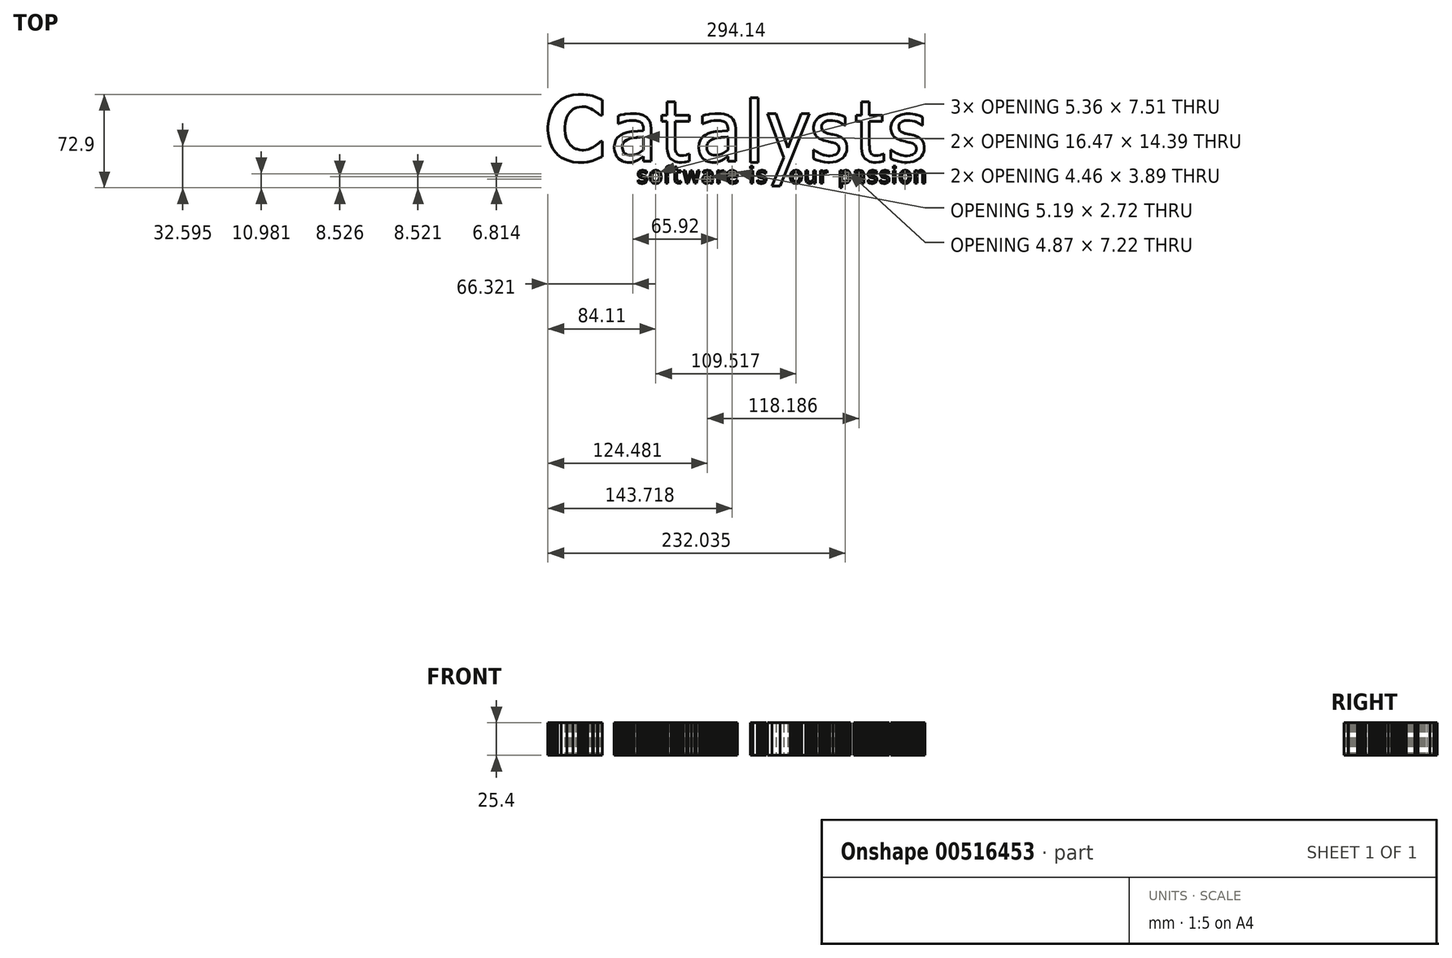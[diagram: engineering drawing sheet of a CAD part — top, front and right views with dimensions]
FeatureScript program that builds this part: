
annotation { "Feature Type Name" : "Feature", "Feature Type Description" : "" }
export const myFeature = defineFeature(function(context is Context, id is Id, definition is map)
    precondition{}
    {
        {
            var Q0;
            Q0=qCreatedBy(makeId("Top.planeOp"),FACE);
            var sketch = newSketch(context, id + "F0", { "sketchPlane" : qUnion([Q0])});
            skLineSegment(sketch, "E0", {"start": v(-122.05, -16.67) * mm, "end": v(-123.41, -16.67) * mm});
            skLineSegment(sketch, "E1", {"start": v(-123.41, -16.67) * mm, "end": v(-127.5, -16.24) * mm});
            skLineSegment(sketch, "E2", {"start": v(-127.5, -16.24) * mm, "end": v(-132.36, -14.93) * mm});
            skLineSegment(sketch, "E3", {"start": v(-132.36, -14.93) * mm, "end": v(-136.64, -12.76) * mm});
            skLineSegment(sketch, "E4", {"start": v(-136.64, -12.76) * mm, "end": v(-139.49, -10.56) * mm});
            skLineSegment(sketch, "E5", {"start": v(-139.49, -10.56) * mm, "end": v(-140.31, -9.71) * mm});
            skLineSegment(sketch, "E6", {"start": v(-140.31, -9.71) * mm, "end": v(-141.15, -8.85) * mm});
            skLineSegment(sketch, "E7", {"start": v(-141.15, -8.85) * mm, "end": v(-143.27, -5.89) * mm});
            skLineSegment(sketch, "E8", {"start": v(-143.27, -5.89) * mm, "end": v(-145.38, -1.35) * mm});
            skLineSegment(sketch, "E9", {"start": v(-145.38, -1.35) * mm, "end": v(-146.65, 3.9) * mm});
            skLineSegment(sketch, "E10", {"start": v(-146.65, 3.9) * mm, "end": v(-147.07, 8.36) * mm});
            skLineSegment(sketch, "E11", {"start": v(-147.07, 8.36) * mm, "end": v(-147.07, 9.84) * mm});
            skLineSegment(sketch, "E12", {"start": v(-147.07, 9.84) * mm, "end": v(-147.07, 11.28) * mm});
            skLineSegment(sketch, "E13", {"start": v(-147.07, 11.28) * mm, "end": v(-146.65, 15.6) * mm});
            skLineSegment(sketch, "E14", {"start": v(-146.65, 15.6) * mm, "end": v(-145.38, 20.76) * mm});
            skLineSegment(sketch, "E15", {"start": v(-145.38, 20.76) * mm, "end": v(-143.26, 25.3) * mm});
            skLineSegment(sketch, "E16", {"start": v(-143.26, 25.3) * mm, "end": v(-141.13, 28.33) * mm});
            skLineSegment(sketch, "E17", {"start": v(-141.13, 28.33) * mm, "end": v(-140.3, 29.22) * mm});
            skLineSegment(sketch, "E18", {"start": v(-140.3, 29.22) * mm, "end": v(-139.47, 30.1) * mm});
            skLineSegment(sketch, "E19", {"start": v(-139.47, 30.1) * mm, "end": v(-136.61, 32.38) * mm});
            skLineSegment(sketch, "E20", {"start": v(-136.61, 32.38) * mm, "end": v(-132.34, 34.64) * mm});
            skLineSegment(sketch, "E21", {"start": v(-132.34, 34.64) * mm, "end": v(-127.47, 36) * mm});
            skLineSegment(sketch, "E22", {"start": v(-127.47, 36) * mm, "end": v(-123.37, 36.45) * mm});
            skLineSegment(sketch, "E23", {"start": v(-123.37, 36.45) * mm, "end": v(-122, 36.45) * mm});
            skLineSegment(sketch, "E24", {"start": v(-122, 36.45) * mm, "end": v(-121.28, 36.45) * mm});
            skLineSegment(sketch, "E25", {"start": v(-121.28, 36.45) * mm, "end": v(-119.1, 36.36) * mm});
            skLineSegment(sketch, "E26", {"start": v(-119.1, 36.36) * mm, "end": v(-116.92, 36.16) * mm});
            skLineSegment(sketch, "E27", {"start": v(-116.92, 36.16) * mm, "end": v(-116.52, 36.1) * mm});
            skLineSegment(sketch, "E28", {"start": v(-116.52, 36.1) * mm, "end": v(-116.11, 36.05) * mm});
            skLineSegment(sketch, "E29", {"start": v(-116.11, 36.05) * mm, "end": v(-112.22, 35.26) * mm});
            skLineSegment(sketch, "E30", {"start": v(-112.22, 35.26) * mm, "end": v(-111.85, 35.15) * mm});
            skLineSegment(sketch, "E31", {"start": v(-111.85, 35.15) * mm, "end": v(-111.56, 35.06) * mm});
            skLineSegment(sketch, "E32", {"start": v(-111.56, 35.06) * mm, "end": v(-110.02, 34.53) * mm});
            skLineSegment(sketch, "E33", {"start": v(-110.02, 34.53) * mm, "end": v(-108.37, 33.88) * mm});
            skLineSegment(sketch, "E34", {"start": v(-108.37, 33.88) * mm, "end": v(-108.02, 33.73) * mm});
            skLineSegment(sketch, "E35", {"start": v(-108.02, 33.73) * mm, "end": v(-107.69, 33.58) * mm});
            skLineSegment(sketch, "E36", {"start": v(-107.69, 33.58) * mm, "end": v(-106.17, 32.9) * mm});
            skLineSegment(sketch, "E37", {"start": v(-106.17, 32.9) * mm, "end": v(-104.9, 32.3) * mm});
            skLineSegment(sketch, "E38", {"start": v(-104.9, 32.3) * mm, "end": v(-104.7, 32.19) * mm});
            skLineSegment(sketch, "E39", {"start": v(-104.7, 32.19) * mm, "end": v(-104.7, 20) * mm});
            skLineSegment(sketch, "E40", {"start": v(-104.7, 20) * mm, "end": v(-106, 20) * mm});
            skLineSegment(sketch, "E41", {"start": v(-106, 20) * mm, "end": v(-106.16, 20.14) * mm});
            skLineSegment(sketch, "E42", {"start": v(-106.16, 20.14) * mm, "end": v(-107.06, 20.91) * mm});
            skLineSegment(sketch, "E43", {"start": v(-107.06, 20.91) * mm, "end": v(-108.1, 21.78) * mm});
            skLineSegment(sketch, "E44", {"start": v(-108.1, 21.78) * mm, "end": v(-108.34, 21.97) * mm});
            skLineSegment(sketch, "E45", {"start": v(-108.34, 21.97) * mm, "end": v(-108.57, 22.16) * mm});
            skLineSegment(sketch, "E46", {"start": v(-108.57, 22.16) * mm, "end": v(-111.24, 24.05) * mm});
            skLineSegment(sketch, "E47", {"start": v(-111.24, 24.05) * mm, "end": v(-111.54, 24.23) * mm});
            skLineSegment(sketch, "E48", {"start": v(-111.54, 24.23) * mm, "end": v(-111.83, 24.41) * mm});
            skLineSegment(sketch, "E49", {"start": v(-111.83, 24.41) * mm, "end": v(-113.4, 25.25) * mm});
            skLineSegment(sketch, "E50", {"start": v(-113.4, 25.25) * mm, "end": v(-115.1, 25.97) * mm});
            skLineSegment(sketch, "E51", {"start": v(-115.1, 25.97) * mm, "end": v(-115.46, 26.1) * mm});
            skLineSegment(sketch, "E52", {"start": v(-115.46, 26.1) * mm, "end": v(-115.82, 26.22) * mm});
            skLineSegment(sketch, "E53", {"start": v(-115.82, 26.22) * mm, "end": v(-117.67, 26.67) * mm});
            skLineSegment(sketch, "E54", {"start": v(-117.67, 26.67) * mm, "end": v(-119.37, 26.86) * mm});
            skLineSegment(sketch, "E55", {"start": v(-119.37, 26.86) * mm, "end": v(-119.94, 26.86) * mm});
            skLineSegment(sketch, "E56", {"start": v(-119.94, 26.86) * mm, "end": v(-120.61, 26.86) * mm});
            skLineSegment(sketch, "E57", {"start": v(-120.61, 26.86) * mm, "end": v(-122.61, 26.64) * mm});
            skLineSegment(sketch, "E58", {"start": v(-122.61, 26.64) * mm, "end": v(-124.66, 26.14) * mm});
            skLineSegment(sketch, "E59", {"start": v(-124.66, 26.14) * mm, "end": v(-125.04, 26) * mm});
            skLineSegment(sketch, "E60", {"start": v(-125.04, 26) * mm, "end": v(-125.43, 25.85) * mm});
            skLineSegment(sketch, "E61", {"start": v(-125.43, 25.85) * mm, "end": v(-127.3, 24.8) * mm});
            skLineSegment(sketch, "E62", {"start": v(-127.3, 24.8) * mm, "end": v(-129.1, 23.32) * mm});
            skLineSegment(sketch, "E63", {"start": v(-129.1, 23.32) * mm, "end": v(-129.46, 22.96) * mm});
            skLineSegment(sketch, "E64", {"start": v(-129.46, 22.96) * mm, "end": v(-129.78, 22.63) * mm});
            skLineSegment(sketch, "E65", {"start": v(-129.78, 22.63) * mm, "end": v(-131.22, 20.65) * mm});
            skLineSegment(sketch, "E66", {"start": v(-131.22, 20.65) * mm, "end": v(-132.4, 18.22) * mm});
            skLineSegment(sketch, "E67", {"start": v(-132.4, 18.22) * mm, "end": v(-132.61, 17.66) * mm});
            skLineSegment(sketch, "E68", {"start": v(-132.61, 17.66) * mm, "end": v(-132.81, 17.1) * mm});
            skLineSegment(sketch, "E69", {"start": v(-132.81, 17.1) * mm, "end": v(-133.52, 14.04) * mm});
            skLineSegment(sketch, "E70", {"start": v(-133.52, 14.04) * mm, "end": v(-133.81, 10.86) * mm});
            skLineSegment(sketch, "E71", {"start": v(-133.81, 10.86) * mm, "end": v(-133.81, 9.8) * mm});
            skLineSegment(sketch, "E72", {"start": v(-133.81, 9.8) * mm, "end": v(-133.81, 8.7) * mm});
            skLineSegment(sketch, "E73", {"start": v(-133.81, 8.7) * mm, "end": v(-133.5, 5.41) * mm});
            skLineSegment(sketch, "E74", {"start": v(-133.5, 5.41) * mm, "end": v(-132.76, 2.32) * mm});
            skLineSegment(sketch, "E75", {"start": v(-132.76, 2.32) * mm, "end": v(-132.54, 1.78) * mm});
            skLineSegment(sketch, "E76", {"start": v(-132.54, 1.78) * mm, "end": v(-132.33, 1.24) * mm});
            skLineSegment(sketch, "E77", {"start": v(-132.33, 1.24) * mm, "end": v(-131.08, -1.15) * mm});
            skLineSegment(sketch, "E78", {"start": v(-131.08, -1.15) * mm, "end": v(-129.56, -3.12) * mm});
            skLineSegment(sketch, "E79", {"start": v(-129.56, -3.12) * mm, "end": v(-129.21, -3.46) * mm});
            skLineSegment(sketch, "E80", {"start": v(-129.21, -3.46) * mm, "end": v(-128.88, -3.78) * mm});
            skLineSegment(sketch, "E81", {"start": v(-128.88, -3.78) * mm, "end": v(-127.1, -5.1) * mm});
            skLineSegment(sketch, "E82", {"start": v(-127.1, -5.1) * mm, "end": v(-125.18, -6.08) * mm});
            skLineSegment(sketch, "E83", {"start": v(-125.18, -6.08) * mm, "end": v(-124.77, -6.22) * mm});
            skLineSegment(sketch, "E84", {"start": v(-124.77, -6.22) * mm, "end": v(-124.36, -6.37) * mm});
            skLineSegment(sketch, "E85", {"start": v(-124.36, -6.37) * mm, "end": v(-122.32, -6.87) * mm});
            skLineSegment(sketch, "E86", {"start": v(-122.32, -6.87) * mm, "end": v(-120.49, -7.08) * mm});
            skLineSegment(sketch, "E87", {"start": v(-120.49, -7.08) * mm, "end": v(-119.88, -7.08) * mm});
            skLineSegment(sketch, "E88", {"start": v(-119.88, -7.08) * mm, "end": v(-119.26, -7.08) * mm});
            skLineSegment(sketch, "E89", {"start": v(-119.26, -7.08) * mm, "end": v(-117.4, -6.88) * mm});
            skLineSegment(sketch, "E90", {"start": v(-117.4, -6.88) * mm, "end": v(-115.41, -6.39) * mm});
            skLineSegment(sketch, "E91", {"start": v(-115.41, -6.39) * mm, "end": v(-115.03, -6.25) * mm});
            skLineSegment(sketch, "E92", {"start": v(-115.03, -6.25) * mm, "end": v(-114.65, -6.1) * mm});
            skLineSegment(sketch, "E93", {"start": v(-114.65, -6.1) * mm, "end": v(-112.92, -5.36) * mm});
            skLineSegment(sketch, "E94", {"start": v(-112.92, -5.36) * mm, "end": v(-111.42, -4.56) * mm});
            skLineSegment(sketch, "E95", {"start": v(-111.42, -4.56) * mm, "end": v(-111.15, -4.39) * mm});
            skLineSegment(sketch, "E96", {"start": v(-111.15, -4.39) * mm, "end": v(-110.87, -4.2) * mm});
            skLineSegment(sketch, "E97", {"start": v(-110.87, -4.2) * mm, "end": v(-108.35, -2.4) * mm});
            skLineSegment(sketch, "E98", {"start": v(-108.35, -2.4) * mm, "end": v(-108.14, -2.21) * mm});
            skLineSegment(sketch, "E99", {"start": v(-108.14, -2.21) * mm, "end": v(-107.92, -2.03) * mm});
            skLineSegment(sketch, "E100", {"start": v(-107.92, -2.03) * mm, "end": v(-106.03, -0.4) * mm});
            skLineSegment(sketch, "E101", {"start": v(-106.03, -0.4) * mm, "end": v(-105.87, -0.26) * mm});
            skLineSegment(sketch, "E102", {"start": v(-105.87, -0.26) * mm, "end": v(-104.7, -0.26) * mm});
            skLineSegment(sketch, "E103", {"start": v(-104.7, -0.26) * mm, "end": v(-104.7, -12.27) * mm});
            skLineSegment(sketch, "E104", {"start": v(-104.7, -12.27) * mm, "end": v(-104.93, -12.38) * mm});
            skLineSegment(sketch, "E105", {"start": v(-104.93, -12.38) * mm, "end": v(-107.65, -13.63) * mm});
            skLineSegment(sketch, "E106", {"start": v(-107.65, -13.63) * mm, "end": v(-107.96, -13.77) * mm});
            skLineSegment(sketch, "E107", {"start": v(-107.96, -13.77) * mm, "end": v(-108.27, -13.9) * mm});
            skLineSegment(sketch, "E108", {"start": v(-108.27, -13.9) * mm, "end": v(-111.46, -15.1) * mm});
            skLineSegment(sketch, "E109", {"start": v(-111.46, -15.1) * mm, "end": v(-111.79, -15.2) * mm});
            skLineSegment(sketch, "E110", {"start": v(-111.79, -15.2) * mm, "end": v(-112.18, -15.32) * mm});
            skLineSegment(sketch, "E111", {"start": v(-112.18, -15.32) * mm, "end": v(-115.92, -16.22) * mm});
            skLineSegment(sketch, "E112", {"start": v(-115.92, -16.22) * mm, "end": v(-116.27, -16.28) * mm});
            skLineSegment(sketch, "E113", {"start": v(-116.27, -16.28) * mm, "end": v(-116.62, -16.35) * mm});
            skLineSegment(sketch, "E114", {"start": v(-116.62, -16.35) * mm, "end": v(-118.77, -16.58) * mm});
            skLineSegment(sketch, "E115", {"start": v(-118.77, -16.58) * mm, "end": v(-121.23, -16.67) * mm});
            skLineSegment(sketch, "E116", {"start": v(-121.23, -16.67) * mm, "end": v(-122.05, -16.67) * mm});
            skLineSegment(sketch, "E117", {"start": v(-72.51, -6.72) * mm, "end": v(-72.51, 3.34) * mm});
            skLineSegment(sketch, "E118", {"start": v(-72.51, 3.34) * mm, "end": v(-72.87, 3.3) * mm});
            skLineSegment(sketch, "E119", {"start": v(-72.87, 3.3) * mm, "end": v(-74.97, 3.1) * mm});
            skLineSegment(sketch, "E120", {"start": v(-74.97, 3.1) * mm, "end": v(-77.44, 2.85) * mm});
            skLineSegment(sketch, "E121", {"start": v(-77.44, 2.85) * mm, "end": v(-78, 2.8) * mm});
            skLineSegment(sketch, "E122", {"start": v(-78, 2.8) * mm, "end": v(-78.55, 2.74) * mm});
            skLineSegment(sketch, "E123", {"start": v(-78.55, 2.74) * mm, "end": v(-81, 2.39) * mm});
            skLineSegment(sketch, "E124", {"start": v(-81, 2.39) * mm, "end": v(-83.03, 1.95) * mm});
            skLineSegment(sketch, "E125", {"start": v(-83.03, 1.95) * mm, "end": v(-83.37, 1.85) * mm});
            skLineSegment(sketch, "E126", {"start": v(-83.37, 1.85) * mm, "end": v(-83.77, 1.72) * mm});
            skLineSegment(sketch, "E127", {"start": v(-83.77, 1.72) * mm, "end": v(-85.6, 0.9) * mm});
            skLineSegment(sketch, "E128", {"start": v(-85.6, 0.9) * mm, "end": v(-87.13, -0.2) * mm});
            skLineSegment(sketch, "E129", {"start": v(-87.13, -0.2) * mm, "end": v(-87.4, -0.45) * mm});
            skLineSegment(sketch, "E130", {"start": v(-87.4, -0.45) * mm, "end": v(-87.6, -0.64) * mm});
            skLineSegment(sketch, "E131", {"start": v(-87.6, -0.64) * mm, "end": v(-88.1, -1.3) * mm});
            skLineSegment(sketch, "E132", {"start": v(-88.1, -1.3) * mm, "end": v(-88.6, -2.3) * mm});
            skLineSegment(sketch, "E133", {"start": v(-88.6, -2.3) * mm, "end": v(-88.89, -3.45) * mm});
            skLineSegment(sketch, "E134", {"start": v(-88.89, -3.45) * mm, "end": v(-88.99, -4.42) * mm});
            skLineSegment(sketch, "E135", {"start": v(-88.99, -4.42) * mm, "end": v(-88.99, -4.75) * mm});
            skLineSegment(sketch, "E136", {"start": v(-88.99, -4.75) * mm, "end": v(-88.99, -5.12) * mm});
            skLineSegment(sketch, "E137", {"start": v(-88.99, -5.12) * mm, "end": v(-88.88, -6.22) * mm});
            skLineSegment(sketch, "E138", {"start": v(-88.88, -6.22) * mm, "end": v(-88.55, -7.49) * mm});
            skLineSegment(sketch, "E139", {"start": v(-88.55, -7.49) * mm, "end": v(-88, -8.57) * mm});
            skLineSegment(sketch, "E140", {"start": v(-88, -8.57) * mm, "end": v(-87.46, -9.27) * mm});
            skLineSegment(sketch, "E141", {"start": v(-87.46, -9.27) * mm, "end": v(-87.24, -9.46) * mm});
            skLineSegment(sketch, "E142", {"start": v(-87.24, -9.46) * mm, "end": v(-87.02, -9.66) * mm});
            skLineSegment(sketch, "E143", {"start": v(-87.02, -9.66) * mm, "end": v(-86.26, -10.15) * mm});
            skLineSegment(sketch, "E144", {"start": v(-86.26, -10.15) * mm, "end": v(-85.08, -10.65) * mm});
            skLineSegment(sketch, "E145", {"start": v(-85.08, -10.65) * mm, "end": v(-83.7, -10.95) * mm});
            skLineSegment(sketch, "E146", {"start": v(-83.7, -10.95) * mm, "end": v(-82.5, -11.05) * mm});
            skLineSegment(sketch, "E147", {"start": v(-82.5, -11.05) * mm, "end": v(-82.1, -11.05) * mm});
            skLineSegment(sketch, "E148", {"start": v(-82.1, -11.05) * mm, "end": v(-81.41, -11.05) * mm});
            skLineSegment(sketch, "E149", {"start": v(-81.41, -11.05) * mm, "end": v(-79.36, -10.73) * mm});
            skLineSegment(sketch, "E150", {"start": v(-79.36, -10.73) * mm, "end": v(-77.28, -10) * mm});
            skLineSegment(sketch, "E151", {"start": v(-77.28, -10) * mm, "end": v(-76.88, -9.8) * mm});
            skLineSegment(sketch, "E152", {"start": v(-76.88, -9.8) * mm, "end": v(-76.5, -9.6) * mm});
            skLineSegment(sketch, "E153", {"start": v(-76.5, -9.6) * mm, "end": v(-74.62, -8.4) * mm});
            skLineSegment(sketch, "E154", {"start": v(-74.62, -8.4) * mm, "end": v(-72.85, -7.03) * mm});
            skLineSegment(sketch, "E155", {"start": v(-72.85, -7.03) * mm, "end": v(-72.51, -6.72) * mm});
            skLineSegment(sketch, "E156", {"start": v(-72.51, -11.8) * mm, "end": v(-72.64, -11.89) * mm});
            skLineSegment(sketch, "E157", {"start": v(-72.64, -11.89) * mm, "end": v(-73.38, -12.46) * mm});
            skLineSegment(sketch, "E158", {"start": v(-73.38, -12.46) * mm, "end": v(-74.3, -13.17) * mm});
            skLineSegment(sketch, "E159", {"start": v(-74.3, -13.17) * mm, "end": v(-74.5, -13.34) * mm});
            skLineSegment(sketch, "E160", {"start": v(-74.5, -13.34) * mm, "end": v(-74.7, -13.5) * mm});
            skLineSegment(sketch, "E161", {"start": v(-74.7, -13.5) * mm, "end": v(-76.72, -14.8) * mm});
            skLineSegment(sketch, "E162", {"start": v(-76.72, -14.8) * mm, "end": v(-76.9, -14.9) * mm});
            skLineSegment(sketch, "E163", {"start": v(-76.9, -14.9) * mm, "end": v(-77.18, -15.04) * mm});
            skLineSegment(sketch, "E164", {"start": v(-77.18, -15.04) * mm, "end": v(-79.79, -16.14) * mm});
            skLineSegment(sketch, "E165", {"start": v(-79.79, -16.14) * mm, "end": v(-80.03, -16.22) * mm});
            skLineSegment(sketch, "E166", {"start": v(-80.03, -16.22) * mm, "end": v(-80.29, -16.29) * mm});
            skLineSegment(sketch, "E167", {"start": v(-80.29, -16.29) * mm, "end": v(-81.86, -16.55) * mm});
            skLineSegment(sketch, "E168", {"start": v(-81.86, -16.55) * mm, "end": v(-83.67, -16.67) * mm});
            skLineSegment(sketch, "E169", {"start": v(-83.67, -16.67) * mm, "end": v(-84.27, -16.67) * mm});
            skLineSegment(sketch, "E170", {"start": v(-84.27, -16.67) * mm, "end": v(-84.82, -16.67) * mm});
            skLineSegment(sketch, "E171", {"start": v(-84.82, -16.67) * mm, "end": v(-86.46, -16.45) * mm});
            skLineSegment(sketch, "E172", {"start": v(-86.46, -16.45) * mm, "end": v(-88.2, -15.95) * mm});
            skLineSegment(sketch, "E173", {"start": v(-88.2, -15.95) * mm, "end": v(-88.53, -15.8) * mm});
            skLineSegment(sketch, "E174", {"start": v(-88.53, -15.8) * mm, "end": v(-88.87, -15.67) * mm});
            skLineSegment(sketch, "E175", {"start": v(-88.87, -15.67) * mm, "end": v(-90.42, -14.8) * mm});
            skLineSegment(sketch, "E176", {"start": v(-90.42, -14.8) * mm, "end": v(-91.81, -13.7) * mm});
            skLineSegment(sketch, "E177", {"start": v(-91.81, -13.7) * mm, "end": v(-92.07, -13.45) * mm});
            skLineSegment(sketch, "E178", {"start": v(-92.07, -13.45) * mm, "end": v(-92.31, -13.2) * mm});
            skLineSegment(sketch, "E179", {"start": v(-92.31, -13.2) * mm, "end": v(-93.38, -11.78) * mm});
            skLineSegment(sketch, "E180", {"start": v(-93.38, -11.78) * mm, "end": v(-94.25, -10.13) * mm});
            skLineSegment(sketch, "E181", {"start": v(-94.25, -10.13) * mm, "end": v(-94.4, -9.76) * mm});
            skLineSegment(sketch, "E182", {"start": v(-94.4, -9.76) * mm, "end": v(-94.55, -9.4) * mm});
            skLineSegment(sketch, "E183", {"start": v(-94.55, -9.4) * mm, "end": v(-95.07, -7.51) * mm});
            skLineSegment(sketch, "E184", {"start": v(-95.07, -7.51) * mm, "end": v(-95.29, -5.73) * mm});
            skLineSegment(sketch, "E185", {"start": v(-95.29, -5.73) * mm, "end": v(-95.29, -5.14) * mm});
            skLineSegment(sketch, "E186", {"start": v(-95.29, -5.14) * mm, "end": v(-95.29, -4.26) * mm});
            skLineSegment(sketch, "E187", {"start": v(-95.29, -4.26) * mm, "end": v(-94.9, -1.65) * mm});
            skLineSegment(sketch, "E188", {"start": v(-94.9, -1.65) * mm, "end": v(-93.97, 0.84) * mm});
            skLineSegment(sketch, "E189", {"start": v(-93.97, 0.84) * mm, "end": v(-93.7, 1.28) * mm});
            skLineSegment(sketch, "E190", {"start": v(-93.7, 1.28) * mm, "end": v(-93.5, 1.6) * mm});
            skLineSegment(sketch, "E191", {"start": v(-93.5, 1.6) * mm, "end": v(-92.79, 2.53) * mm});
            skLineSegment(sketch, "E192", {"start": v(-92.79, 2.53) * mm, "end": v(-91.64, 3.65) * mm});
            skLineSegment(sketch, "E193", {"start": v(-91.64, 3.65) * mm, "end": v(-90.27, 4.62) * mm});
            skLineSegment(sketch, "E194", {"start": v(-90.27, 4.62) * mm, "end": v(-89.08, 5.28) * mm});
            skLineSegment(sketch, "E195", {"start": v(-89.08, 5.28) * mm, "end": v(-88.67, 5.47) * mm});
            skLineSegment(sketch, "E196", {"start": v(-88.67, 5.47) * mm, "end": v(-88.16, 5.7) * mm});
            skLineSegment(sketch, "E197", {"start": v(-88.16, 5.7) * mm, "end": v(-85.34, 6.65) * mm});
            skLineSegment(sketch, "E198", {"start": v(-85.34, 6.65) * mm, "end": v(-82.15, 7.31) * mm});
            skLineSegment(sketch, "E199", {"start": v(-82.15, 7.31) * mm, "end": v(-81.46, 7.4) * mm});
            skLineSegment(sketch, "E200", {"start": v(-81.46, 7.4) * mm, "end": v(-80.77, 7.49) * mm});
            skLineSegment(sketch, "E201", {"start": v(-80.77, 7.49) * mm, "end": v(-73.31, 8.15) * mm});
            skLineSegment(sketch, "E202", {"start": v(-73.31, 8.15) * mm, "end": v(-72.51, 8.19) * mm});
            skLineSegment(sketch, "E203", {"start": v(-72.51, 8.19) * mm, "end": v(-72.51, 9.37) * mm});
            skLineSegment(sketch, "E204", {"start": v(-72.51, 9.37) * mm, "end": v(-72.51, 9.85) * mm});
            skLineSegment(sketch, "E205", {"start": v(-72.51, 9.85) * mm, "end": v(-72.67, 11.3) * mm});
            skLineSegment(sketch, "E206", {"start": v(-72.67, 11.3) * mm, "end": v(-73.04, 12.61) * mm});
            skLineSegment(sketch, "E207", {"start": v(-73.04, 12.61) * mm, "end": v(-73.15, 12.83) * mm});
            skLineSegment(sketch, "E208", {"start": v(-73.15, 12.83) * mm, "end": v(-73.25, 13.05) * mm});
            skLineSegment(sketch, "E209", {"start": v(-73.25, 13.05) * mm, "end": v(-73.93, 13.99) * mm});
            skLineSegment(sketch, "E210", {"start": v(-73.93, 13.99) * mm, "end": v(-74.77, 14.73) * mm});
            skLineSegment(sketch, "E211", {"start": v(-74.77, 14.73) * mm, "end": v(-74.96, 14.85) * mm});
            skLineSegment(sketch, "E212", {"start": v(-74.96, 14.85) * mm, "end": v(-75.16, 14.98) * mm});
            skLineSegment(sketch, "E213", {"start": v(-75.16, 14.98) * mm, "end": v(-76.27, 15.48) * mm});
            skLineSegment(sketch, "E214", {"start": v(-76.27, 15.48) * mm, "end": v(-77.54, 15.8) * mm});
            skLineSegment(sketch, "E215", {"start": v(-77.54, 15.8) * mm, "end": v(-77.81, 15.85) * mm});
            skLineSegment(sketch, "E216", {"start": v(-77.81, 15.85) * mm, "end": v(-78.1, 15.89) * mm});
            skLineSegment(sketch, "E217", {"start": v(-78.1, 15.89) * mm, "end": v(-80.5, 16.07) * mm});
            skLineSegment(sketch, "E218", {"start": v(-80.5, 16.07) * mm, "end": v(-81.3, 16.07) * mm});
            skLineSegment(sketch, "E219", {"start": v(-81.3, 16.07) * mm, "end": v(-81.88, 16.07) * mm});
            skLineSegment(sketch, "E220", {"start": v(-81.88, 16.07) * mm, "end": v(-83.6, 15.92) * mm});
            skLineSegment(sketch, "E221", {"start": v(-83.6, 15.92) * mm, "end": v(-85.8, 15.55) * mm});
            skLineSegment(sketch, "E222", {"start": v(-85.8, 15.55) * mm, "end": v(-86.27, 15.44) * mm});
            skLineSegment(sketch, "E223", {"start": v(-86.27, 15.44) * mm, "end": v(-86.74, 15.34) * mm});
            skLineSegment(sketch, "E224", {"start": v(-86.74, 15.34) * mm, "end": v(-91.5, 13.83) * mm});
            skLineSegment(sketch, "E225", {"start": v(-91.5, 13.83) * mm, "end": v(-91.98, 13.63) * mm});
            skLineSegment(sketch, "E226", {"start": v(-91.98, 13.63) * mm, "end": v(-92.34, 13.63) * mm});
            skLineSegment(sketch, "E227", {"start": v(-92.34, 13.63) * mm, "end": v(-92.34, 19.81) * mm});
            skLineSegment(sketch, "E228", {"start": v(-92.34, 19.81) * mm, "end": v(-92.06, 19.9) * mm});
            skLineSegment(sketch, "E229", {"start": v(-92.06, 19.9) * mm, "end": v(-90.28, 20.32) * mm});
            skLineSegment(sketch, "E230", {"start": v(-90.28, 20.32) * mm, "end": v(-88.02, 20.78) * mm});
            skLineSegment(sketch, "E231", {"start": v(-88.02, 20.78) * mm, "end": v(-87.5, 20.88) * mm});
            skLineSegment(sketch, "E232", {"start": v(-87.5, 20.88) * mm, "end": v(-86.97, 20.98) * mm});
            skLineSegment(sketch, "E233", {"start": v(-86.97, 20.98) * mm, "end": v(-82.69, 21.47) * mm});
            skLineSegment(sketch, "E234", {"start": v(-82.69, 21.47) * mm, "end": v(-81.26, 21.47) * mm});
            skLineSegment(sketch, "E235", {"start": v(-81.26, 21.47) * mm, "end": v(-80.4, 21.47) * mm});
            skLineSegment(sketch, "E236", {"start": v(-80.4, 21.47) * mm, "end": v(-77.82, 21.33) * mm});
            skLineSegment(sketch, "E237", {"start": v(-77.82, 21.33) * mm, "end": v(-75.4, 20.98) * mm});
            skLineSegment(sketch, "E238", {"start": v(-75.4, 20.98) * mm, "end": v(-74.96, 20.88) * mm});
            skLineSegment(sketch, "E239", {"start": v(-74.96, 20.88) * mm, "end": v(-74.53, 20.78) * mm});
            skLineSegment(sketch, "E240", {"start": v(-74.53, 20.78) * mm, "end": v(-72.53, 20.06) * mm});
            skLineSegment(sketch, "E241", {"start": v(-72.53, 20.06) * mm, "end": v(-70.7, 19.03) * mm});
            skLineSegment(sketch, "E242", {"start": v(-70.7, 19.03) * mm, "end": v(-70.36, 18.77) * mm});
            skLineSegment(sketch, "E243", {"start": v(-70.36, 18.77) * mm, "end": v(-70.03, 18.52) * mm});
            skLineSegment(sketch, "E244", {"start": v(-70.03, 18.52) * mm, "end": v(-68.63, 17.07) * mm});
            skLineSegment(sketch, "E245", {"start": v(-68.63, 17.07) * mm, "end": v(-67.57, 15.31) * mm});
            skLineSegment(sketch, "E246", {"start": v(-67.57, 15.31) * mm, "end": v(-67.41, 14.92) * mm});
            skLineSegment(sketch, "E247", {"start": v(-67.41, 14.92) * mm, "end": v(-67.25, 14.52) * mm});
            skLineSegment(sketch, "E248", {"start": v(-67.25, 14.52) * mm, "end": v(-66.68, 12.29) * mm});
            skLineSegment(sketch, "E249", {"start": v(-66.68, 12.29) * mm, "end": v(-66.44, 9.93) * mm});
            skLineSegment(sketch, "E250", {"start": v(-66.44, 9.93) * mm, "end": v(-66.44, 9.14) * mm});
            skLineSegment(sketch, "E251", {"start": v(-66.44, 9.14) * mm, "end": v(-66.44, -15.65) * mm});
            skLineSegment(sketch, "E252", {"start": v(-66.44, -15.65) * mm, "end": v(-72.51, -15.65) * mm});
            skLineSegment(sketch, "E253", {"start": v(-72.51, -15.65) * mm, "end": v(-72.51, -11.8) * mm});
            skLineSegment(sketch, "E254", {"start": v(-43.4, -16.67) * mm, "end": v(-44.5, -16.67) * mm});
            skLineSegment(sketch, "E255", {"start": v(-44.5, -16.67) * mm, "end": v(-47.84, -15.95) * mm});
            skLineSegment(sketch, "E256", {"start": v(-47.84, -15.95) * mm, "end": v(-50.72, -14.3) * mm});
            skLineSegment(sketch, "E257", {"start": v(-50.72, -14.3) * mm, "end": v(-51.19, -13.81) * mm});
            skLineSegment(sketch, "E258", {"start": v(-51.19, -13.81) * mm, "end": v(-51.54, -13.46) * mm});
            skLineSegment(sketch, "E259", {"start": v(-51.54, -13.46) * mm, "end": v(-52.4, -12.2) * mm});
            skLineSegment(sketch, "E260", {"start": v(-52.4, -12.2) * mm, "end": v(-53.28, -10.16) * mm});
            skLineSegment(sketch, "E261", {"start": v(-53.28, -10.16) * mm, "end": v(-53.8, -7.7) * mm});
            skLineSegment(sketch, "E262", {"start": v(-53.8, -7.7) * mm, "end": v(-53.97, -5.56) * mm});
            skLineSegment(sketch, "E263", {"start": v(-53.97, -5.56) * mm, "end": v(-53.97, -4.84) * mm});
            skLineSegment(sketch, "E264", {"start": v(-53.97, -4.84) * mm, "end": v(-53.97, 15.24) * mm});
            skLineSegment(sketch, "E265", {"start": v(-53.97, 15.24) * mm, "end": v(-58.1, 15.24) * mm});
            skLineSegment(sketch, "E266", {"start": v(-58.1, 15.24) * mm, "end": v(-58.1, 20.3) * mm});
            skLineSegment(sketch, "E267", {"start": v(-58.1, 20.3) * mm, "end": v(-53.97, 20.3) * mm});
            skLineSegment(sketch, "E268", {"start": v(-53.97, 20.3) * mm, "end": v(-53.97, 30.71) * mm});
            skLineSegment(sketch, "E269", {"start": v(-53.97, 30.71) * mm, "end": v(-47.88, 30.71) * mm});
            skLineSegment(sketch, "E270", {"start": v(-47.88, 30.71) * mm, "end": v(-47.88, 20.3) * mm});
            skLineSegment(sketch, "E271", {"start": v(-47.88, 20.3) * mm, "end": v(-36.64, 20.3) * mm});
            skLineSegment(sketch, "E272", {"start": v(-36.64, 20.3) * mm, "end": v(-36.64, 15.24) * mm});
            skLineSegment(sketch, "E273", {"start": v(-36.64, 15.24) * mm, "end": v(-47.88, 15.24) * mm});
            skLineSegment(sketch, "E274", {"start": v(-47.88, 15.24) * mm, "end": v(-47.88, -1.98) * mm});
            skLineSegment(sketch, "E275", {"start": v(-47.88, -1.98) * mm, "end": v(-47.88, -2.6) * mm});
            skLineSegment(sketch, "E276", {"start": v(-47.88, -2.6) * mm, "end": v(-47.86, -4.43) * mm});
            skLineSegment(sketch, "E277", {"start": v(-47.86, -4.43) * mm, "end": v(-47.8, -6) * mm});
            skLineSegment(sketch, "E278", {"start": v(-47.8, -6) * mm, "end": v(-47.79, -6.25) * mm});
            skLineSegment(sketch, "E279", {"start": v(-47.79, -6.25) * mm, "end": v(-47.77, -6.5) * mm});
            skLineSegment(sketch, "E280", {"start": v(-47.77, -6.5) * mm, "end": v(-47.55, -7.69) * mm});
            skLineSegment(sketch, "E281", {"start": v(-47.55, -7.69) * mm, "end": v(-47.15, -8.82) * mm});
            skLineSegment(sketch, "E282", {"start": v(-47.15, -8.82) * mm, "end": v(-47.04, -9.03) * mm});
            skLineSegment(sketch, "E283", {"start": v(-47.04, -9.03) * mm, "end": v(-46.95, -9.22) * mm});
            skLineSegment(sketch, "E284", {"start": v(-46.95, -9.22) * mm, "end": v(-46.31, -10.03) * mm});
            skLineSegment(sketch, "E285", {"start": v(-46.31, -10.03) * mm, "end": v(-45.45, -10.64) * mm});
            skLineSegment(sketch, "E286", {"start": v(-45.45, -10.64) * mm, "end": v(-45.25, -10.73) * mm});
            skLineSegment(sketch, "E287", {"start": v(-45.25, -10.73) * mm, "end": v(-45.05, -10.83) * mm});
            skLineSegment(sketch, "E288", {"start": v(-45.05, -10.83) * mm, "end": v(-43.8, -11.16) * mm});
            skLineSegment(sketch, "E289", {"start": v(-43.8, -11.16) * mm, "end": v(-42.37, -11.3) * mm});
            skLineSegment(sketch, "E290", {"start": v(-42.37, -11.3) * mm, "end": v(-41.9, -11.3) * mm});
            skLineSegment(sketch, "E291", {"start": v(-41.9, -11.3) * mm, "end": v(-41.18, -11.3) * mm});
            skLineSegment(sketch, "E292", {"start": v(-41.18, -11.3) * mm, "end": v(-39.25, -10.94) * mm});
            skLineSegment(sketch, "E293", {"start": v(-39.25, -10.94) * mm, "end": v(-39.02, -10.87) * mm});
            skLineSegment(sketch, "E294", {"start": v(-39.02, -10.87) * mm, "end": v(-38.79, -10.8) * mm});
            skLineSegment(sketch, "E295", {"start": v(-38.79, -10.8) * mm, "end": v(-37.81, -10.46) * mm});
            skLineSegment(sketch, "E296", {"start": v(-37.81, -10.46) * mm, "end": v(-37.1, -10.19) * mm});
            skLineSegment(sketch, "E297", {"start": v(-37.1, -10.19) * mm, "end": v(-37, -10.14) * mm});
            skLineSegment(sketch, "E298", {"start": v(-37, -10.14) * mm, "end": v(-36.64, -10.14) * mm});
            skLineSegment(sketch, "E299", {"start": v(-36.64, -10.14) * mm, "end": v(-36.64, -15.63) * mm});
            skLineSegment(sketch, "E300", {"start": v(-36.64, -15.63) * mm, "end": v(-36.93, -15.7) * mm});
            skLineSegment(sketch, "E301", {"start": v(-36.93, -15.7) * mm, "end": v(-39.83, -16.33) * mm});
            skLineSegment(sketch, "E302", {"start": v(-39.83, -16.33) * mm, "end": v(-40.13, -16.38) * mm});
            skLineSegment(sketch, "E303", {"start": v(-40.13, -16.38) * mm, "end": v(-40.42, -16.43) * mm});
            skLineSegment(sketch, "E304", {"start": v(-40.42, -16.43) * mm, "end": v(-42.65, -16.67) * mm});
            skLineSegment(sketch, "E305", {"start": v(-42.65, -16.67) * mm, "end": v(-43.4, -16.67) * mm});
            skLineSegment(sketch, "E306", {"start": v(-6.6, -6.72) * mm, "end": v(-6.6, 3.34) * mm});
            skLineSegment(sketch, "E307", {"start": v(-6.6, 3.34) * mm, "end": v(-6.95, 3.3) * mm});
            skLineSegment(sketch, "E308", {"start": v(-6.95, 3.3) * mm, "end": v(-9.04, 3.1) * mm});
            skLineSegment(sketch, "E309", {"start": v(-9.04, 3.1) * mm, "end": v(-11.52, 2.85) * mm});
            skLineSegment(sketch, "E310", {"start": v(-11.52, 2.85) * mm, "end": v(-12.08, 2.8) * mm});
            skLineSegment(sketch, "E311", {"start": v(-12.08, 2.8) * mm, "end": v(-12.63, 2.74) * mm});
            skLineSegment(sketch, "E312", {"start": v(-12.63, 2.74) * mm, "end": v(-15.08, 2.39) * mm});
            skLineSegment(sketch, "E313", {"start": v(-15.08, 2.39) * mm, "end": v(-17.1, 1.95) * mm});
            skLineSegment(sketch, "E314", {"start": v(-17.1, 1.95) * mm, "end": v(-17.45, 1.85) * mm});
            skLineSegment(sketch, "E315", {"start": v(-17.45, 1.85) * mm, "end": v(-17.85, 1.72) * mm});
            skLineSegment(sketch, "E316", {"start": v(-17.85, 1.72) * mm, "end": v(-19.68, 0.9) * mm});
            skLineSegment(sketch, "E317", {"start": v(-19.68, 0.9) * mm, "end": v(-21.21, -0.2) * mm});
            skLineSegment(sketch, "E318", {"start": v(-21.21, -0.2) * mm, "end": v(-21.48, -0.45) * mm});
            skLineSegment(sketch, "E319", {"start": v(-21.48, -0.45) * mm, "end": v(-21.67, -0.64) * mm});
            skLineSegment(sketch, "E320", {"start": v(-21.67, -0.64) * mm, "end": v(-22.18, -1.3) * mm});
            skLineSegment(sketch, "E321", {"start": v(-22.18, -1.3) * mm, "end": v(-22.67, -2.3) * mm});
            skLineSegment(sketch, "E322", {"start": v(-22.67, -2.3) * mm, "end": v(-22.97, -3.45) * mm});
            skLineSegment(sketch, "E323", {"start": v(-22.97, -3.45) * mm, "end": v(-23.07, -4.42) * mm});
            skLineSegment(sketch, "E324", {"start": v(-23.07, -4.42) * mm, "end": v(-23.07, -4.75) * mm});
            skLineSegment(sketch, "E325", {"start": v(-23.07, -4.75) * mm, "end": v(-23.07, -5.12) * mm});
            skLineSegment(sketch, "E326", {"start": v(-23.07, -5.12) * mm, "end": v(-22.96, -6.22) * mm});
            skLineSegment(sketch, "E327", {"start": v(-22.96, -6.22) * mm, "end": v(-22.63, -7.49) * mm});
            skLineSegment(sketch, "E328", {"start": v(-22.63, -7.49) * mm, "end": v(-22.08, -8.57) * mm});
            skLineSegment(sketch, "E329", {"start": v(-22.08, -8.57) * mm, "end": v(-21.54, -9.27) * mm});
            skLineSegment(sketch, "E330", {"start": v(-21.54, -9.27) * mm, "end": v(-21.32, -9.46) * mm});
            skLineSegment(sketch, "E331", {"start": v(-21.32, -9.46) * mm, "end": v(-21.1, -9.66) * mm});
            skLineSegment(sketch, "E332", {"start": v(-21.1, -9.66) * mm, "end": v(-20.34, -10.15) * mm});
            skLineSegment(sketch, "E333", {"start": v(-20.34, -10.15) * mm, "end": v(-19.16, -10.65) * mm});
            skLineSegment(sketch, "E334", {"start": v(-19.16, -10.65) * mm, "end": v(-17.77, -10.95) * mm});
            skLineSegment(sketch, "E335", {"start": v(-17.77, -10.95) * mm, "end": v(-16.58, -11.05) * mm});
            skLineSegment(sketch, "E336", {"start": v(-16.58, -11.05) * mm, "end": v(-16.18, -11.05) * mm});
            skLineSegment(sketch, "E337", {"start": v(-16.18, -11.05) * mm, "end": v(-15.5, -11.05) * mm});
            skLineSegment(sketch, "E338", {"start": v(-15.5, -11.05) * mm, "end": v(-13.44, -10.73) * mm});
            skLineSegment(sketch, "E339", {"start": v(-13.44, -10.73) * mm, "end": v(-11.36, -10) * mm});
            skLineSegment(sketch, "E340", {"start": v(-11.36, -10) * mm, "end": v(-10.96, -9.8) * mm});
            skLineSegment(sketch, "E341", {"start": v(-10.96, -9.8) * mm, "end": v(-10.57, -9.6) * mm});
            skLineSegment(sketch, "E342", {"start": v(-10.57, -9.6) * mm, "end": v(-8.7, -8.4) * mm});
            skLineSegment(sketch, "E343", {"start": v(-8.7, -8.4) * mm, "end": v(-6.93, -7.03) * mm});
            skLineSegment(sketch, "E344", {"start": v(-6.93, -7.03) * mm, "end": v(-6.6, -6.72) * mm});
            skLineSegment(sketch, "E345", {"start": v(-6.6, -11.8) * mm, "end": v(-6.72, -11.89) * mm});
            skLineSegment(sketch, "E346", {"start": v(-6.72, -11.89) * mm, "end": v(-7.46, -12.46) * mm});
            skLineSegment(sketch, "E347", {"start": v(-7.46, -12.46) * mm, "end": v(-8.38, -13.17) * mm});
            skLineSegment(sketch, "E348", {"start": v(-8.38, -13.17) * mm, "end": v(-8.59, -13.34) * mm});
            skLineSegment(sketch, "E349", {"start": v(-8.59, -13.34) * mm, "end": v(-8.8, -13.5) * mm});
            skLineSegment(sketch, "E350", {"start": v(-8.8, -13.5) * mm, "end": v(-10.8, -14.8) * mm});
            skLineSegment(sketch, "E351", {"start": v(-10.8, -14.8) * mm, "end": v(-10.99, -14.9) * mm});
            skLineSegment(sketch, "E352", {"start": v(-10.99, -14.9) * mm, "end": v(-11.26, -15.04) * mm});
            skLineSegment(sketch, "E353", {"start": v(-11.26, -15.04) * mm, "end": v(-13.87, -16.14) * mm});
            skLineSegment(sketch, "E354", {"start": v(-13.87, -16.14) * mm, "end": v(-14.11, -16.22) * mm});
            skLineSegment(sketch, "E355", {"start": v(-14.11, -16.22) * mm, "end": v(-14.37, -16.29) * mm});
            skLineSegment(sketch, "E356", {"start": v(-14.37, -16.29) * mm, "end": v(-15.94, -16.55) * mm});
            skLineSegment(sketch, "E357", {"start": v(-15.94, -16.55) * mm, "end": v(-17.75, -16.67) * mm});
            skLineSegment(sketch, "E358", {"start": v(-17.75, -16.67) * mm, "end": v(-18.35, -16.67) * mm});
            skLineSegment(sketch, "E359", {"start": v(-18.35, -16.67) * mm, "end": v(-18.9, -16.67) * mm});
            skLineSegment(sketch, "E360", {"start": v(-18.9, -16.67) * mm, "end": v(-20.54, -16.45) * mm});
            skLineSegment(sketch, "E361", {"start": v(-20.54, -16.45) * mm, "end": v(-22.28, -15.95) * mm});
            skLineSegment(sketch, "E362", {"start": v(-22.28, -15.95) * mm, "end": v(-22.61, -15.8) * mm});
            skLineSegment(sketch, "E363", {"start": v(-22.61, -15.8) * mm, "end": v(-22.95, -15.67) * mm});
            skLineSegment(sketch, "E364", {"start": v(-22.95, -15.67) * mm, "end": v(-24.5, -14.8) * mm});
            skLineSegment(sketch, "E365", {"start": v(-24.5, -14.8) * mm, "end": v(-25.9, -13.7) * mm});
            skLineSegment(sketch, "E366", {"start": v(-25.9, -13.7) * mm, "end": v(-26.15, -13.45) * mm});
            skLineSegment(sketch, "E367", {"start": v(-26.15, -13.45) * mm, "end": v(-26.4, -13.2) * mm});
            skLineSegment(sketch, "E368", {"start": v(-26.4, -13.2) * mm, "end": v(-27.46, -11.78) * mm});
            skLineSegment(sketch, "E369", {"start": v(-27.46, -11.78) * mm, "end": v(-28.33, -10.13) * mm});
            skLineSegment(sketch, "E370", {"start": v(-28.33, -10.13) * mm, "end": v(-28.48, -9.76) * mm});
            skLineSegment(sketch, "E371", {"start": v(-28.48, -9.76) * mm, "end": v(-28.63, -9.4) * mm});
            skLineSegment(sketch, "E372", {"start": v(-28.63, -9.4) * mm, "end": v(-29.15, -7.51) * mm});
            skLineSegment(sketch, "E373", {"start": v(-29.15, -7.51) * mm, "end": v(-29.37, -5.73) * mm});
            skLineSegment(sketch, "E374", {"start": v(-29.37, -5.73) * mm, "end": v(-29.37, -5.14) * mm});
            skLineSegment(sketch, "E375", {"start": v(-29.37, -5.14) * mm, "end": v(-29.37, -4.26) * mm});
            skLineSegment(sketch, "E376", {"start": v(-29.37, -4.26) * mm, "end": v(-28.96, -1.65) * mm});
            skLineSegment(sketch, "E377", {"start": v(-28.96, -1.65) * mm, "end": v(-28.04, 0.84) * mm});
            skLineSegment(sketch, "E378", {"start": v(-28.04, 0.84) * mm, "end": v(-27.78, 1.28) * mm});
            skLineSegment(sketch, "E379", {"start": v(-27.78, 1.28) * mm, "end": v(-27.58, 1.6) * mm});
            skLineSegment(sketch, "E380", {"start": v(-27.58, 1.6) * mm, "end": v(-26.87, 2.53) * mm});
            skLineSegment(sketch, "E381", {"start": v(-26.87, 2.53) * mm, "end": v(-25.72, 3.65) * mm});
            skLineSegment(sketch, "E382", {"start": v(-25.72, 3.65) * mm, "end": v(-24.35, 4.62) * mm});
            skLineSegment(sketch, "E383", {"start": v(-24.35, 4.62) * mm, "end": v(-23.16, 5.28) * mm});
            skLineSegment(sketch, "E384", {"start": v(-23.16, 5.28) * mm, "end": v(-22.75, 5.47) * mm});
            skLineSegment(sketch, "E385", {"start": v(-22.75, 5.47) * mm, "end": v(-22.24, 5.7) * mm});
            skLineSegment(sketch, "E386", {"start": v(-22.24, 5.7) * mm, "end": v(-19.42, 6.65) * mm});
            skLineSegment(sketch, "E387", {"start": v(-19.42, 6.65) * mm, "end": v(-16.23, 7.31) * mm});
            skLineSegment(sketch, "E388", {"start": v(-16.23, 7.31) * mm, "end": v(-15.54, 7.4) * mm});
            skLineSegment(sketch, "E389", {"start": v(-15.54, 7.4) * mm, "end": v(-14.85, 7.49) * mm});
            skLineSegment(sketch, "E390", {"start": v(-14.85, 7.49) * mm, "end": v(-7.4, 8.15) * mm});
            skLineSegment(sketch, "E391", {"start": v(-7.4, 8.15) * mm, "end": v(-6.6, 8.19) * mm});
            skLineSegment(sketch, "E392", {"start": v(-6.6, 8.19) * mm, "end": v(-6.6, 9.37) * mm});
            skLineSegment(sketch, "E393", {"start": v(-6.6, 9.37) * mm, "end": v(-6.6, 9.85) * mm});
            skLineSegment(sketch, "E394", {"start": v(-6.6, 9.85) * mm, "end": v(-6.75, 11.3) * mm});
            skLineSegment(sketch, "E395", {"start": v(-6.75, 11.3) * mm, "end": v(-7.12, 12.61) * mm});
            skLineSegment(sketch, "E396", {"start": v(-7.12, 12.61) * mm, "end": v(-7.23, 12.83) * mm});
            skLineSegment(sketch, "E397", {"start": v(-7.23, 12.83) * mm, "end": v(-7.33, 13.05) * mm});
            skLineSegment(sketch, "E398", {"start": v(-7.33, 13.05) * mm, "end": v(-8, 13.99) * mm});
            skLineSegment(sketch, "E399", {"start": v(-8, 13.99) * mm, "end": v(-8.85, 14.73) * mm});
            skLineSegment(sketch, "E400", {"start": v(-8.85, 14.73) * mm, "end": v(-9.04, 14.85) * mm});
            skLineSegment(sketch, "E401", {"start": v(-9.04, 14.85) * mm, "end": v(-9.24, 14.98) * mm});
            skLineSegment(sketch, "E402", {"start": v(-9.24, 14.98) * mm, "end": v(-10.35, 15.48) * mm});
            skLineSegment(sketch, "E403", {"start": v(-10.35, 15.48) * mm, "end": v(-11.62, 15.8) * mm});
            skLineSegment(sketch, "E404", {"start": v(-11.62, 15.8) * mm, "end": v(-11.9, 15.85) * mm});
            skLineSegment(sketch, "E405", {"start": v(-11.9, 15.85) * mm, "end": v(-12.18, 15.89) * mm});
            skLineSegment(sketch, "E406", {"start": v(-12.18, 15.89) * mm, "end": v(-14.58, 16.07) * mm});
            skLineSegment(sketch, "E407", {"start": v(-14.58, 16.07) * mm, "end": v(-15.38, 16.07) * mm});
            skLineSegment(sketch, "E408", {"start": v(-15.38, 16.07) * mm, "end": v(-15.96, 16.07) * mm});
            skLineSegment(sketch, "E409", {"start": v(-15.96, 16.07) * mm, "end": v(-17.68, 15.92) * mm});
            skLineSegment(sketch, "E410", {"start": v(-17.68, 15.92) * mm, "end": v(-19.87, 15.55) * mm});
            skLineSegment(sketch, "E411", {"start": v(-19.87, 15.55) * mm, "end": v(-20.35, 15.44) * mm});
            skLineSegment(sketch, "E412", {"start": v(-20.35, 15.44) * mm, "end": v(-20.82, 15.34) * mm});
            skLineSegment(sketch, "E413", {"start": v(-20.82, 15.34) * mm, "end": v(-25.58, 13.83) * mm});
            skLineSegment(sketch, "E414", {"start": v(-25.58, 13.83) * mm, "end": v(-26.06, 13.63) * mm});
            skLineSegment(sketch, "E415", {"start": v(-26.06, 13.63) * mm, "end": v(-26.4, 13.63) * mm});
            skLineSegment(sketch, "E416", {"start": v(-26.4, 13.63) * mm, "end": v(-26.4, 19.81) * mm});
            skLineSegment(sketch, "E417", {"start": v(-26.4, 19.81) * mm, "end": v(-26.12, 19.9) * mm});
            skLineSegment(sketch, "E418", {"start": v(-26.12, 19.9) * mm, "end": v(-24.36, 20.32) * mm});
            skLineSegment(sketch, "E419", {"start": v(-24.36, 20.32) * mm, "end": v(-22.1, 20.78) * mm});
            skLineSegment(sketch, "E420", {"start": v(-22.1, 20.78) * mm, "end": v(-21.57, 20.88) * mm});
            skLineSegment(sketch, "E421", {"start": v(-21.57, 20.88) * mm, "end": v(-21.05, 20.98) * mm});
            skLineSegment(sketch, "E422", {"start": v(-21.05, 20.98) * mm, "end": v(-16.77, 21.47) * mm});
            skLineSegment(sketch, "E423", {"start": v(-16.77, 21.47) * mm, "end": v(-15.34, 21.47) * mm});
            skLineSegment(sketch, "E424", {"start": v(-15.34, 21.47) * mm, "end": v(-14.48, 21.47) * mm});
            skLineSegment(sketch, "E425", {"start": v(-14.48, 21.47) * mm, "end": v(-11.9, 21.33) * mm});
            skLineSegment(sketch, "E426", {"start": v(-11.9, 21.33) * mm, "end": v(-9.47, 20.98) * mm});
            skLineSegment(sketch, "E427", {"start": v(-9.47, 20.98) * mm, "end": v(-9.04, 20.88) * mm});
            skLineSegment(sketch, "E428", {"start": v(-9.04, 20.88) * mm, "end": v(-8.62, 20.78) * mm});
            skLineSegment(sketch, "E429", {"start": v(-8.62, 20.78) * mm, "end": v(-6.61, 20.06) * mm});
            skLineSegment(sketch, "E430", {"start": v(-6.61, 20.06) * mm, "end": v(-4.78, 19.03) * mm});
            skLineSegment(sketch, "E431", {"start": v(-4.78, 19.03) * mm, "end": v(-4.44, 18.77) * mm});
            skLineSegment(sketch, "E432", {"start": v(-4.44, 18.77) * mm, "end": v(-4.11, 18.52) * mm});
            skLineSegment(sketch, "E433", {"start": v(-4.11, 18.52) * mm, "end": v(-2.71, 17.07) * mm});
            skLineSegment(sketch, "E434", {"start": v(-2.71, 17.07) * mm, "end": v(-1.65, 15.31) * mm});
            skLineSegment(sketch, "E435", {"start": v(-1.65, 15.31) * mm, "end": v(-1.5, 14.92) * mm});
            skLineSegment(sketch, "E436", {"start": v(-1.5, 14.92) * mm, "end": v(-1.33, 14.52) * mm});
            skLineSegment(sketch, "E437", {"start": v(-1.33, 14.52) * mm, "end": v(-0.76, 12.29) * mm});
            skLineSegment(sketch, "E438", {"start": v(-0.76, 12.29) * mm, "end": v(-0.52, 9.93) * mm});
            skLineSegment(sketch, "E439", {"start": v(-0.52, 9.93) * mm, "end": v(-0.52, 9.14) * mm});
            skLineSegment(sketch, "E440", {"start": v(-0.52, 9.14) * mm, "end": v(-0.52, -15.65) * mm});
            skLineSegment(sketch, "E441", {"start": v(-0.52, -15.65) * mm, "end": v(-6.6, -15.65) * mm});
            skLineSegment(sketch, "E442", {"start": v(-6.6, -15.65) * mm, "end": v(-6.6, -11.8) * mm});
            skLineSegment(sketch, "E443", {"start": v(11.02, 33.82) * mm, "end": v(17.14, 33.82) * mm});
            skLineSegment(sketch, "E444", {"start": v(17.14, 33.82) * mm, "end": v(17.14, -16.67) * mm});
            skLineSegment(sketch, "E445", {"start": v(17.14, -16.67) * mm, "end": v(11.02, -16.67) * mm});
            skLineSegment(sketch, "E446", {"start": v(11.02, -16.67) * mm, "end": v(11.02, 33.82) * mm});
            skLineSegment(sketch, "E447", {"start": v(57.11, 21.4) * mm, "end": v(34.24, -34.95) * mm});
            skLineSegment(sketch, "E448", {"start": v(34.24, -34.95) * mm, "end": v(27.74, -34.95) * mm});
            skLineSegment(sketch, "E449", {"start": v(27.74, -34.95) * mm, "end": v(36.92, -12.79) * mm});
            skLineSegment(sketch, "E450", {"start": v(36.92, -12.79) * mm, "end": v(24.42, 21.4) * mm});
            skLineSegment(sketch, "E451", {"start": v(24.42, 21.4) * mm, "end": v(31.01, 21.4) * mm});
            skLineSegment(sketch, "E452", {"start": v(31.01, 21.4) * mm, "end": v(40.23, -5.13) * mm});
            skLineSegment(sketch, "E453", {"start": v(40.23, -5.13) * mm, "end": v(50.77, 21.4) * mm});
            skLineSegment(sketch, "E454", {"start": v(50.77, 21.4) * mm, "end": v(57.11, 21.4) * mm});
            skLineSegment(sketch, "E455", {"start": v(72.17, -16.67) * mm, "end": v(71.3, -16.67) * mm});
            skLineSegment(sketch, "E456", {"start": v(71.3, -16.67) * mm, "end": v(68.66, -16.43) * mm});
            skLineSegment(sketch, "E457", {"start": v(68.66, -16.43) * mm, "end": v(65.9, -15.86) * mm});
            skLineSegment(sketch, "E458", {"start": v(65.9, -15.86) * mm, "end": v(65.38, -15.7) * mm});
            skLineSegment(sketch, "E459", {"start": v(65.38, -15.7) * mm, "end": v(64.85, -15.53) * mm});
            skLineSegment(sketch, "E460", {"start": v(64.85, -15.53) * mm, "end": v(62.47, -14.69) * mm});
            skLineSegment(sketch, "E461", {"start": v(62.47, -14.69) * mm, "end": v(60.46, -13.8) * mm});
            skLineSegment(sketch, "E462", {"start": v(60.46, -13.8) * mm, "end": v(60.12, -13.6) * mm});
            skLineSegment(sketch, "E463", {"start": v(60.12, -13.6) * mm, "end": v(60.12, -6.77) * mm});
            skLineSegment(sketch, "E464", {"start": v(60.12, -6.77) * mm, "end": v(60.46, -6.77) * mm});
            skLineSegment(sketch, "E465", {"start": v(60.46, -6.77) * mm, "end": v(60.59, -6.87) * mm});
            skLineSegment(sketch, "E466", {"start": v(60.59, -6.87) * mm, "end": v(62.12, -8) * mm});
            skLineSegment(sketch, "E467", {"start": v(62.12, -8) * mm, "end": v(62.3, -8.13) * mm});
            skLineSegment(sketch, "E468", {"start": v(62.3, -8.13) * mm, "end": v(62.47, -8.25) * mm});
            skLineSegment(sketch, "E469", {"start": v(62.47, -8.25) * mm, "end": v(63.52, -8.9) * mm});
            skLineSegment(sketch, "E470", {"start": v(63.52, -8.9) * mm, "end": v(64.8, -9.55) * mm});
            skLineSegment(sketch, "E471", {"start": v(64.8, -9.55) * mm, "end": v(65.08, -9.7) * mm});
            skLineSegment(sketch, "E472", {"start": v(65.08, -9.7) * mm, "end": v(65.34, -9.8) * mm});
            skLineSegment(sketch, "E473", {"start": v(65.34, -9.8) * mm, "end": v(68.2, -10.87) * mm});
            skLineSegment(sketch, "E474", {"start": v(68.2, -10.87) * mm, "end": v(68.5, -10.96) * mm});
            skLineSegment(sketch, "E475", {"start": v(68.5, -10.96) * mm, "end": v(68.81, -11.05) * mm});
            skLineSegment(sketch, "E476", {"start": v(68.81, -11.05) * mm, "end": v(70.4, -11.37) * mm});
            skLineSegment(sketch, "E477", {"start": v(70.4, -11.37) * mm, "end": v(71.9, -11.5) * mm});
            skLineSegment(sketch, "E478", {"start": v(71.9, -11.5) * mm, "end": v(72.4, -11.5) * mm});
            skLineSegment(sketch, "E479", {"start": v(72.4, -11.5) * mm, "end": v(73.18, -11.5) * mm});
            skLineSegment(sketch, "E480", {"start": v(73.18, -11.5) * mm, "end": v(75.23, -11.22) * mm});
            skLineSegment(sketch, "E481", {"start": v(75.23, -11.22) * mm, "end": v(75.5, -11.16) * mm});
            skLineSegment(sketch, "E482", {"start": v(75.5, -11.16) * mm, "end": v(75.78, -11.1) * mm});
            skLineSegment(sketch, "E483", {"start": v(75.78, -11.1) * mm, "end": v(76.95, -10.77) * mm});
            skLineSegment(sketch, "E484", {"start": v(76.95, -10.77) * mm, "end": v(77.84, -10.38) * mm});
            skLineSegment(sketch, "E485", {"start": v(77.84, -10.38) * mm, "end": v(77.98, -10.3) * mm});
            skLineSegment(sketch, "E486", {"start": v(77.98, -10.3) * mm, "end": v(78.16, -10.18) * mm});
            skLineSegment(sketch, "E487", {"start": v(78.16, -10.18) * mm, "end": v(78.94, -9.53) * mm});
            skLineSegment(sketch, "E488", {"start": v(78.94, -9.53) * mm, "end": v(79.52, -8.86) * mm});
            skLineSegment(sketch, "E489", {"start": v(79.52, -8.86) * mm, "end": v(79.6, -8.72) * mm});
            skLineSegment(sketch, "E490", {"start": v(79.6, -8.72) * mm, "end": v(79.7, -8.57) * mm});
            skLineSegment(sketch, "E491", {"start": v(79.7, -8.57) * mm, "end": v(79.98, -7.66) * mm});
            skLineSegment(sketch, "E492", {"start": v(79.98, -7.66) * mm, "end": v(80.1, -6.55) * mm});
            skLineSegment(sketch, "E493", {"start": v(80.1, -6.55) * mm, "end": v(80.1, -6.18) * mm});
            skLineSegment(sketch, "E494", {"start": v(80.1, -6.18) * mm, "end": v(80.1, -5.7) * mm});
            skLineSegment(sketch, "E495", {"start": v(80.1, -5.7) * mm, "end": v(79.81, -4.27) * mm});
            skLineSegment(sketch, "E496", {"start": v(79.81, -4.27) * mm, "end": v(79.12, -3.1) * mm});
            skLineSegment(sketch, "E497", {"start": v(79.12, -3.1) * mm, "end": v(78.93, -2.91) * mm});
            skLineSegment(sketch, "E498", {"start": v(78.93, -2.91) * mm, "end": v(78.73, -2.73) * mm});
            skLineSegment(sketch, "E499", {"start": v(78.73, -2.73) * mm, "end": v(77.29, -1.9) * mm});
            skLineSegment(sketch, "E500", {"start": v(77.29, -1.9) * mm, "end": v(75.24, -1.18) * mm});
            skLineSegment(sketch, "E501", {"start": v(75.24, -1.18) * mm, "end": v(74.73, -1.06) * mm});
            skLineSegment(sketch, "E502", {"start": v(74.73, -1.06) * mm, "end": v(74.54, -1) * mm});
            skLineSegment(sketch, "E503", {"start": v(74.54, -1) * mm, "end": v(73.37, -0.73) * mm});
            skLineSegment(sketch, "E504", {"start": v(73.37, -0.73) * mm, "end": v(71.99, -0.44) * mm});
            skLineSegment(sketch, "E505", {"start": v(71.99, -0.44) * mm, "end": v(71.68, -0.38) * mm});
            skLineSegment(sketch, "E506", {"start": v(71.68, -0.38) * mm, "end": v(71.36, -0.3) * mm});
            skLineSegment(sketch, "E507", {"start": v(71.36, -0.3) * mm, "end": v(68.47, 0.39) * mm});
            skLineSegment(sketch, "E508", {"start": v(68.47, 0.39) * mm, "end": v(68.2, 0.46) * mm});
            skLineSegment(sketch, "E509", {"start": v(68.2, 0.46) * mm, "end": v(67.52, 0.67) * mm});
            skLineSegment(sketch, "E510", {"start": v(67.52, 0.67) * mm, "end": v(64.62, 2) * mm});
            skLineSegment(sketch, "E511", {"start": v(64.62, 2) * mm, "end": v(62.5, 3.76) * mm});
            skLineSegment(sketch, "E512", {"start": v(62.5, 3.76) * mm, "end": v(62.18, 4.18) * mm});
            skLineSegment(sketch, "E513", {"start": v(62.18, 4.18) * mm, "end": v(61.86, 4.6) * mm});
            skLineSegment(sketch, "E514", {"start": v(61.86, 4.6) * mm, "end": v(60.75, 6.96) * mm});
            skLineSegment(sketch, "E515", {"start": v(60.75, 6.96) * mm, "end": v(60.28, 9.45) * mm});
            skLineSegment(sketch, "E516", {"start": v(60.28, 9.45) * mm, "end": v(60.28, 10.27) * mm});
            skLineSegment(sketch, "E517", {"start": v(60.28, 10.27) * mm, "end": v(60.28, 11.39) * mm});
            skLineSegment(sketch, "E518", {"start": v(60.28, 11.39) * mm, "end": v(61.2, 14.71) * mm});
            skLineSegment(sketch, "E519", {"start": v(61.2, 14.71) * mm, "end": v(63.38, 17.73) * mm});
            skLineSegment(sketch, "E520", {"start": v(63.38, 17.73) * mm, "end": v(64, 18.25) * mm});
            skLineSegment(sketch, "E521", {"start": v(64, 18.25) * mm, "end": v(64.45, 18.64) * mm});
            skLineSegment(sketch, "E522", {"start": v(64.45, 18.64) * mm, "end": v(66, 19.6) * mm});
            skLineSegment(sketch, "E523", {"start": v(66, 19.6) * mm, "end": v(68.3, 20.56) * mm});
            skLineSegment(sketch, "E524", {"start": v(68.3, 20.56) * mm, "end": v(70.9, 21.14) * mm});
            skLineSegment(sketch, "E525", {"start": v(70.9, 21.14) * mm, "end": v(73.1, 21.33) * mm});
            skLineSegment(sketch, "E526", {"start": v(73.1, 21.33) * mm, "end": v(73.83, 21.33) * mm});
            skLineSegment(sketch, "E527", {"start": v(73.83, 21.33) * mm, "end": v(75.34, 21.33) * mm});
            skLineSegment(sketch, "E528", {"start": v(75.34, 21.33) * mm, "end": v(79.38, 20.7) * mm});
            skLineSegment(sketch, "E529", {"start": v(79.38, 20.7) * mm, "end": v(79.88, 20.58) * mm});
            skLineSegment(sketch, "E530", {"start": v(79.88, 20.58) * mm, "end": v(80.39, 20.46) * mm});
            skLineSegment(sketch, "E531", {"start": v(80.39, 20.46) * mm, "end": v(82.7, 19.75) * mm});
            skLineSegment(sketch, "E532", {"start": v(82.7, 19.75) * mm, "end": v(84.68, 18.9) * mm});
            skLineSegment(sketch, "E533", {"start": v(84.68, 18.9) * mm, "end": v(85.02, 18.7) * mm});
            skLineSegment(sketch, "E534", {"start": v(85.02, 18.7) * mm, "end": v(85.02, 12.18) * mm});
            skLineSegment(sketch, "E535", {"start": v(85.02, 12.18) * mm, "end": v(84.68, 12.18) * mm});
            skLineSegment(sketch, "E536", {"start": v(84.68, 12.18) * mm, "end": v(84.3, 12.49) * mm});
            skLineSegment(sketch, "E537", {"start": v(84.3, 12.49) * mm, "end": v(82.22, 13.84) * mm});
            skLineSegment(sketch, "E538", {"start": v(82.22, 13.84) * mm, "end": v(79.97, 14.92) * mm});
            skLineSegment(sketch, "E539", {"start": v(79.97, 14.92) * mm, "end": v(79.5, 15.1) * mm});
            skLineSegment(sketch, "E540", {"start": v(79.5, 15.1) * mm, "end": v(79.01, 15.28) * mm});
            skLineSegment(sketch, "E541", {"start": v(79.01, 15.28) * mm, "end": v(75.02, 16.17) * mm});
            skLineSegment(sketch, "E542", {"start": v(75.02, 16.17) * mm, "end": v(73.7, 16.17) * mm});
            skLineSegment(sketch, "E543", {"start": v(73.7, 16.17) * mm, "end": v(73, 16.17) * mm});
            skLineSegment(sketch, "E544", {"start": v(73, 16.17) * mm, "end": v(70.9, 15.86) * mm});
            skLineSegment(sketch, "E545", {"start": v(70.9, 15.86) * mm, "end": v(68.94, 15.13) * mm});
            skLineSegment(sketch, "E546", {"start": v(68.94, 15.13) * mm, "end": v(68.6, 14.92) * mm});
            skLineSegment(sketch, "E547", {"start": v(68.6, 14.92) * mm, "end": v(68.35, 14.77) * mm});
            skLineSegment(sketch, "E548", {"start": v(68.35, 14.77) * mm, "end": v(67.68, 14.2) * mm});
            skLineSegment(sketch, "E549", {"start": v(67.68, 14.2) * mm, "end": v(67.03, 13.32) * mm});
            skLineSegment(sketch, "E550", {"start": v(67.03, 13.32) * mm, "end": v(66.64, 12.28) * mm});
            skLineSegment(sketch, "E551", {"start": v(66.64, 12.28) * mm, "end": v(66.51, 11.39) * mm});
            skLineSegment(sketch, "E552", {"start": v(66.51, 11.39) * mm, "end": v(66.51, 11.09) * mm});
            skLineSegment(sketch, "E553", {"start": v(66.51, 11.09) * mm, "end": v(66.51, 10.6) * mm});
            skLineSegment(sketch, "E554", {"start": v(66.51, 10.6) * mm, "end": v(66.83, 9.1) * mm});
            skLineSegment(sketch, "E555", {"start": v(66.83, 9.1) * mm, "end": v(67.55, 7.88) * mm});
            skLineSegment(sketch, "E556", {"start": v(67.55, 7.88) * mm, "end": v(67.76, 7.7) * mm});
            skLineSegment(sketch, "E557", {"start": v(67.76, 7.7) * mm, "end": v(67.96, 7.5) * mm});
            skLineSegment(sketch, "E558", {"start": v(67.96, 7.5) * mm, "end": v(69.36, 6.67) * mm});
            skLineSegment(sketch, "E559", {"start": v(69.36, 6.67) * mm, "end": v(71.26, 5.97) * mm});
            skLineSegment(sketch, "E560", {"start": v(71.26, 5.97) * mm, "end": v(71.72, 5.85) * mm});
            skLineSegment(sketch, "E561", {"start": v(71.72, 5.85) * mm, "end": v(71.95, 5.8) * mm});
            skLineSegment(sketch, "E562", {"start": v(71.95, 5.8) * mm, "end": v(74.46, 5.2) * mm});
            skLineSegment(sketch, "E563", {"start": v(74.46, 5.2) * mm, "end": v(74.73, 5.15) * mm});
            skLineSegment(sketch, "E564", {"start": v(74.73, 5.15) * mm, "end": v(75.02, 5.1) * mm});
            skLineSegment(sketch, "E565", {"start": v(75.02, 5.1) * mm, "end": v(77.96, 4.44) * mm});
            skLineSegment(sketch, "E566", {"start": v(77.96, 4.44) * mm, "end": v(78.27, 4.36) * mm});
            skLineSegment(sketch, "E567", {"start": v(78.27, 4.36) * mm, "end": v(78.94, 4.2) * mm});
            skLineSegment(sketch, "E568", {"start": v(78.94, 4.2) * mm, "end": v(81.79, 3.02) * mm});
            skLineSegment(sketch, "E569", {"start": v(81.79, 3.02) * mm, "end": v(83.98, 1.41) * mm});
            skLineSegment(sketch, "E570", {"start": v(83.98, 1.41) * mm, "end": v(84.32, 1.03) * mm});
            skLineSegment(sketch, "E571", {"start": v(84.32, 1.03) * mm, "end": v(84.66, 0.64) * mm});
            skLineSegment(sketch, "E572", {"start": v(84.66, 0.64) * mm, "end": v(85.84, -1.74) * mm});
            skLineSegment(sketch, "E573", {"start": v(85.84, -1.74) * mm, "end": v(86.34, -4.44) * mm});
            skLineSegment(sketch, "E574", {"start": v(86.34, -4.44) * mm, "end": v(86.34, -5.34) * mm});
            skLineSegment(sketch, "E575", {"start": v(86.34, -5.34) * mm, "end": v(86.34, -5.9) * mm});
            skLineSegment(sketch, "E576", {"start": v(86.34, -5.9) * mm, "end": v(86.11, -7.62) * mm});
            skLineSegment(sketch, "E577", {"start": v(86.11, -7.62) * mm, "end": v(85.58, -9.41) * mm});
            skLineSegment(sketch, "E578", {"start": v(85.58, -9.41) * mm, "end": v(85.43, -9.76) * mm});
            skLineSegment(sketch, "E579", {"start": v(85.43, -9.76) * mm, "end": v(85.27, -10.1) * mm});
            skLineSegment(sketch, "E580", {"start": v(85.27, -10.1) * mm, "end": v(84.28, -11.71) * mm});
            skLineSegment(sketch, "E581", {"start": v(84.28, -11.71) * mm, "end": v(83.01, -13.11) * mm});
            skLineSegment(sketch, "E582", {"start": v(83.01, -13.11) * mm, "end": v(82.71, -13.36) * mm});
            skLineSegment(sketch, "E583", {"start": v(82.71, -13.36) * mm, "end": v(82.39, -13.63) * mm});
            skLineSegment(sketch, "E584", {"start": v(82.39, -13.63) * mm, "end": v(80.64, -14.78) * mm});
            skLineSegment(sketch, "E585", {"start": v(80.64, -14.78) * mm, "end": v(78.72, -15.69) * mm});
            skLineSegment(sketch, "E586", {"start": v(78.72, -15.69) * mm, "end": v(78.32, -15.83) * mm});
            skLineSegment(sketch, "E587", {"start": v(78.32, -15.83) * mm, "end": v(77.9, -15.97) * mm});
            skLineSegment(sketch, "E588", {"start": v(77.9, -15.97) * mm, "end": v(75.55, -16.45) * mm});
            skLineSegment(sketch, "E589", {"start": v(75.55, -16.45) * mm, "end": v(73.02, -16.67) * mm});
            skLineSegment(sketch, "E590", {"start": v(73.02, -16.67) * mm, "end": v(72.17, -16.67) * mm});
            skLineSegment(sketch, "E591", {"start": v(108.3, -16.67) * mm, "end": v(107.19, -16.67) * mm});
            skLineSegment(sketch, "E592", {"start": v(107.19, -16.67) * mm, "end": v(103.85, -15.95) * mm});
            skLineSegment(sketch, "E593", {"start": v(103.85, -15.95) * mm, "end": v(100.99, -14.3) * mm});
            skLineSegment(sketch, "E594", {"start": v(100.99, -14.3) * mm, "end": v(100.52, -13.81) * mm});
            skLineSegment(sketch, "E595", {"start": v(100.52, -13.81) * mm, "end": v(100.16, -13.46) * mm});
            skLineSegment(sketch, "E596", {"start": v(100.16, -13.46) * mm, "end": v(99.29, -12.2) * mm});
            skLineSegment(sketch, "E597", {"start": v(99.29, -12.2) * mm, "end": v(98.41, -10.16) * mm});
            skLineSegment(sketch, "E598", {"start": v(98.41, -10.16) * mm, "end": v(97.89, -7.7) * mm});
            skLineSegment(sketch, "E599", {"start": v(97.89, -7.7) * mm, "end": v(97.71, -5.56) * mm});
            skLineSegment(sketch, "E600", {"start": v(97.71, -5.56) * mm, "end": v(97.71, -4.84) * mm});
            skLineSegment(sketch, "E601", {"start": v(97.71, -4.84) * mm, "end": v(97.71, 15.24) * mm});
            skLineSegment(sketch, "E602", {"start": v(97.71, 15.24) * mm, "end": v(93.61, 15.24) * mm});
            skLineSegment(sketch, "E603", {"start": v(93.61, 15.24) * mm, "end": v(93.61, 20.3) * mm});
            skLineSegment(sketch, "E604", {"start": v(93.61, 20.3) * mm, "end": v(97.71, 20.3) * mm});
            skLineSegment(sketch, "E605", {"start": v(97.71, 20.3) * mm, "end": v(97.71, 30.71) * mm});
            skLineSegment(sketch, "E606", {"start": v(97.71, 30.71) * mm, "end": v(103.83, 30.71) * mm});
            skLineSegment(sketch, "E607", {"start": v(103.83, 30.71) * mm, "end": v(103.83, 20.3) * mm});
            skLineSegment(sketch, "E608", {"start": v(103.83, 20.3) * mm, "end": v(113.98, 20.3) * mm});
            skLineSegment(sketch, "E609", {"start": v(113.98, 20.3) * mm, "end": v(113.98, 15.24) * mm});
            skLineSegment(sketch, "E610", {"start": v(113.98, 15.24) * mm, "end": v(103.83, 15.24) * mm});
            skLineSegment(sketch, "E611", {"start": v(103.83, 15.24) * mm, "end": v(103.83, -1.98) * mm});
            skLineSegment(sketch, "E612", {"start": v(103.83, -1.98) * mm, "end": v(103.83, -2.6) * mm});
            skLineSegment(sketch, "E613", {"start": v(103.83, -2.6) * mm, "end": v(103.85, -4.43) * mm});
            skLineSegment(sketch, "E614", {"start": v(103.85, -4.43) * mm, "end": v(103.9, -6) * mm});
            skLineSegment(sketch, "E615", {"start": v(103.9, -6) * mm, "end": v(103.92, -6.25) * mm});
            skLineSegment(sketch, "E616", {"start": v(103.92, -6.25) * mm, "end": v(103.94, -6.5) * mm});
            skLineSegment(sketch, "E617", {"start": v(103.94, -6.5) * mm, "end": v(104.16, -7.69) * mm});
            skLineSegment(sketch, "E618", {"start": v(104.16, -7.69) * mm, "end": v(104.56, -8.82) * mm});
            skLineSegment(sketch, "E619", {"start": v(104.56, -8.82) * mm, "end": v(104.67, -9.03) * mm});
            skLineSegment(sketch, "E620", {"start": v(104.67, -9.03) * mm, "end": v(104.76, -9.22) * mm});
            skLineSegment(sketch, "E621", {"start": v(104.76, -9.22) * mm, "end": v(105.38, -10.03) * mm});
            skLineSegment(sketch, "E622", {"start": v(105.38, -10.03) * mm, "end": v(106.25, -10.64) * mm});
            skLineSegment(sketch, "E623", {"start": v(106.25, -10.64) * mm, "end": v(106.46, -10.73) * mm});
            skLineSegment(sketch, "E624", {"start": v(106.46, -10.73) * mm, "end": v(106.66, -10.83) * mm});
            skLineSegment(sketch, "E625", {"start": v(106.66, -10.83) * mm, "end": v(107.9, -11.16) * mm});
            skLineSegment(sketch, "E626", {"start": v(107.9, -11.16) * mm, "end": v(109.32, -11.3) * mm});
            skLineSegment(sketch, "E627", {"start": v(109.32, -11.3) * mm, "end": v(109.8, -11.3) * mm});
            skLineSegment(sketch, "E628", {"start": v(109.8, -11.3) * mm, "end": v(110.51, -11.3) * mm});
            skLineSegment(sketch, "E629", {"start": v(110.51, -11.3) * mm, "end": v(112.46, -10.94) * mm});
            skLineSegment(sketch, "E630", {"start": v(112.46, -10.94) * mm, "end": v(112.7, -10.87) * mm});
            skLineSegment(sketch, "E631", {"start": v(112.7, -10.87) * mm, "end": v(112.92, -10.8) * mm});
            skLineSegment(sketch, "E632", {"start": v(112.92, -10.8) * mm, "end": v(113.88, -10.46) * mm});
            skLineSegment(sketch, "E633", {"start": v(113.88, -10.46) * mm, "end": v(114.58, -10.19) * mm});
            skLineSegment(sketch, "E634", {"start": v(114.58, -10.19) * mm, "end": v(114.68, -10.14) * mm});
            skLineSegment(sketch, "E635", {"start": v(114.68, -10.14) * mm, "end": v(115.05, -10.14) * mm});
            skLineSegment(sketch, "E636", {"start": v(115.05, -10.14) * mm, "end": v(115.05, -15.63) * mm});
            skLineSegment(sketch, "E637", {"start": v(115.05, -15.63) * mm, "end": v(114.76, -15.7) * mm});
            skLineSegment(sketch, "E638", {"start": v(114.76, -15.7) * mm, "end": v(111.85, -16.33) * mm});
            skLineSegment(sketch, "E639", {"start": v(111.85, -16.33) * mm, "end": v(111.56, -16.38) * mm});
            skLineSegment(sketch, "E640", {"start": v(111.56, -16.38) * mm, "end": v(111.26, -16.43) * mm});
            skLineSegment(sketch, "E641", {"start": v(111.26, -16.43) * mm, "end": v(109.04, -16.67) * mm});
            skLineSegment(sketch, "E642", {"start": v(109.04, -16.67) * mm, "end": v(108.3, -16.67) * mm});
            skLineSegment(sketch, "E643", {"start": v(132.44, -16.67) * mm, "end": v(131.56, -16.67) * mm});
            skLineSegment(sketch, "E644", {"start": v(131.56, -16.67) * mm, "end": v(128.92, -16.43) * mm});
            skLineSegment(sketch, "E645", {"start": v(128.92, -16.43) * mm, "end": v(126.17, -15.86) * mm});
            skLineSegment(sketch, "E646", {"start": v(126.17, -15.86) * mm, "end": v(125.65, -15.7) * mm});
            skLineSegment(sketch, "E647", {"start": v(125.65, -15.7) * mm, "end": v(125.12, -15.53) * mm});
            skLineSegment(sketch, "E648", {"start": v(125.12, -15.53) * mm, "end": v(122.75, -14.69) * mm});
            skLineSegment(sketch, "E649", {"start": v(122.75, -14.69) * mm, "end": v(120.75, -13.8) * mm});
            skLineSegment(sketch, "E650", {"start": v(120.75, -13.8) * mm, "end": v(120.4, -13.6) * mm});
            skLineSegment(sketch, "E651", {"start": v(120.4, -13.6) * mm, "end": v(120.4, -6.77) * mm});
            skLineSegment(sketch, "E652", {"start": v(120.4, -6.77) * mm, "end": v(120.73, -6.77) * mm});
            skLineSegment(sketch, "E653", {"start": v(120.73, -6.77) * mm, "end": v(120.86, -6.87) * mm});
            skLineSegment(sketch, "E654", {"start": v(120.86, -6.87) * mm, "end": v(122.38, -8) * mm});
            skLineSegment(sketch, "E655", {"start": v(122.38, -8) * mm, "end": v(122.56, -8.13) * mm});
            skLineSegment(sketch, "E656", {"start": v(122.56, -8.13) * mm, "end": v(122.73, -8.25) * mm});
            skLineSegment(sketch, "E657", {"start": v(122.73, -8.25) * mm, "end": v(123.79, -8.9) * mm});
            skLineSegment(sketch, "E658", {"start": v(123.79, -8.9) * mm, "end": v(125.08, -9.55) * mm});
            skLineSegment(sketch, "E659", {"start": v(125.08, -9.55) * mm, "end": v(125.37, -9.7) * mm});
            skLineSegment(sketch, "E660", {"start": v(125.37, -9.7) * mm, "end": v(125.63, -9.8) * mm});
            skLineSegment(sketch, "E661", {"start": v(125.63, -9.8) * mm, "end": v(128.48, -10.87) * mm});
            skLineSegment(sketch, "E662", {"start": v(128.48, -10.87) * mm, "end": v(128.8, -10.96) * mm});
            skLineSegment(sketch, "E663", {"start": v(128.8, -10.96) * mm, "end": v(129.1, -11.05) * mm});
            skLineSegment(sketch, "E664", {"start": v(129.1, -11.05) * mm, "end": v(131.78, -11.5) * mm});
            skLineSegment(sketch, "E665", {"start": v(131.78, -11.5) * mm, "end": v(132.67, -11.5) * mm});
            skLineSegment(sketch, "E666", {"start": v(132.67, -11.5) * mm, "end": v(133.45, -11.5) * mm});
            skLineSegment(sketch, "E667", {"start": v(133.45, -11.5) * mm, "end": v(135.52, -11.22) * mm});
            skLineSegment(sketch, "E668", {"start": v(135.52, -11.22) * mm, "end": v(135.8, -11.16) * mm});
            skLineSegment(sketch, "E669", {"start": v(135.8, -11.16) * mm, "end": v(136.07, -11.1) * mm});
            skLineSegment(sketch, "E670", {"start": v(136.07, -11.1) * mm, "end": v(137.23, -10.77) * mm});
            skLineSegment(sketch, "E671", {"start": v(137.23, -10.77) * mm, "end": v(138.11, -10.38) * mm});
            skLineSegment(sketch, "E672", {"start": v(138.11, -10.38) * mm, "end": v(138.24, -10.3) * mm});
            skLineSegment(sketch, "E673", {"start": v(138.24, -10.3) * mm, "end": v(138.43, -10.18) * mm});
            skLineSegment(sketch, "E674", {"start": v(138.43, -10.18) * mm, "end": v(139.23, -9.53) * mm});
            skLineSegment(sketch, "E675", {"start": v(139.23, -9.53) * mm, "end": v(139.81, -8.86) * mm});
            skLineSegment(sketch, "E676", {"start": v(139.81, -8.86) * mm, "end": v(139.9, -8.72) * mm});
            skLineSegment(sketch, "E677", {"start": v(139.9, -8.72) * mm, "end": v(139.98, -8.57) * mm});
            skLineSegment(sketch, "E678", {"start": v(139.98, -8.57) * mm, "end": v(140.27, -7.66) * mm});
            skLineSegment(sketch, "E679", {"start": v(140.27, -7.66) * mm, "end": v(140.4, -6.55) * mm});
            skLineSegment(sketch, "E680", {"start": v(140.4, -6.55) * mm, "end": v(140.4, -6.18) * mm});
            skLineSegment(sketch, "E681", {"start": v(140.4, -6.18) * mm, "end": v(140.4, -5.7) * mm});
            skLineSegment(sketch, "E682", {"start": v(140.4, -5.7) * mm, "end": v(140.1, -4.27) * mm});
            skLineSegment(sketch, "E683", {"start": v(140.1, -4.27) * mm, "end": v(139.4, -3.1) * mm});
            skLineSegment(sketch, "E684", {"start": v(139.4, -3.1) * mm, "end": v(139.22, -2.91) * mm});
            skLineSegment(sketch, "E685", {"start": v(139.22, -2.91) * mm, "end": v(139.02, -2.73) * mm});
            skLineSegment(sketch, "E686", {"start": v(139.02, -2.73) * mm, "end": v(137.57, -1.9) * mm});
            skLineSegment(sketch, "E687", {"start": v(137.57, -1.9) * mm, "end": v(135.5, -1.18) * mm});
            skLineSegment(sketch, "E688", {"start": v(135.5, -1.18) * mm, "end": v(135, -1.06) * mm});
            skLineSegment(sketch, "E689", {"start": v(135, -1.06) * mm, "end": v(134.81, -1) * mm});
            skLineSegment(sketch, "E690", {"start": v(134.81, -1) * mm, "end": v(133.66, -0.73) * mm});
            skLineSegment(sketch, "E691", {"start": v(133.66, -0.73) * mm, "end": v(132.28, -0.44) * mm});
            skLineSegment(sketch, "E692", {"start": v(132.28, -0.44) * mm, "end": v(131.97, -0.38) * mm});
            skLineSegment(sketch, "E693", {"start": v(131.97, -0.38) * mm, "end": v(131.65, -0.3) * mm});
            skLineSegment(sketch, "E694", {"start": v(131.65, -0.3) * mm, "end": v(128.74, 0.39) * mm});
            skLineSegment(sketch, "E695", {"start": v(128.74, 0.39) * mm, "end": v(128.48, 0.46) * mm});
            skLineSegment(sketch, "E696", {"start": v(128.48, 0.46) * mm, "end": v(127.78, 0.67) * mm});
            skLineSegment(sketch, "E697", {"start": v(127.78, 0.67) * mm, "end": v(124.9, 2) * mm});
            skLineSegment(sketch, "E698", {"start": v(124.9, 2) * mm, "end": v(122.76, 3.76) * mm});
            skLineSegment(sketch, "E699", {"start": v(122.76, 3.76) * mm, "end": v(122.45, 4.18) * mm});
            skLineSegment(sketch, "E700", {"start": v(122.45, 4.18) * mm, "end": v(122.14, 4.6) * mm});
            skLineSegment(sketch, "E701", {"start": v(122.14, 4.6) * mm, "end": v(121.04, 6.96) * mm});
            skLineSegment(sketch, "E702", {"start": v(121.04, 6.96) * mm, "end": v(120.57, 9.45) * mm});
            skLineSegment(sketch, "E703", {"start": v(120.57, 9.45) * mm, "end": v(120.57, 10.27) * mm});
            skLineSegment(sketch, "E704", {"start": v(120.57, 10.27) * mm, "end": v(120.57, 11.39) * mm});
            skLineSegment(sketch, "E705", {"start": v(120.57, 11.39) * mm, "end": v(121.49, 14.71) * mm});
            skLineSegment(sketch, "E706", {"start": v(121.49, 14.71) * mm, "end": v(123.64, 17.73) * mm});
            skLineSegment(sketch, "E707", {"start": v(123.64, 17.73) * mm, "end": v(124.26, 18.25) * mm});
            skLineSegment(sketch, "E708", {"start": v(124.26, 18.25) * mm, "end": v(124.88, 18.77) * mm});
            skLineSegment(sketch, "E709", {"start": v(124.88, 18.77) * mm, "end": v(128.57, 20.56) * mm});
            skLineSegment(sketch, "E710", {"start": v(128.57, 20.56) * mm, "end": v(132.71, 21.33) * mm});
            skLineSegment(sketch, "E711", {"start": v(132.71, 21.33) * mm, "end": v(134.1, 21.33) * mm});
            skLineSegment(sketch, "E712", {"start": v(134.1, 21.33) * mm, "end": v(135.61, 21.33) * mm});
            skLineSegment(sketch, "E713", {"start": v(135.61, 21.33) * mm, "end": v(139.66, 20.7) * mm});
            skLineSegment(sketch, "E714", {"start": v(139.66, 20.7) * mm, "end": v(140.17, 20.58) * mm});
            skLineSegment(sketch, "E715", {"start": v(140.17, 20.58) * mm, "end": v(140.68, 20.46) * mm});
            skLineSegment(sketch, "E716", {"start": v(140.68, 20.46) * mm, "end": v(142.97, 19.75) * mm});
            skLineSegment(sketch, "E717", {"start": v(142.97, 19.75) * mm, "end": v(144.94, 18.9) * mm});
            skLineSegment(sketch, "E718", {"start": v(144.94, 18.9) * mm, "end": v(145.3, 18.7) * mm});
            skLineSegment(sketch, "E719", {"start": v(145.3, 18.7) * mm, "end": v(145.3, 12.18) * mm});
            skLineSegment(sketch, "E720", {"start": v(145.3, 12.18) * mm, "end": v(144.97, 12.18) * mm});
            skLineSegment(sketch, "E721", {"start": v(144.97, 12.18) * mm, "end": v(144.58, 12.49) * mm});
            skLineSegment(sketch, "E722", {"start": v(144.58, 12.49) * mm, "end": v(142.5, 13.84) * mm});
            skLineSegment(sketch, "E723", {"start": v(142.5, 13.84) * mm, "end": v(140.24, 14.92) * mm});
            skLineSegment(sketch, "E724", {"start": v(140.24, 14.92) * mm, "end": v(139.76, 15.1) * mm});
            skLineSegment(sketch, "E725", {"start": v(139.76, 15.1) * mm, "end": v(139.28, 15.28) * mm});
            skLineSegment(sketch, "E726", {"start": v(139.28, 15.28) * mm, "end": v(135.3, 16.17) * mm});
            skLineSegment(sketch, "E727", {"start": v(135.3, 16.17) * mm, "end": v(133.96, 16.17) * mm});
            skLineSegment(sketch, "E728", {"start": v(133.96, 16.17) * mm, "end": v(133.27, 16.17) * mm});
            skLineSegment(sketch, "E729", {"start": v(133.27, 16.17) * mm, "end": v(131.2, 15.86) * mm});
            skLineSegment(sketch, "E730", {"start": v(131.2, 15.86) * mm, "end": v(129.23, 15.13) * mm});
            skLineSegment(sketch, "E731", {"start": v(129.23, 15.13) * mm, "end": v(128.88, 14.92) * mm});
            skLineSegment(sketch, "E732", {"start": v(128.88, 14.92) * mm, "end": v(128.64, 14.77) * mm});
            skLineSegment(sketch, "E733", {"start": v(128.64, 14.77) * mm, "end": v(127.96, 14.2) * mm});
            skLineSegment(sketch, "E734", {"start": v(127.96, 14.2) * mm, "end": v(127.31, 13.32) * mm});
            skLineSegment(sketch, "E735", {"start": v(127.31, 13.32) * mm, "end": v(126.93, 12.28) * mm});
            skLineSegment(sketch, "E736", {"start": v(126.93, 12.28) * mm, "end": v(126.8, 11.39) * mm});
            skLineSegment(sketch, "E737", {"start": v(126.8, 11.39) * mm, "end": v(126.8, 11.09) * mm});
            skLineSegment(sketch, "E738", {"start": v(126.8, 11.09) * mm, "end": v(126.8, 10.6) * mm});
            skLineSegment(sketch, "E739", {"start": v(126.8, 10.6) * mm, "end": v(127.1, 9.1) * mm});
            skLineSegment(sketch, "E740", {"start": v(127.1, 9.1) * mm, "end": v(127.82, 7.88) * mm});
            skLineSegment(sketch, "E741", {"start": v(127.82, 7.88) * mm, "end": v(128.02, 7.7) * mm});
            skLineSegment(sketch, "E742", {"start": v(128.02, 7.7) * mm, "end": v(128.23, 7.5) * mm});
            skLineSegment(sketch, "E743", {"start": v(128.23, 7.5) * mm, "end": v(129.64, 6.67) * mm});
            skLineSegment(sketch, "E744", {"start": v(129.64, 6.67) * mm, "end": v(131.53, 5.97) * mm});
            skLineSegment(sketch, "E745", {"start": v(131.53, 5.97) * mm, "end": v(131.99, 5.85) * mm});
            skLineSegment(sketch, "E746", {"start": v(131.99, 5.85) * mm, "end": v(132.21, 5.8) * mm});
            skLineSegment(sketch, "E747", {"start": v(132.21, 5.8) * mm, "end": v(134.75, 5.2) * mm});
            skLineSegment(sketch, "E748", {"start": v(134.75, 5.2) * mm, "end": v(135.02, 5.15) * mm});
            skLineSegment(sketch, "E749", {"start": v(135.02, 5.15) * mm, "end": v(135.3, 5.1) * mm});
            skLineSegment(sketch, "E750", {"start": v(135.3, 5.1) * mm, "end": v(138.23, 4.44) * mm});
            skLineSegment(sketch, "E751", {"start": v(138.23, 4.44) * mm, "end": v(138.54, 4.36) * mm});
            skLineSegment(sketch, "E752", {"start": v(138.54, 4.36) * mm, "end": v(139.21, 4.2) * mm});
            skLineSegment(sketch, "E753", {"start": v(139.21, 4.2) * mm, "end": v(142.07, 3.02) * mm});
            skLineSegment(sketch, "E754", {"start": v(142.07, 3.02) * mm, "end": v(144.25, 1.41) * mm});
            skLineSegment(sketch, "E755", {"start": v(144.25, 1.41) * mm, "end": v(144.59, 1.03) * mm});
            skLineSegment(sketch, "E756", {"start": v(144.59, 1.03) * mm, "end": v(144.93, 0.64) * mm});
            skLineSegment(sketch, "E757", {"start": v(144.93, 0.64) * mm, "end": v(146.12, -1.74) * mm});
            skLineSegment(sketch, "E758", {"start": v(146.12, -1.74) * mm, "end": v(146.63, -4.44) * mm});
            skLineSegment(sketch, "E759", {"start": v(146.63, -4.44) * mm, "end": v(146.63, -5.34) * mm});
            skLineSegment(sketch, "E760", {"start": v(146.63, -5.34) * mm, "end": v(146.63, -5.9) * mm});
            skLineSegment(sketch, "E761", {"start": v(146.63, -5.9) * mm, "end": v(146.39, -7.62) * mm});
            skLineSegment(sketch, "E762", {"start": v(146.39, -7.62) * mm, "end": v(145.85, -9.41) * mm});
            skLineSegment(sketch, "E763", {"start": v(145.85, -9.41) * mm, "end": v(145.7, -9.76) * mm});
            skLineSegment(sketch, "E764", {"start": v(145.7, -9.76) * mm, "end": v(145.54, -10.1) * mm});
            skLineSegment(sketch, "E765", {"start": v(145.54, -10.1) * mm, "end": v(144.56, -11.71) * mm});
            skLineSegment(sketch, "E766", {"start": v(144.56, -11.71) * mm, "end": v(143.3, -13.11) * mm});
            skLineSegment(sketch, "E767", {"start": v(143.3, -13.11) * mm, "end": v(143, -13.36) * mm});
            skLineSegment(sketch, "E768", {"start": v(143, -13.36) * mm, "end": v(142.67, -13.63) * mm});
            skLineSegment(sketch, "E769", {"start": v(142.67, -13.63) * mm, "end": v(140.92, -14.78) * mm});
            skLineSegment(sketch, "E770", {"start": v(140.92, -14.78) * mm, "end": v(139, -15.69) * mm});
            skLineSegment(sketch, "E771", {"start": v(139, -15.69) * mm, "end": v(138.58, -15.83) * mm});
            skLineSegment(sketch, "E772", {"start": v(138.58, -15.83) * mm, "end": v(138.18, -15.97) * mm});
            skLineSegment(sketch, "E773", {"start": v(138.18, -15.97) * mm, "end": v(135.83, -16.45) * mm});
            skLineSegment(sketch, "E774", {"start": v(135.83, -16.45) * mm, "end": v(133.29, -16.67) * mm});
            skLineSegment(sketch, "E775", {"start": v(133.29, -16.67) * mm, "end": v(132.44, -16.67) * mm});
            skLineSegment(sketch, "E776", {"start": v(49.23, -27.93) * mm, "end": v(49.23, -27.51) * mm});
            skLineSegment(sketch, "E777", {"start": v(49.23, -27.51) * mm, "end": v(49.06, -26.27) * mm});
            skLineSegment(sketch, "E778", {"start": v(49.06, -26.27) * mm, "end": v(48.66, -25.25) * mm});
            skLineSegment(sketch, "E779", {"start": v(48.66, -25.25) * mm, "end": v(48.54, -25.1) * mm});
            skLineSegment(sketch, "E780", {"start": v(48.54, -25.1) * mm, "end": v(48.43, -24.94) * mm});
            skLineSegment(sketch, "E781", {"start": v(48.43, -24.94) * mm, "end": v(47.7, -24.4) * mm});
            skLineSegment(sketch, "E782", {"start": v(47.7, -24.4) * mm, "end": v(46.85, -24.17) * mm});
            skLineSegment(sketch, "E783", {"start": v(46.85, -24.17) * mm, "end": v(46.57, -24.17) * mm});
            skLineSegment(sketch, "E784", {"start": v(46.57, -24.17) * mm, "end": v(46.28, -24.17) * mm});
            skLineSegment(sketch, "E785", {"start": v(46.28, -24.17) * mm, "end": v(45.42, -24.4) * mm});
            skLineSegment(sketch, "E786", {"start": v(45.42, -24.4) * mm, "end": v(44.7, -24.94) * mm});
            skLineSegment(sketch, "E787", {"start": v(44.7, -24.94) * mm, "end": v(44.58, -25.1) * mm});
            skLineSegment(sketch, "E788", {"start": v(44.58, -25.1) * mm, "end": v(44.46, -25.25) * mm});
            skLineSegment(sketch, "E789", {"start": v(44.46, -25.25) * mm, "end": v(44.05, -26.27) * mm});
            skLineSegment(sketch, "E790", {"start": v(44.05, -26.27) * mm, "end": v(43.88, -27.51) * mm});
            skLineSegment(sketch, "E791", {"start": v(43.88, -27.51) * mm, "end": v(43.88, -27.93) * mm});
            skLineSegment(sketch, "E792", {"start": v(43.88, -27.93) * mm, "end": v(43.88, -28.33) * mm});
            skLineSegment(sketch, "E793", {"start": v(43.88, -28.33) * mm, "end": v(44.05, -29.55) * mm});
            skLineSegment(sketch, "E794", {"start": v(44.05, -29.55) * mm, "end": v(44.46, -30.57) * mm});
            skLineSegment(sketch, "E795", {"start": v(44.46, -30.57) * mm, "end": v(44.58, -30.72) * mm});
            skLineSegment(sketch, "E796", {"start": v(44.58, -30.72) * mm, "end": v(44.7, -30.88) * mm});
            skLineSegment(sketch, "E797", {"start": v(44.7, -30.88) * mm, "end": v(45.42, -31.44) * mm});
            skLineSegment(sketch, "E798", {"start": v(45.42, -31.44) * mm, "end": v(46.28, -31.68) * mm});
            skLineSegment(sketch, "E799", {"start": v(46.28, -31.68) * mm, "end": v(46.57, -31.68) * mm});
            skLineSegment(sketch, "E800", {"start": v(46.57, -31.68) * mm, "end": v(46.85, -31.68) * mm});
            skLineSegment(sketch, "E801", {"start": v(46.85, -31.68) * mm, "end": v(47.7, -31.44) * mm});
            skLineSegment(sketch, "E802", {"start": v(47.7, -31.44) * mm, "end": v(48.42, -30.9) * mm});
            skLineSegment(sketch, "E803", {"start": v(48.42, -30.9) * mm, "end": v(48.54, -30.74) * mm});
            skLineSegment(sketch, "E804", {"start": v(48.54, -30.74) * mm, "end": v(48.65, -30.59) * mm});
            skLineSegment(sketch, "E805", {"start": v(48.65, -30.59) * mm, "end": v(49.06, -29.57) * mm});
            skLineSegment(sketch, "E806", {"start": v(49.06, -29.57) * mm, "end": v(49.23, -28.34) * mm});
            skLineSegment(sketch, "E807", {"start": v(49.23, -28.34) * mm, "end": v(49.23, -27.93) * mm});
            skLineSegment(sketch, "E808", {"start": v(50.94, -27.93) * mm, "end": v(50.94, -28.48) * mm});
            skLineSegment(sketch, "E809", {"start": v(50.94, -28.48) * mm, "end": v(50.64, -30.12) * mm});
            skLineSegment(sketch, "E810", {"start": v(50.64, -30.12) * mm, "end": v(49.94, -31.53) * mm});
            skLineSegment(sketch, "E811", {"start": v(49.94, -31.53) * mm, "end": v(49.74, -31.75) * mm});
            skLineSegment(sketch, "E812", {"start": v(49.74, -31.75) * mm, "end": v(49.54, -31.98) * mm});
            skLineSegment(sketch, "E813", {"start": v(49.54, -31.98) * mm, "end": v(48.35, -32.76) * mm});
            skLineSegment(sketch, "E814", {"start": v(48.35, -32.76) * mm, "end": v(47.01, -33.1) * mm});
            skLineSegment(sketch, "E815", {"start": v(47.01, -33.1) * mm, "end": v(46.57, -33.1) * mm});
            skLineSegment(sketch, "E816", {"start": v(46.57, -33.1) * mm, "end": v(46.1, -33.1) * mm});
            skLineSegment(sketch, "E817", {"start": v(46.1, -33.1) * mm, "end": v(44.74, -32.75) * mm});
            skLineSegment(sketch, "E818", {"start": v(44.74, -32.75) * mm, "end": v(43.54, -31.94) * mm});
            skLineSegment(sketch, "E819", {"start": v(43.54, -31.94) * mm, "end": v(43.35, -31.7) * mm});
            skLineSegment(sketch, "E820", {"start": v(43.35, -31.7) * mm, "end": v(43.15, -31.48) * mm});
            skLineSegment(sketch, "E821", {"start": v(43.15, -31.48) * mm, "end": v(42.47, -30.07) * mm});
            skLineSegment(sketch, "E822", {"start": v(42.47, -30.07) * mm, "end": v(42.17, -28.46) * mm});
            skLineSegment(sketch, "E823", {"start": v(42.17, -28.46) * mm, "end": v(42.17, -27.93) * mm});
            skLineSegment(sketch, "E824", {"start": v(42.17, -27.93) * mm, "end": v(42.17, -27.38) * mm});
            skLineSegment(sketch, "E825", {"start": v(42.17, -27.38) * mm, "end": v(42.48, -25.74) * mm});
            skLineSegment(sketch, "E826", {"start": v(42.48, -25.74) * mm, "end": v(43.18, -24.33) * mm});
            skLineSegment(sketch, "E827", {"start": v(43.18, -24.33) * mm, "end": v(43.38, -24.1) * mm});
            skLineSegment(sketch, "E828", {"start": v(43.38, -24.1) * mm, "end": v(43.58, -23.88) * mm});
            skLineSegment(sketch, "E829", {"start": v(43.58, -23.88) * mm, "end": v(44.78, -23.09) * mm});
            skLineSegment(sketch, "E830", {"start": v(44.78, -23.09) * mm, "end": v(46.12, -22.75) * mm});
            skLineSegment(sketch, "E831", {"start": v(46.12, -22.75) * mm, "end": v(46.57, -22.75) * mm});
            skLineSegment(sketch, "E832", {"start": v(46.57, -22.75) * mm, "end": v(47.01, -22.75) * mm});
            skLineSegment(sketch, "E833", {"start": v(47.01, -22.75) * mm, "end": v(48.35, -23.09) * mm});
            skLineSegment(sketch, "E834", {"start": v(48.35, -23.09) * mm, "end": v(49.54, -23.88) * mm});
            skLineSegment(sketch, "E835", {"start": v(49.54, -23.88) * mm, "end": v(49.74, -24.1) * mm});
            skLineSegment(sketch, "E836", {"start": v(49.74, -24.1) * mm, "end": v(49.94, -24.33) * mm});
            skLineSegment(sketch, "E837", {"start": v(49.94, -24.33) * mm, "end": v(50.64, -25.74) * mm});
            skLineSegment(sketch, "E838", {"start": v(50.64, -25.74) * mm, "end": v(50.94, -27.38) * mm});
            skLineSegment(sketch, "E839", {"start": v(50.94, -27.38) * mm, "end": v(50.94, -27.93) * mm});
            skLineSegment(sketch, "E840", {"start": v(61.8, -32.83) * mm, "end": v(60.15, -32.83) * mm});
            skLineSegment(sketch, "E841", {"start": v(60.15, -32.83) * mm, "end": v(60.15, -31.74) * mm});
            skLineSegment(sketch, "E842", {"start": v(60.15, -31.74) * mm, "end": v(60.02, -31.85) * mm});
            skLineSegment(sketch, "E843", {"start": v(60.02, -31.85) * mm, "end": v(58.82, -32.7) * mm});
            skLineSegment(sketch, "E844", {"start": v(58.82, -32.7) * mm, "end": v(58.7, -32.75) * mm});
            skLineSegment(sketch, "E845", {"start": v(58.7, -32.75) * mm, "end": v(58.59, -32.81) * mm});
            skLineSegment(sketch, "E846", {"start": v(58.59, -32.81) * mm, "end": v(57.53, -33.1) * mm});
            skLineSegment(sketch, "E847", {"start": v(57.53, -33.1) * mm, "end": v(57.17, -33.1) * mm});
            skLineSegment(sketch, "E848", {"start": v(57.17, -33.1) * mm, "end": v(56.87, -33.1) * mm});
            skLineSegment(sketch, "E849", {"start": v(56.87, -33.1) * mm, "end": v(56.06, -32.92) * mm});
            skLineSegment(sketch, "E850", {"start": v(56.06, -32.92) * mm, "end": v(55.97, -32.89) * mm});
            skLineSegment(sketch, "E851", {"start": v(55.97, -32.89) * mm, "end": v(55.87, -32.85) * mm});
            skLineSegment(sketch, "E852", {"start": v(55.87, -32.85) * mm, "end": v(55.05, -32.3) * mm});
            skLineSegment(sketch, "E853", {"start": v(55.05, -32.3) * mm, "end": v(54.98, -32.22) * mm});
            skLineSegment(sketch, "E854", {"start": v(54.98, -32.22) * mm, "end": v(54.9, -32.15) * mm});
            skLineSegment(sketch, "E855", {"start": v(54.9, -32.15) * mm, "end": v(54.36, -31.19) * mm});
            skLineSegment(sketch, "E856", {"start": v(54.36, -31.19) * mm, "end": v(54.32, -31.07) * mm});
            skLineSegment(sketch, "E857", {"start": v(54.32, -31.07) * mm, "end": v(54.29, -30.96) * mm});
            skLineSegment(sketch, "E858", {"start": v(54.29, -30.96) * mm, "end": v(54.1, -29.78) * mm});
            skLineSegment(sketch, "E859", {"start": v(54.1, -29.78) * mm, "end": v(54.1, -29.39) * mm});
            skLineSegment(sketch, "E860", {"start": v(54.1, -29.39) * mm, "end": v(54.1, -23.02) * mm});
            skLineSegment(sketch, "E861", {"start": v(54.1, -23.02) * mm, "end": v(55.74, -23.02) * mm});
            skLineSegment(sketch, "E862", {"start": v(55.74, -23.02) * mm, "end": v(55.74, -28.6) * mm});
            skLineSegment(sketch, "E863", {"start": v(55.74, -28.6) * mm, "end": v(55.74, -28.93) * mm});
            skLineSegment(sketch, "E864", {"start": v(55.74, -28.93) * mm, "end": v(55.8, -29.81) * mm});
            skLineSegment(sketch, "E865", {"start": v(55.8, -29.81) * mm, "end": v(55.8, -29.9) * mm});
            skLineSegment(sketch, "E866", {"start": v(55.8, -29.9) * mm, "end": v(55.8, -29.98) * mm});
            skLineSegment(sketch, "E867", {"start": v(55.8, -29.98) * mm, "end": v(56.02, -30.74) * mm});
            skLineSegment(sketch, "E868", {"start": v(56.02, -30.74) * mm, "end": v(56.06, -30.8) * mm});
            skLineSegment(sketch, "E869", {"start": v(56.06, -30.8) * mm, "end": v(56.1, -30.86) * mm});
            skLineSegment(sketch, "E870", {"start": v(56.1, -30.86) * mm, "end": v(56.55, -31.32) * mm});
            skLineSegment(sketch, "E871", {"start": v(56.55, -31.32) * mm, "end": v(56.6, -31.35) * mm});
            skLineSegment(sketch, "E872", {"start": v(56.6, -31.35) * mm, "end": v(56.67, -31.38) * mm});
            skLineSegment(sketch, "E873", {"start": v(56.67, -31.38) * mm, "end": v(57.37, -31.53) * mm});
            skLineSegment(sketch, "E874", {"start": v(57.37, -31.53) * mm, "end": v(57.6, -31.53) * mm});
            skLineSegment(sketch, "E875", {"start": v(57.6, -31.53) * mm, "end": v(57.93, -31.53) * mm});
            skLineSegment(sketch, "E876", {"start": v(57.93, -31.53) * mm, "end": v(58.78, -31.24) * mm});
            skLineSegment(sketch, "E877", {"start": v(58.78, -31.24) * mm, "end": v(58.9, -31.19) * mm});
            skLineSegment(sketch, "E878", {"start": v(58.9, -31.19) * mm, "end": v(59, -31.13) * mm});
            skLineSegment(sketch, "E879", {"start": v(59, -31.13) * mm, "end": v(60.06, -30.43) * mm});
            skLineSegment(sketch, "E880", {"start": v(60.06, -30.43) * mm, "end": v(60.15, -30.34) * mm});
            skLineSegment(sketch, "E881", {"start": v(60.15, -30.34) * mm, "end": v(60.15, -23.02) * mm});
            skLineSegment(sketch, "E882", {"start": v(60.15, -23.02) * mm, "end": v(61.8, -23.02) * mm});
            skLineSegment(sketch, "E883", {"start": v(61.8, -23.02) * mm, "end": v(61.8, -32.83) * mm});
            skLineSegment(sketch, "E884", {"start": v(70.92, -24.8) * mm, "end": v(70.83, -24.8) * mm});
            skLineSegment(sketch, "E885", {"start": v(70.83, -24.8) * mm, "end": v(70.8, -24.78) * mm});
            skLineSegment(sketch, "E886", {"start": v(70.8, -24.78) * mm, "end": v(70.47, -24.73) * mm});
            skLineSegment(sketch, "E887", {"start": v(70.47, -24.73) * mm, "end": v(70.44, -24.73) * mm});
            skLineSegment(sketch, "E888", {"start": v(70.44, -24.73) * mm, "end": v(70.4, -24.72) * mm});
            skLineSegment(sketch, "E889", {"start": v(70.4, -24.72) * mm, "end": v(70.06, -24.72) * mm});
            skLineSegment(sketch, "E890", {"start": v(70.06, -24.72) * mm, "end": v(69.94, -24.72) * mm});
            skLineSegment(sketch, "E891", {"start": v(69.94, -24.72) * mm, "end": v(69.61, -24.72) * mm});
            skLineSegment(sketch, "E892", {"start": v(69.61, -24.72) * mm, "end": v(68.73, -24.95) * mm});
            skLineSegment(sketch, "E893", {"start": v(68.73, -24.95) * mm, "end": v(68.62, -25) * mm});
            skLineSegment(sketch, "E894", {"start": v(68.62, -25) * mm, "end": v(68.5, -25.05) * mm});
            skLineSegment(sketch, "E895", {"start": v(68.5, -25.05) * mm, "end": v(67.47, -25.77) * mm});
            skLineSegment(sketch, "E896", {"start": v(67.47, -25.77) * mm, "end": v(67.37, -25.86) * mm});
            skLineSegment(sketch, "E897", {"start": v(67.37, -25.86) * mm, "end": v(67.37, -32.83) * mm});
            skLineSegment(sketch, "E898", {"start": v(67.37, -32.83) * mm, "end": v(65.72, -32.83) * mm});
            skLineSegment(sketch, "E899", {"start": v(65.72, -32.83) * mm, "end": v(65.72, -23.02) * mm});
            skLineSegment(sketch, "E900", {"start": v(65.72, -23.02) * mm, "end": v(67.37, -23.02) * mm});
            skLineSegment(sketch, "E901", {"start": v(67.37, -23.02) * mm, "end": v(67.37, -24.48) * mm});
            skLineSegment(sketch, "E902", {"start": v(67.37, -24.48) * mm, "end": v(67.52, -24.34) * mm});
            skLineSegment(sketch, "E903", {"start": v(67.52, -24.34) * mm, "end": v(68.22, -23.8) * mm});
            skLineSegment(sketch, "E904", {"start": v(68.22, -23.8) * mm, "end": v(68.83, -23.4) * mm});
            skLineSegment(sketch, "E905", {"start": v(68.83, -23.4) * mm, "end": v(68.95, -23.35) * mm});
            skLineSegment(sketch, "E906", {"start": v(68.95, -23.35) * mm, "end": v(69.06, -23.3) * mm});
            skLineSegment(sketch, "E907", {"start": v(69.06, -23.3) * mm, "end": v(69.95, -23.02) * mm});
            skLineSegment(sketch, "E908", {"start": v(69.95, -23.02) * mm, "end": v(70.25, -23.02) * mm});
            skLineSegment(sketch, "E909", {"start": v(70.25, -23.02) * mm, "end": v(70.35, -23.02) * mm});
            skLineSegment(sketch, "E910", {"start": v(70.35, -23.02) * mm, "end": v(70.61, -23.03) * mm});
            skLineSegment(sketch, "E911", {"start": v(70.61, -23.03) * mm, "end": v(70.63, -23.03) * mm});
            skLineSegment(sketch, "E912", {"start": v(70.63, -23.03) * mm, "end": v(70.65, -23.03) * mm});
            skLineSegment(sketch, "E913", {"start": v(70.65, -23.03) * mm, "end": v(70.9, -23.07) * mm});
            skLineSegment(sketch, "E914", {"start": v(70.9, -23.07) * mm, "end": v(70.92, -23.07) * mm});
            skLineSegment(sketch, "E915", {"start": v(70.92, -23.07) * mm, "end": v(70.92, -24.8) * mm});
            skLineSegment(sketch, "E916", {"start": v(87.4, -27.85) * mm, "end": v(87.4, -27.48) * mm});
            skLineSegment(sketch, "E917", {"start": v(87.4, -27.48) * mm, "end": v(87.27, -26.36) * mm});
            skLineSegment(sketch, "E918", {"start": v(87.27, -26.36) * mm, "end": v(86.95, -25.4) * mm});
            skLineSegment(sketch, "E919", {"start": v(86.95, -25.4) * mm, "end": v(86.87, -25.25) * mm});
            skLineSegment(sketch, "E920", {"start": v(86.87, -25.25) * mm, "end": v(86.78, -25.1) * mm});
            skLineSegment(sketch, "E921", {"start": v(86.78, -25.1) * mm, "end": v(86.16, -24.55) * mm});
            skLineSegment(sketch, "E922", {"start": v(86.16, -24.55) * mm, "end": v(85.39, -24.32) * mm});
            skLineSegment(sketch, "E923", {"start": v(85.39, -24.32) * mm, "end": v(85.13, -24.32) * mm});
            skLineSegment(sketch, "E924", {"start": v(85.13, -24.32) * mm, "end": v(84.79, -24.32) * mm});
            skLineSegment(sketch, "E925", {"start": v(84.79, -24.32) * mm, "end": v(83.88, -24.58) * mm});
            skLineSegment(sketch, "E926", {"start": v(83.88, -24.58) * mm, "end": v(83.77, -24.63) * mm});
            skLineSegment(sketch, "E927", {"start": v(83.77, -24.63) * mm, "end": v(83.66, -24.68) * mm});
            skLineSegment(sketch, "E928", {"start": v(83.66, -24.68) * mm, "end": v(82.63, -25.35) * mm});
            skLineSegment(sketch, "E929", {"start": v(82.63, -25.35) * mm, "end": v(82.53, -25.43) * mm});
            skLineSegment(sketch, "E930", {"start": v(82.53, -25.43) * mm, "end": v(82.53, -31) * mm});
            skLineSegment(sketch, "E931", {"start": v(82.53, -31) * mm, "end": v(82.64, -31.05) * mm});
            skLineSegment(sketch, "E932", {"start": v(82.64, -31.05) * mm, "end": v(83.56, -31.4) * mm});
            skLineSegment(sketch, "E933", {"start": v(83.56, -31.4) * mm, "end": v(83.64, -31.42) * mm});
            skLineSegment(sketch, "E934", {"start": v(83.64, -31.42) * mm, "end": v(83.71, -31.44) * mm});
            skLineSegment(sketch, "E935", {"start": v(83.71, -31.44) * mm, "end": v(84.45, -31.54) * mm});
            skLineSegment(sketch, "E936", {"start": v(84.45, -31.54) * mm, "end": v(84.7, -31.54) * mm});
            skLineSegment(sketch, "E937", {"start": v(84.7, -31.54) * mm, "end": v(84.98, -31.54) * mm});
            skLineSegment(sketch, "E938", {"start": v(84.98, -31.54) * mm, "end": v(85.84, -31.3) * mm});
            skLineSegment(sketch, "E939", {"start": v(85.84, -31.3) * mm, "end": v(86.57, -30.75) * mm});
            skLineSegment(sketch, "E940", {"start": v(86.57, -30.75) * mm, "end": v(86.7, -30.6) * mm});
            skLineSegment(sketch, "E941", {"start": v(86.7, -30.6) * mm, "end": v(86.8, -30.44) * mm});
            skLineSegment(sketch, "E942", {"start": v(86.8, -30.44) * mm, "end": v(87.22, -29.44) * mm});
            skLineSegment(sketch, "E943", {"start": v(87.22, -29.44) * mm, "end": v(87.4, -28.25) * mm});
            skLineSegment(sketch, "E944", {"start": v(87.4, -28.25) * mm, "end": v(87.4, -27.85) * mm});
            skLineSegment(sketch, "E945", {"start": v(89.1, -27.66) * mm, "end": v(89.1, -28.21) * mm});
            skLineSegment(sketch, "E946", {"start": v(89.1, -28.21) * mm, "end": v(88.81, -29.86) * mm});
            skLineSegment(sketch, "E947", {"start": v(88.81, -29.86) * mm, "end": v(88.13, -31.33) * mm});
            skLineSegment(sketch, "E948", {"start": v(88.13, -31.33) * mm, "end": v(87.93, -31.57) * mm});
            skLineSegment(sketch, "E949", {"start": v(87.93, -31.57) * mm, "end": v(87.74, -31.8) * mm});
            skLineSegment(sketch, "E950", {"start": v(87.74, -31.8) * mm, "end": v(86.6, -32.66) * mm});
            skLineSegment(sketch, "E951", {"start": v(86.6, -32.66) * mm, "end": v(85.38, -33.02) * mm});
            skLineSegment(sketch, "E952", {"start": v(85.38, -33.02) * mm, "end": v(84.97, -33.02) * mm});
            skLineSegment(sketch, "E953", {"start": v(84.97, -33.02) * mm, "end": v(84.65, -33.02) * mm});
            skLineSegment(sketch, "E954", {"start": v(84.65, -33.02) * mm, "end": v(83.77, -32.88) * mm});
            skLineSegment(sketch, "E955", {"start": v(83.77, -32.88) * mm, "end": v(83.68, -32.86) * mm});
            skLineSegment(sketch, "E956", {"start": v(83.68, -32.86) * mm, "end": v(83.59, -32.83) * mm});
            skLineSegment(sketch, "E957", {"start": v(83.59, -32.83) * mm, "end": v(82.63, -32.4) * mm});
            skLineSegment(sketch, "E958", {"start": v(82.63, -32.4) * mm, "end": v(82.53, -32.34) * mm});
            skLineSegment(sketch, "E959", {"start": v(82.53, -32.34) * mm, "end": v(82.53, -36.45) * mm});
            skLineSegment(sketch, "E960", {"start": v(82.53, -36.45) * mm, "end": v(80.88, -36.45) * mm});
            skLineSegment(sketch, "E961", {"start": v(80.88, -36.45) * mm, "end": v(80.88, -23.02) * mm});
            skLineSegment(sketch, "E962", {"start": v(80.88, -23.02) * mm, "end": v(82.53, -23.02) * mm});
            skLineSegment(sketch, "E963", {"start": v(82.53, -23.02) * mm, "end": v(82.53, -24.05) * mm});
            skLineSegment(sketch, "E964", {"start": v(82.53, -24.05) * mm, "end": v(82.63, -23.95) * mm});
            skLineSegment(sketch, "E965", {"start": v(82.63, -23.95) * mm, "end": v(83.77, -23.18) * mm});
            skLineSegment(sketch, "E966", {"start": v(83.77, -23.18) * mm, "end": v(83.9, -23.12) * mm});
            skLineSegment(sketch, "E967", {"start": v(83.9, -23.12) * mm, "end": v(84.02, -23.06) * mm});
            skLineSegment(sketch, "E968", {"start": v(84.02, -23.06) * mm, "end": v(85.15, -22.75) * mm});
            skLineSegment(sketch, "E969", {"start": v(85.15, -22.75) * mm, "end": v(85.53, -22.75) * mm});
            skLineSegment(sketch, "E970", {"start": v(85.53, -22.75) * mm, "end": v(85.9, -22.75) * mm});
            skLineSegment(sketch, "E971", {"start": v(85.9, -22.75) * mm, "end": v(87.03, -23.08) * mm});
            skLineSegment(sketch, "E972", {"start": v(87.03, -23.08) * mm, "end": v(88, -23.86) * mm});
            skLineSegment(sketch, "E973", {"start": v(88, -23.86) * mm, "end": v(88.16, -24.08) * mm});
            skLineSegment(sketch, "E974", {"start": v(88.16, -24.08) * mm, "end": v(88.32, -24.3) * mm});
            skLineSegment(sketch, "E975", {"start": v(88.32, -24.3) * mm, "end": v(88.87, -25.65) * mm});
            skLineSegment(sketch, "E976", {"start": v(88.87, -25.65) * mm, "end": v(89.1, -27.16) * mm});
            skLineSegment(sketch, "E977", {"start": v(89.1, -27.16) * mm, "end": v(89.1, -27.66) * mm});
            skLineSegment(sketch, "E978", {"start": v(97.83, -30.41) * mm, "end": v(97.83, -27.7) * mm});
            skLineSegment(sketch, "E979", {"start": v(97.83, -27.7) * mm, "end": v(97.73, -27.7) * mm});
            skLineSegment(sketch, "E980", {"start": v(97.73, -27.7) * mm, "end": v(96.49, -27.82) * mm});
            skLineSegment(sketch, "E981", {"start": v(96.49, -27.82) * mm, "end": v(96.34, -27.84) * mm});
            skLineSegment(sketch, "E982", {"start": v(96.34, -27.84) * mm, "end": v(96.19, -27.85) * mm});
            skLineSegment(sketch, "E983", {"start": v(96.19, -27.85) * mm, "end": v(94.98, -28.07) * mm});
            skLineSegment(sketch, "E984", {"start": v(94.98, -28.07) * mm, "end": v(94.88, -28.1) * mm});
            skLineSegment(sketch, "E985", {"start": v(94.88, -28.1) * mm, "end": v(94.77, -28.13) * mm});
            skLineSegment(sketch, "E986", {"start": v(94.77, -28.13) * mm, "end": v(93.87, -28.64) * mm});
            skLineSegment(sketch, "E987", {"start": v(93.87, -28.64) * mm, "end": v(93.8, -28.71) * mm});
            skLineSegment(sketch, "E988", {"start": v(93.8, -28.71) * mm, "end": v(93.72, -28.78) * mm});
            skLineSegment(sketch, "E989", {"start": v(93.72, -28.78) * mm, "end": v(93.47, -29.21) * mm});
            skLineSegment(sketch, "E990", {"start": v(93.47, -29.21) * mm, "end": v(93.37, -29.71) * mm});
            skLineSegment(sketch, "E991", {"start": v(93.37, -29.71) * mm, "end": v(93.37, -29.88) * mm});
            skLineSegment(sketch, "E992", {"start": v(93.37, -29.88) * mm, "end": v(93.37, -30.06) * mm});
            skLineSegment(sketch, "E993", {"start": v(93.37, -30.06) * mm, "end": v(93.48, -30.62) * mm});
            skLineSegment(sketch, "E994", {"start": v(93.48, -30.62) * mm, "end": v(93.76, -31.08) * mm});
            skLineSegment(sketch, "E995", {"start": v(93.76, -31.08) * mm, "end": v(93.84, -31.15) * mm});
            skLineSegment(sketch, "E996", {"start": v(93.84, -31.15) * mm, "end": v(93.92, -31.22) * mm});
            skLineSegment(sketch, "E997", {"start": v(93.92, -31.22) * mm, "end": v(94.42, -31.47) * mm});
            skLineSegment(sketch, "E998", {"start": v(94.42, -31.47) * mm, "end": v(95.03, -31.58) * mm});
            skLineSegment(sketch, "E999", {"start": v(95.03, -31.58) * mm, "end": v(95.23, -31.58) * mm});
            skLineSegment(sketch, "E1000", {"start": v(95.23, -31.58) * mm, "end": v(95.58, -31.58) * mm});
            skLineSegment(sketch, "E1001", {"start": v(95.58, -31.58) * mm, "end": v(96.53, -31.3) * mm});
            skLineSegment(sketch, "E1002", {"start": v(96.53, -31.3) * mm, "end": v(96.64, -31.24) * mm});
            skLineSegment(sketch, "E1003", {"start": v(96.64, -31.24) * mm, "end": v(96.75, -31.19) * mm});
            skLineSegment(sketch, "E1004", {"start": v(96.75, -31.19) * mm, "end": v(97.73, -30.5) * mm});
            skLineSegment(sketch, "E1005", {"start": v(97.73, -30.5) * mm, "end": v(97.83, -30.41) * mm});
            skLineSegment(sketch, "E1006", {"start": v(97.83, -31.78) * mm, "end": v(97.8, -31.8) * mm});
            skLineSegment(sketch, "E1007", {"start": v(97.8, -31.8) * mm, "end": v(97.34, -32.16) * mm});
            skLineSegment(sketch, "E1008", {"start": v(97.34, -32.16) * mm, "end": v(97.29, -32.2) * mm});
            skLineSegment(sketch, "E1009", {"start": v(97.29, -32.2) * mm, "end": v(97.23, -32.24) * mm});
            skLineSegment(sketch, "E1010", {"start": v(97.23, -32.24) * mm, "end": v(96.68, -32.6) * mm});
            skLineSegment(sketch, "E1011", {"start": v(96.68, -32.6) * mm, "end": v(96.63, -32.63) * mm});
            skLineSegment(sketch, "E1012", {"start": v(96.63, -32.63) * mm, "end": v(96.56, -32.66) * mm});
            skLineSegment(sketch, "E1013", {"start": v(96.56, -32.66) * mm, "end": v(95.85, -32.96) * mm});
            skLineSegment(sketch, "E1014", {"start": v(95.85, -32.96) * mm, "end": v(95.78, -32.98) * mm});
            skLineSegment(sketch, "E1015", {"start": v(95.78, -32.98) * mm, "end": v(95.72, -33) * mm});
            skLineSegment(sketch, "E1016", {"start": v(95.72, -33) * mm, "end": v(94.9, -33.1) * mm});
            skLineSegment(sketch, "E1017", {"start": v(94.9, -33.1) * mm, "end": v(94.64, -33.1) * mm});
            skLineSegment(sketch, "E1018", {"start": v(94.64, -33.1) * mm, "end": v(94.35, -33.1) * mm});
            skLineSegment(sketch, "E1019", {"start": v(94.35, -33.1) * mm, "end": v(93.58, -32.9) * mm});
            skLineSegment(sketch, "E1020", {"start": v(93.58, -32.9) * mm, "end": v(93.49, -32.87) * mm});
            skLineSegment(sketch, "E1021", {"start": v(93.49, -32.87) * mm, "end": v(93.4, -32.83) * mm});
            skLineSegment(sketch, "E1022", {"start": v(93.4, -32.83) * mm, "end": v(92.6, -32.3) * mm});
            skLineSegment(sketch, "E1023", {"start": v(92.6, -32.3) * mm, "end": v(92.53, -32.23) * mm});
            skLineSegment(sketch, "E1024", {"start": v(92.53, -32.23) * mm, "end": v(92.47, -32.16) * mm});
            skLineSegment(sketch, "E1025", {"start": v(92.47, -32.16) * mm, "end": v(91.94, -31.33) * mm});
            skLineSegment(sketch, "E1026", {"start": v(91.94, -31.33) * mm, "end": v(91.9, -31.23) * mm});
            skLineSegment(sketch, "E1027", {"start": v(91.9, -31.23) * mm, "end": v(91.86, -31.14) * mm});
            skLineSegment(sketch, "E1028", {"start": v(91.86, -31.14) * mm, "end": v(91.66, -30.27) * mm});
            skLineSegment(sketch, "E1029", {"start": v(91.66, -30.27) * mm, "end": v(91.66, -29.98) * mm});
            skLineSegment(sketch, "E1030", {"start": v(91.66, -29.98) * mm, "end": v(91.66, -29.75) * mm});
            skLineSegment(sketch, "E1031", {"start": v(91.66, -29.75) * mm, "end": v(91.77, -29.04) * mm});
            skLineSegment(sketch, "E1032", {"start": v(91.77, -29.04) * mm, "end": v(92.02, -28.37) * mm});
            skLineSegment(sketch, "E1033", {"start": v(92.02, -28.37) * mm, "end": v(92.1, -28.25) * mm});
            skLineSegment(sketch, "E1034", {"start": v(92.1, -28.25) * mm, "end": v(92.16, -28.13) * mm});
            skLineSegment(sketch, "E1035", {"start": v(92.16, -28.13) * mm, "end": v(92.65, -27.6) * mm});
            skLineSegment(sketch, "E1036", {"start": v(92.65, -27.6) * mm, "end": v(93.3, -27.18) * mm});
            skLineSegment(sketch, "E1037", {"start": v(93.3, -27.18) * mm, "end": v(93.45, -27.11) * mm});
            skLineSegment(sketch, "E1038", {"start": v(93.45, -27.11) * mm, "end": v(93.59, -27.05) * mm});
            skLineSegment(sketch, "E1039", {"start": v(93.59, -27.05) * mm, "end": v(95.22, -26.61) * mm});
            skLineSegment(sketch, "E1040", {"start": v(95.22, -26.61) * mm, "end": v(95.4, -26.59) * mm});
            skLineSegment(sketch, "E1041", {"start": v(95.4, -26.59) * mm, "end": v(95.6, -26.56) * mm});
            skLineSegment(sketch, "E1042", {"start": v(95.6, -26.56) * mm, "end": v(97.6, -26.39) * mm});
            skLineSegment(sketch, "E1043", {"start": v(97.6, -26.39) * mm, "end": v(97.83, -26.37) * mm});
            skLineSegment(sketch, "E1044", {"start": v(97.83, -26.37) * mm, "end": v(97.83, -26.06) * mm});
            skLineSegment(sketch, "E1045", {"start": v(97.83, -26.06) * mm, "end": v(97.83, -25.82) * mm});
            skLineSegment(sketch, "E1046", {"start": v(97.83, -25.82) * mm, "end": v(97.68, -25.18) * mm});
            skLineSegment(sketch, "E1047", {"start": v(97.68, -25.18) * mm, "end": v(97.65, -25.12) * mm});
            skLineSegment(sketch, "E1048", {"start": v(97.65, -25.12) * mm, "end": v(97.62, -25.06) * mm});
            skLineSegment(sketch, "E1049", {"start": v(97.62, -25.06) * mm, "end": v(97.21, -24.6) * mm});
            skLineSegment(sketch, "E1050", {"start": v(97.21, -24.6) * mm, "end": v(97.16, -24.57) * mm});
            skLineSegment(sketch, "E1051", {"start": v(97.16, -24.57) * mm, "end": v(97.1, -24.54) * mm});
            skLineSegment(sketch, "E1052", {"start": v(97.1, -24.54) * mm, "end": v(96.46, -24.32) * mm});
            skLineSegment(sketch, "E1053", {"start": v(96.46, -24.32) * mm, "end": v(96.39, -24.3) * mm});
            skLineSegment(sketch, "E1054", {"start": v(96.39, -24.3) * mm, "end": v(96.3, -24.3) * mm});
            skLineSegment(sketch, "E1055", {"start": v(96.3, -24.3) * mm, "end": v(95.66, -24.24) * mm});
            skLineSegment(sketch, "E1056", {"start": v(95.66, -24.24) * mm, "end": v(95.45, -24.24) * mm});
            skLineSegment(sketch, "E1057", {"start": v(95.45, -24.24) * mm, "end": v(95.11, -24.24) * mm});
            skLineSegment(sketch, "E1058", {"start": v(95.11, -24.24) * mm, "end": v(94.23, -24.38) * mm});
            skLineSegment(sketch, "E1059", {"start": v(94.23, -24.38) * mm, "end": v(94.1, -24.41) * mm});
            skLineSegment(sketch, "E1060", {"start": v(94.1, -24.41) * mm, "end": v(93.97, -24.44) * mm});
            skLineSegment(sketch, "E1061", {"start": v(93.97, -24.44) * mm, "end": v(92.69, -24.85) * mm});
            skLineSegment(sketch, "E1062", {"start": v(92.69, -24.85) * mm, "end": v(92.56, -24.9) * mm});
            skLineSegment(sketch, "E1063", {"start": v(92.56, -24.9) * mm, "end": v(92.46, -24.9) * mm});
            skLineSegment(sketch, "E1064", {"start": v(92.46, -24.9) * mm, "end": v(92.46, -23.23) * mm});
            skLineSegment(sketch, "E1065", {"start": v(92.46, -23.23) * mm, "end": v(92.54, -23.2) * mm});
            skLineSegment(sketch, "E1066", {"start": v(92.54, -23.2) * mm, "end": v(93.63, -22.97) * mm});
            skLineSegment(sketch, "E1067", {"start": v(93.63, -22.97) * mm, "end": v(93.77, -22.94) * mm});
            skLineSegment(sketch, "E1068", {"start": v(93.77, -22.94) * mm, "end": v(93.91, -22.91) * mm});
            skLineSegment(sketch, "E1069", {"start": v(93.91, -22.91) * mm, "end": v(95.07, -22.78) * mm});
            skLineSegment(sketch, "E1070", {"start": v(95.07, -22.78) * mm, "end": v(95.46, -22.78) * mm});
            skLineSegment(sketch, "E1071", {"start": v(95.46, -22.78) * mm, "end": v(95.88, -22.78) * mm});
            skLineSegment(sketch, "E1072", {"start": v(95.88, -22.78) * mm, "end": v(97.04, -22.91) * mm});
            skLineSegment(sketch, "E1073", {"start": v(97.04, -22.91) * mm, "end": v(97.16, -22.94) * mm});
            skLineSegment(sketch, "E1074", {"start": v(97.16, -22.94) * mm, "end": v(97.27, -22.97) * mm});
            skLineSegment(sketch, "E1075", {"start": v(97.27, -22.97) * mm, "end": v(98.31, -23.44) * mm});
            skLineSegment(sketch, "E1076", {"start": v(98.31, -23.44) * mm, "end": v(98.4, -23.51) * mm});
            skLineSegment(sketch, "E1077", {"start": v(98.4, -23.51) * mm, "end": v(98.5, -23.58) * mm});
            skLineSegment(sketch, "E1078", {"start": v(98.5, -23.58) * mm, "end": v(99.16, -24.45) * mm});
            skLineSegment(sketch, "E1079", {"start": v(99.16, -24.45) * mm, "end": v(99.2, -24.56) * mm});
            skLineSegment(sketch, "E1080", {"start": v(99.2, -24.56) * mm, "end": v(99.25, -24.66) * mm});
            skLineSegment(sketch, "E1081", {"start": v(99.25, -24.66) * mm, "end": v(99.47, -25.75) * mm});
            skLineSegment(sketch, "E1082", {"start": v(99.47, -25.75) * mm, "end": v(99.47, -26.12) * mm});
            skLineSegment(sketch, "E1083", {"start": v(99.47, -26.12) * mm, "end": v(99.47, -32.83) * mm});
            skLineSegment(sketch, "E1084", {"start": v(99.47, -32.83) * mm, "end": v(97.83, -32.83) * mm});
            skLineSegment(sketch, "E1085", {"start": v(97.83, -32.83) * mm, "end": v(97.83, -31.78) * mm});
            skLineSegment(sketch, "E1086", {"start": v(105.97, -33.07) * mm, "end": v(105.5, -33.07) * mm});
            skLineSegment(sketch, "E1087", {"start": v(105.5, -33.07) * mm, "end": v(104.27, -32.85) * mm});
            skLineSegment(sketch, "E1088", {"start": v(104.27, -32.85) * mm, "end": v(104.13, -32.8) * mm});
            skLineSegment(sketch, "E1089", {"start": v(104.13, -32.8) * mm, "end": v(103.98, -32.76) * mm});
            skLineSegment(sketch, "E1090", {"start": v(103.98, -32.76) * mm, "end": v(102.8, -32.3) * mm});
            skLineSegment(sketch, "E1091", {"start": v(102.8, -32.3) * mm, "end": v(102.7, -32.24) * mm});
            skLineSegment(sketch, "E1092", {"start": v(102.7, -32.24) * mm, "end": v(102.7, -30.39) * mm});
            skLineSegment(sketch, "E1093", {"start": v(102.7, -30.39) * mm, "end": v(102.8, -30.39) * mm});
            skLineSegment(sketch, "E1094", {"start": v(102.8, -30.39) * mm, "end": v(102.83, -30.41) * mm});
            skLineSegment(sketch, "E1095", {"start": v(102.83, -30.41) * mm, "end": v(103.25, -30.72) * mm});
            skLineSegment(sketch, "E1096", {"start": v(103.25, -30.72) * mm, "end": v(103.3, -30.76) * mm});
            skLineSegment(sketch, "E1097", {"start": v(103.3, -30.76) * mm, "end": v(103.34, -30.79) * mm});
            skLineSegment(sketch, "E1098", {"start": v(103.34, -30.79) * mm, "end": v(103.97, -31.14) * mm});
            skLineSegment(sketch, "E1099", {"start": v(103.97, -31.14) * mm, "end": v(104.05, -31.18) * mm});
            skLineSegment(sketch, "E1100", {"start": v(104.05, -31.18) * mm, "end": v(104.12, -31.2) * mm});
            skLineSegment(sketch, "E1101", {"start": v(104.12, -31.2) * mm, "end": v(104.9, -31.5) * mm});
            skLineSegment(sketch, "E1102", {"start": v(104.9, -31.5) * mm, "end": v(104.98, -31.52) * mm});
            skLineSegment(sketch, "E1103", {"start": v(104.98, -31.52) * mm, "end": v(105.06, -31.54) * mm});
            skLineSegment(sketch, "E1104", {"start": v(105.06, -31.54) * mm, "end": v(105.79, -31.67) * mm});
            skLineSegment(sketch, "E1105", {"start": v(105.79, -31.67) * mm, "end": v(106.03, -31.67) * mm});
            skLineSegment(sketch, "E1106", {"start": v(106.03, -31.67) * mm, "end": v(106.24, -31.67) * mm});
            skLineSegment(sketch, "E1107", {"start": v(106.24, -31.67) * mm, "end": v(106.8, -31.6) * mm});
            skLineSegment(sketch, "E1108", {"start": v(106.8, -31.6) * mm, "end": v(106.87, -31.58) * mm});
            skLineSegment(sketch, "E1109", {"start": v(106.87, -31.58) * mm, "end": v(106.95, -31.56) * mm});
            skLineSegment(sketch, "E1110", {"start": v(106.95, -31.56) * mm, "end": v(107.5, -31.37) * mm});
            skLineSegment(sketch, "E1111", {"start": v(107.5, -31.37) * mm, "end": v(107.54, -31.34) * mm});
            skLineSegment(sketch, "E1112", {"start": v(107.54, -31.34) * mm, "end": v(107.6, -31.31) * mm});
            skLineSegment(sketch, "E1113", {"start": v(107.6, -31.31) * mm, "end": v(107.96, -30.95) * mm});
            skLineSegment(sketch, "E1114", {"start": v(107.96, -30.95) * mm, "end": v(107.98, -30.91) * mm});
            skLineSegment(sketch, "E1115", {"start": v(107.98, -30.91) * mm, "end": v(108, -30.87) * mm});
            skLineSegment(sketch, "E1116", {"start": v(108, -30.87) * mm, "end": v(108.12, -30.39) * mm});
            skLineSegment(sketch, "E1117", {"start": v(108.12, -30.39) * mm, "end": v(108.12, -30.23) * mm});
            skLineSegment(sketch, "E1118", {"start": v(108.12, -30.23) * mm, "end": v(108.12, -30) * mm});
            skLineSegment(sketch, "E1119", {"start": v(108.12, -30) * mm, "end": v(107.85, -29.4) * mm});
            skLineSegment(sketch, "E1120", {"start": v(107.85, -29.4) * mm, "end": v(107.8, -29.34) * mm});
            skLineSegment(sketch, "E1121", {"start": v(107.8, -29.34) * mm, "end": v(107.74, -29.3) * mm});
            skLineSegment(sketch, "E1122", {"start": v(107.74, -29.3) * mm, "end": v(106.8, -28.88) * mm});
            skLineSegment(sketch, "E1123", {"start": v(106.8, -28.88) * mm, "end": v(106.66, -28.84) * mm});
            skLineSegment(sketch, "E1124", {"start": v(106.66, -28.84) * mm, "end": v(106.6, -28.83) * mm});
            skLineSegment(sketch, "E1125", {"start": v(106.6, -28.83) * mm, "end": v(105.92, -28.67) * mm});
            skLineSegment(sketch, "E1126", {"start": v(105.92, -28.67) * mm, "end": v(105.83, -28.66) * mm});
            skLineSegment(sketch, "E1127", {"start": v(105.83, -28.66) * mm, "end": v(105.75, -28.64) * mm});
            skLineSegment(sketch, "E1128", {"start": v(105.75, -28.64) * mm, "end": v(104.97, -28.45) * mm});
            skLineSegment(sketch, "E1129", {"start": v(104.97, -28.45) * mm, "end": v(104.9, -28.43) * mm});
            skLineSegment(sketch, "E1130", {"start": v(104.9, -28.43) * mm, "end": v(104.7, -28.37) * mm});
            skLineSegment(sketch, "E1131", {"start": v(104.7, -28.37) * mm, "end": v(103.92, -28.02) * mm});
            skLineSegment(sketch, "E1132", {"start": v(103.92, -28.02) * mm, "end": v(103.35, -27.54) * mm});
            skLineSegment(sketch, "E1133", {"start": v(103.35, -27.54) * mm, "end": v(103.26, -27.42) * mm});
            skLineSegment(sketch, "E1134", {"start": v(103.26, -27.42) * mm, "end": v(103.18, -27.3) * mm});
            skLineSegment(sketch, "E1135", {"start": v(103.18, -27.3) * mm, "end": v(102.88, -26.67) * mm});
            skLineSegment(sketch, "E1136", {"start": v(102.88, -26.67) * mm, "end": v(102.75, -26) * mm});
            skLineSegment(sketch, "E1137", {"start": v(102.75, -26) * mm, "end": v(102.75, -25.78) * mm});
            skLineSegment(sketch, "E1138", {"start": v(102.75, -25.78) * mm, "end": v(102.75, -25.47) * mm});
            skLineSegment(sketch, "E1139", {"start": v(102.75, -25.47) * mm, "end": v(103, -24.57) * mm});
            skLineSegment(sketch, "E1140", {"start": v(103, -24.57) * mm, "end": v(103.59, -23.76) * mm});
            skLineSegment(sketch, "E1141", {"start": v(103.59, -23.76) * mm, "end": v(103.75, -23.62) * mm});
            skLineSegment(sketch, "E1142", {"start": v(103.75, -23.62) * mm, "end": v(103.92, -23.48) * mm});
            skLineSegment(sketch, "E1143", {"start": v(103.92, -23.48) * mm, "end": v(104.92, -23) * mm});
            skLineSegment(sketch, "E1144", {"start": v(104.92, -23) * mm, "end": v(106.04, -22.78) * mm});
            skLineSegment(sketch, "E1145", {"start": v(106.04, -22.78) * mm, "end": v(106.42, -22.78) * mm});
            skLineSegment(sketch, "E1146", {"start": v(106.42, -22.78) * mm, "end": v(106.83, -22.78) * mm});
            skLineSegment(sketch, "E1147", {"start": v(106.83, -22.78) * mm, "end": v(107.92, -22.95) * mm});
            skLineSegment(sketch, "E1148", {"start": v(107.92, -22.95) * mm, "end": v(108.06, -22.98) * mm});
            skLineSegment(sketch, "E1149", {"start": v(108.06, -22.98) * mm, "end": v(108.2, -23.02) * mm});
            skLineSegment(sketch, "E1150", {"start": v(108.2, -23.02) * mm, "end": v(109.35, -23.44) * mm});
            skLineSegment(sketch, "E1151", {"start": v(109.35, -23.44) * mm, "end": v(109.45, -23.5) * mm});
            skLineSegment(sketch, "E1152", {"start": v(109.45, -23.5) * mm, "end": v(109.45, -25.26) * mm});
            skLineSegment(sketch, "E1153", {"start": v(109.45, -25.26) * mm, "end": v(109.36, -25.26) * mm});
            skLineSegment(sketch, "E1154", {"start": v(109.36, -25.26) * mm, "end": v(109.25, -25.17) * mm});
            skLineSegment(sketch, "E1155", {"start": v(109.25, -25.17) * mm, "end": v(108.08, -24.52) * mm});
            skLineSegment(sketch, "E1156", {"start": v(108.08, -24.52) * mm, "end": v(107.95, -24.47) * mm});
            skLineSegment(sketch, "E1157", {"start": v(107.95, -24.47) * mm, "end": v(107.82, -24.42) * mm});
            skLineSegment(sketch, "E1158", {"start": v(107.82, -24.42) * mm, "end": v(106.74, -24.18) * mm});
            skLineSegment(sketch, "E1159", {"start": v(106.74, -24.18) * mm, "end": v(106.38, -24.18) * mm});
            skLineSegment(sketch, "E1160", {"start": v(106.38, -24.18) * mm, "end": v(106.03, -24.18) * mm});
            skLineSegment(sketch, "E1161", {"start": v(106.03, -24.18) * mm, "end": v(105.1, -24.46) * mm});
            skLineSegment(sketch, "E1162", {"start": v(105.1, -24.46) * mm, "end": v(105, -24.52) * mm});
            skLineSegment(sketch, "E1163", {"start": v(105, -24.52) * mm, "end": v(104.9, -24.58) * mm});
            skLineSegment(sketch, "E1164", {"start": v(104.9, -24.58) * mm, "end": v(104.58, -24.95) * mm});
            skLineSegment(sketch, "E1165", {"start": v(104.58, -24.95) * mm, "end": v(104.44, -25.4) * mm});
            skLineSegment(sketch, "E1166", {"start": v(104.44, -25.4) * mm, "end": v(104.44, -25.56) * mm});
            skLineSegment(sketch, "E1167", {"start": v(104.44, -25.56) * mm, "end": v(104.44, -25.79) * mm});
            skLineSegment(sketch, "E1168", {"start": v(104.44, -25.79) * mm, "end": v(104.72, -26.42) * mm});
            skLineSegment(sketch, "E1169", {"start": v(104.72, -26.42) * mm, "end": v(104.77, -26.47) * mm});
            skLineSegment(sketch, "E1170", {"start": v(104.77, -26.47) * mm, "end": v(104.83, -26.52) * mm});
            skLineSegment(sketch, "E1171", {"start": v(104.83, -26.52) * mm, "end": v(105.72, -26.94) * mm});
            skLineSegment(sketch, "E1172", {"start": v(105.72, -26.94) * mm, "end": v(105.84, -26.97) * mm});
            skLineSegment(sketch, "E1173", {"start": v(105.84, -26.97) * mm, "end": v(105.9, -26.99) * mm});
            skLineSegment(sketch, "E1174", {"start": v(105.9, -26.99) * mm, "end": v(106.6, -27.14) * mm});
            skLineSegment(sketch, "E1175", {"start": v(106.6, -27.14) * mm, "end": v(106.67, -27.16) * mm});
            skLineSegment(sketch, "E1176", {"start": v(106.67, -27.16) * mm, "end": v(106.74, -27.17) * mm});
            skLineSegment(sketch, "E1177", {"start": v(106.74, -27.17) * mm, "end": v(107.54, -27.35) * mm});
            skLineSegment(sketch, "E1178", {"start": v(107.54, -27.35) * mm, "end": v(107.62, -27.38) * mm});
            skLineSegment(sketch, "E1179", {"start": v(107.62, -27.38) * mm, "end": v(107.8, -27.42) * mm});
            skLineSegment(sketch, "E1180", {"start": v(107.8, -27.42) * mm, "end": v(108.57, -27.74) * mm});
            skLineSegment(sketch, "E1181", {"start": v(108.57, -27.74) * mm, "end": v(109.16, -28.17) * mm});
            skLineSegment(sketch, "E1182", {"start": v(109.16, -28.17) * mm, "end": v(109.26, -28.28) * mm});
            skLineSegment(sketch, "E1183", {"start": v(109.26, -28.28) * mm, "end": v(109.35, -28.38) * mm});
            skLineSegment(sketch, "E1184", {"start": v(109.35, -28.38) * mm, "end": v(109.67, -29.03) * mm});
            skLineSegment(sketch, "E1185", {"start": v(109.67, -29.03) * mm, "end": v(109.8, -29.76) * mm});
            skLineSegment(sketch, "E1186", {"start": v(109.8, -29.76) * mm, "end": v(109.8, -30) * mm});
            skLineSegment(sketch, "E1187", {"start": v(109.8, -30) * mm, "end": v(109.8, -30.3) * mm});
            skLineSegment(sketch, "E1188", {"start": v(109.8, -30.3) * mm, "end": v(109.6, -31.1) * mm});
            skLineSegment(sketch, "E1189", {"start": v(109.6, -31.1) * mm, "end": v(109.55, -31.2) * mm});
            skLineSegment(sketch, "E1190", {"start": v(109.55, -31.2) * mm, "end": v(109.51, -31.3) * mm});
            skLineSegment(sketch, "E1191", {"start": v(109.51, -31.3) * mm, "end": v(108.9, -32.1) * mm});
            skLineSegment(sketch, "E1192", {"start": v(108.9, -32.1) * mm, "end": v(108.82, -32.17) * mm});
            skLineSegment(sketch, "E1193", {"start": v(108.82, -32.17) * mm, "end": v(108.73, -32.24) * mm});
            skLineSegment(sketch, "E1194", {"start": v(108.73, -32.24) * mm, "end": v(107.74, -32.8) * mm});
            skLineSegment(sketch, "E1195", {"start": v(107.74, -32.8) * mm, "end": v(107.63, -32.84) * mm});
            skLineSegment(sketch, "E1196", {"start": v(107.63, -32.84) * mm, "end": v(107.52, -32.88) * mm});
            skLineSegment(sketch, "E1197", {"start": v(107.52, -32.88) * mm, "end": v(106.35, -33.07) * mm});
            skLineSegment(sketch, "E1198", {"start": v(106.35, -33.07) * mm, "end": v(105.97, -33.07) * mm});
            skLineSegment(sketch, "E1199", {"start": v(115.52, -33.07) * mm, "end": v(115.06, -33.07) * mm});
            skLineSegment(sketch, "E1200", {"start": v(115.06, -33.07) * mm, "end": v(113.82, -32.85) * mm});
            skLineSegment(sketch, "E1201", {"start": v(113.82, -32.85) * mm, "end": v(113.68, -32.8) * mm});
            skLineSegment(sketch, "E1202", {"start": v(113.68, -32.8) * mm, "end": v(113.54, -32.76) * mm});
            skLineSegment(sketch, "E1203", {"start": v(113.54, -32.76) * mm, "end": v(112.36, -32.3) * mm});
            skLineSegment(sketch, "E1204", {"start": v(112.36, -32.3) * mm, "end": v(112.27, -32.24) * mm});
            skLineSegment(sketch, "E1205", {"start": v(112.27, -32.24) * mm, "end": v(112.27, -30.39) * mm});
            skLineSegment(sketch, "E1206", {"start": v(112.27, -30.39) * mm, "end": v(112.35, -30.39) * mm});
            skLineSegment(sketch, "E1207", {"start": v(112.35, -30.39) * mm, "end": v(112.39, -30.41) * mm});
            skLineSegment(sketch, "E1208", {"start": v(112.39, -30.41) * mm, "end": v(112.8, -30.72) * mm});
            skLineSegment(sketch, "E1209", {"start": v(112.8, -30.72) * mm, "end": v(112.85, -30.76) * mm});
            skLineSegment(sketch, "E1210", {"start": v(112.85, -30.76) * mm, "end": v(112.9, -30.79) * mm});
            skLineSegment(sketch, "E1211", {"start": v(112.9, -30.79) * mm, "end": v(113.53, -31.14) * mm});
            skLineSegment(sketch, "E1212", {"start": v(113.53, -31.14) * mm, "end": v(113.6, -31.18) * mm});
            skLineSegment(sketch, "E1213", {"start": v(113.6, -31.18) * mm, "end": v(113.68, -31.2) * mm});
            skLineSegment(sketch, "E1214", {"start": v(113.68, -31.2) * mm, "end": v(114.45, -31.5) * mm});
            skLineSegment(sketch, "E1215", {"start": v(114.45, -31.5) * mm, "end": v(114.53, -31.52) * mm});
            skLineSegment(sketch, "E1216", {"start": v(114.53, -31.52) * mm, "end": v(114.62, -31.54) * mm});
            skLineSegment(sketch, "E1217", {"start": v(114.62, -31.54) * mm, "end": v(115.34, -31.67) * mm});
            skLineSegment(sketch, "E1218", {"start": v(115.34, -31.67) * mm, "end": v(115.58, -31.67) * mm});
            skLineSegment(sketch, "E1219", {"start": v(115.58, -31.67) * mm, "end": v(115.8, -31.67) * mm});
            skLineSegment(sketch, "E1220", {"start": v(115.8, -31.67) * mm, "end": v(116.35, -31.6) * mm});
            skLineSegment(sketch, "E1221", {"start": v(116.35, -31.6) * mm, "end": v(116.43, -31.58) * mm});
            skLineSegment(sketch, "E1222", {"start": v(116.43, -31.58) * mm, "end": v(116.5, -31.56) * mm});
            skLineSegment(sketch, "E1223", {"start": v(116.5, -31.56) * mm, "end": v(117.06, -31.37) * mm});
            skLineSegment(sketch, "E1224", {"start": v(117.06, -31.37) * mm, "end": v(117.1, -31.34) * mm});
            skLineSegment(sketch, "E1225", {"start": v(117.1, -31.34) * mm, "end": v(117.14, -31.31) * mm});
            skLineSegment(sketch, "E1226", {"start": v(117.14, -31.31) * mm, "end": v(117.52, -30.95) * mm});
            skLineSegment(sketch, "E1227", {"start": v(117.52, -30.95) * mm, "end": v(117.54, -30.91) * mm});
            skLineSegment(sketch, "E1228", {"start": v(117.54, -30.91) * mm, "end": v(117.56, -30.87) * mm});
            skLineSegment(sketch, "E1229", {"start": v(117.56, -30.87) * mm, "end": v(117.67, -30.39) * mm});
            skLineSegment(sketch, "E1230", {"start": v(117.67, -30.39) * mm, "end": v(117.67, -30.23) * mm});
            skLineSegment(sketch, "E1231", {"start": v(117.67, -30.23) * mm, "end": v(117.67, -30) * mm});
            skLineSegment(sketch, "E1232", {"start": v(117.67, -30) * mm, "end": v(117.4, -29.4) * mm});
            skLineSegment(sketch, "E1233", {"start": v(117.4, -29.4) * mm, "end": v(117.35, -29.34) * mm});
            skLineSegment(sketch, "E1234", {"start": v(117.35, -29.34) * mm, "end": v(117.3, -29.3) * mm});
            skLineSegment(sketch, "E1235", {"start": v(117.3, -29.3) * mm, "end": v(116.35, -28.88) * mm});
            skLineSegment(sketch, "E1236", {"start": v(116.35, -28.88) * mm, "end": v(116.21, -28.84) * mm});
            skLineSegment(sketch, "E1237", {"start": v(116.21, -28.84) * mm, "end": v(116.16, -28.83) * mm});
            skLineSegment(sketch, "E1238", {"start": v(116.16, -28.83) * mm, "end": v(115.47, -28.67) * mm});
            skLineSegment(sketch, "E1239", {"start": v(115.47, -28.67) * mm, "end": v(115.39, -28.66) * mm});
            skLineSegment(sketch, "E1240", {"start": v(115.39, -28.66) * mm, "end": v(115.3, -28.64) * mm});
            skLineSegment(sketch, "E1241", {"start": v(115.3, -28.64) * mm, "end": v(114.52, -28.45) * mm});
            skLineSegment(sketch, "E1242", {"start": v(114.52, -28.45) * mm, "end": v(114.45, -28.43) * mm});
            skLineSegment(sketch, "E1243", {"start": v(114.45, -28.43) * mm, "end": v(114.26, -28.37) * mm});
            skLineSegment(sketch, "E1244", {"start": v(114.26, -28.37) * mm, "end": v(113.48, -28.02) * mm});
            skLineSegment(sketch, "E1245", {"start": v(113.48, -28.02) * mm, "end": v(112.9, -27.54) * mm});
            skLineSegment(sketch, "E1246", {"start": v(112.9, -27.54) * mm, "end": v(112.82, -27.42) * mm});
            skLineSegment(sketch, "E1247", {"start": v(112.82, -27.42) * mm, "end": v(112.73, -27.3) * mm});
            skLineSegment(sketch, "E1248", {"start": v(112.73, -27.3) * mm, "end": v(112.44, -26.67) * mm});
            skLineSegment(sketch, "E1249", {"start": v(112.44, -26.67) * mm, "end": v(112.3, -26) * mm});
            skLineSegment(sketch, "E1250", {"start": v(112.3, -26) * mm, "end": v(112.3, -25.78) * mm});
            skLineSegment(sketch, "E1251", {"start": v(112.3, -25.78) * mm, "end": v(112.3, -25.47) * mm});
            skLineSegment(sketch, "E1252", {"start": v(112.3, -25.47) * mm, "end": v(112.56, -24.57) * mm});
            skLineSegment(sketch, "E1253", {"start": v(112.56, -24.57) * mm, "end": v(113.14, -23.76) * mm});
            skLineSegment(sketch, "E1254", {"start": v(113.14, -23.76) * mm, "end": v(113.3, -23.62) * mm});
            skLineSegment(sketch, "E1255", {"start": v(113.3, -23.62) * mm, "end": v(113.48, -23.48) * mm});
            skLineSegment(sketch, "E1256", {"start": v(113.48, -23.48) * mm, "end": v(114.47, -23) * mm});
            skLineSegment(sketch, "E1257", {"start": v(114.47, -23) * mm, "end": v(115.6, -22.78) * mm});
            skLineSegment(sketch, "E1258", {"start": v(115.6, -22.78) * mm, "end": v(115.97, -22.78) * mm});
            skLineSegment(sketch, "E1259", {"start": v(115.97, -22.78) * mm, "end": v(116.38, -22.78) * mm});
            skLineSegment(sketch, "E1260", {"start": v(116.38, -22.78) * mm, "end": v(117.47, -22.95) * mm});
            skLineSegment(sketch, "E1261", {"start": v(117.47, -22.95) * mm, "end": v(117.61, -22.98) * mm});
            skLineSegment(sketch, "E1262", {"start": v(117.61, -22.98) * mm, "end": v(117.75, -23.02) * mm});
            skLineSegment(sketch, "E1263", {"start": v(117.75, -23.02) * mm, "end": v(118.9, -23.44) * mm});
            skLineSegment(sketch, "E1264", {"start": v(118.9, -23.44) * mm, "end": v(119, -23.5) * mm});
            skLineSegment(sketch, "E1265", {"start": v(119, -23.5) * mm, "end": v(119, -25.26) * mm});
            skLineSegment(sketch, "E1266", {"start": v(119, -25.26) * mm, "end": v(118.91, -25.26) * mm});
            skLineSegment(sketch, "E1267", {"start": v(118.91, -25.26) * mm, "end": v(118.8, -25.17) * mm});
            skLineSegment(sketch, "E1268", {"start": v(118.8, -25.17) * mm, "end": v(117.63, -24.52) * mm});
            skLineSegment(sketch, "E1269", {"start": v(117.63, -24.52) * mm, "end": v(117.5, -24.47) * mm});
            skLineSegment(sketch, "E1270", {"start": v(117.5, -24.47) * mm, "end": v(117.37, -24.42) * mm});
            skLineSegment(sketch, "E1271", {"start": v(117.37, -24.42) * mm, "end": v(116.3, -24.18) * mm});
            skLineSegment(sketch, "E1272", {"start": v(116.3, -24.18) * mm, "end": v(115.94, -24.18) * mm});
            skLineSegment(sketch, "E1273", {"start": v(115.94, -24.18) * mm, "end": v(115.59, -24.18) * mm});
            skLineSegment(sketch, "E1274", {"start": v(115.59, -24.18) * mm, "end": v(114.65, -24.46) * mm});
            skLineSegment(sketch, "E1275", {"start": v(114.65, -24.46) * mm, "end": v(114.56, -24.52) * mm});
            skLineSegment(sketch, "E1276", {"start": v(114.56, -24.52) * mm, "end": v(114.46, -24.58) * mm});
            skLineSegment(sketch, "E1277", {"start": v(114.46, -24.58) * mm, "end": v(114.13, -24.95) * mm});
            skLineSegment(sketch, "E1278", {"start": v(114.13, -24.95) * mm, "end": v(114, -25.4) * mm});
            skLineSegment(sketch, "E1279", {"start": v(114, -25.4) * mm, "end": v(114, -25.56) * mm});
            skLineSegment(sketch, "E1280", {"start": v(114, -25.56) * mm, "end": v(114, -25.79) * mm});
            skLineSegment(sketch, "E1281", {"start": v(114, -25.79) * mm, "end": v(114.27, -26.42) * mm});
            skLineSegment(sketch, "E1282", {"start": v(114.27, -26.42) * mm, "end": v(114.33, -26.47) * mm});
            skLineSegment(sketch, "E1283", {"start": v(114.33, -26.47) * mm, "end": v(114.38, -26.52) * mm});
            skLineSegment(sketch, "E1284", {"start": v(114.38, -26.52) * mm, "end": v(115.27, -26.94) * mm});
            skLineSegment(sketch, "E1285", {"start": v(115.27, -26.94) * mm, "end": v(115.4, -26.97) * mm});
            skLineSegment(sketch, "E1286", {"start": v(115.4, -26.97) * mm, "end": v(115.46, -26.99) * mm});
            skLineSegment(sketch, "E1287", {"start": v(115.46, -26.99) * mm, "end": v(116.15, -27.14) * mm});
            skLineSegment(sketch, "E1288", {"start": v(116.15, -27.14) * mm, "end": v(116.22, -27.16) * mm});
            skLineSegment(sketch, "E1289", {"start": v(116.22, -27.16) * mm, "end": v(116.3, -27.17) * mm});
            skLineSegment(sketch, "E1290", {"start": v(116.3, -27.17) * mm, "end": v(117.09, -27.35) * mm});
            skLineSegment(sketch, "E1291", {"start": v(117.09, -27.35) * mm, "end": v(117.17, -27.38) * mm});
            skLineSegment(sketch, "E1292", {"start": v(117.17, -27.38) * mm, "end": v(117.36, -27.42) * mm});
            skLineSegment(sketch, "E1293", {"start": v(117.36, -27.42) * mm, "end": v(118.12, -27.74) * mm});
            skLineSegment(sketch, "E1294", {"start": v(118.12, -27.74) * mm, "end": v(118.72, -28.17) * mm});
            skLineSegment(sketch, "E1295", {"start": v(118.72, -28.17) * mm, "end": v(118.81, -28.28) * mm});
            skLineSegment(sketch, "E1296", {"start": v(118.81, -28.28) * mm, "end": v(118.9, -28.38) * mm});
            skLineSegment(sketch, "E1297", {"start": v(118.9, -28.38) * mm, "end": v(119.22, -29.03) * mm});
            skLineSegment(sketch, "E1298", {"start": v(119.22, -29.03) * mm, "end": v(119.36, -29.76) * mm});
            skLineSegment(sketch, "E1299", {"start": v(119.36, -29.76) * mm, "end": v(119.36, -30) * mm});
            skLineSegment(sketch, "E1300", {"start": v(119.36, -30) * mm, "end": v(119.36, -30.3) * mm});
            skLineSegment(sketch, "E1301", {"start": v(119.36, -30.3) * mm, "end": v(119.15, -31.1) * mm});
            skLineSegment(sketch, "E1302", {"start": v(119.15, -31.1) * mm, "end": v(119.1, -31.2) * mm});
            skLineSegment(sketch, "E1303", {"start": v(119.1, -31.2) * mm, "end": v(119.07, -31.3) * mm});
            skLineSegment(sketch, "E1304", {"start": v(119.07, -31.3) * mm, "end": v(118.46, -32.1) * mm});
            skLineSegment(sketch, "E1305", {"start": v(118.46, -32.1) * mm, "end": v(118.38, -32.17) * mm});
            skLineSegment(sketch, "E1306", {"start": v(118.38, -32.17) * mm, "end": v(118.29, -32.24) * mm});
            skLineSegment(sketch, "E1307", {"start": v(118.29, -32.24) * mm, "end": v(117.3, -32.8) * mm});
            skLineSegment(sketch, "E1308", {"start": v(117.3, -32.8) * mm, "end": v(117.18, -32.84) * mm});
            skLineSegment(sketch, "E1309", {"start": v(117.18, -32.84) * mm, "end": v(117.08, -32.88) * mm});
            skLineSegment(sketch, "E1310", {"start": v(117.08, -32.88) * mm, "end": v(115.9, -33.07) * mm});
            skLineSegment(sketch, "E1311", {"start": v(115.9, -33.07) * mm, "end": v(115.52, -33.07) * mm});
            skLineSegment(sketch, "E1312", {"start": v(124.11, -32.83) * mm, "end": v(122.46, -32.83) * mm});
            skLineSegment(sketch, "E1313", {"start": v(122.46, -32.83) * mm, "end": v(122.46, -23.02) * mm});
            skLineSegment(sketch, "E1314", {"start": v(122.46, -23.02) * mm, "end": v(124.11, -23.02) * mm});
            skLineSegment(sketch, "E1315", {"start": v(124.11, -23.02) * mm, "end": v(124.11, -32.83) * mm});
            skLineSegment(sketch, "E1316", {"start": v(124.23, -21.38) * mm, "end": v(122.35, -21.38) * mm});
            skLineSegment(sketch, "E1317", {"start": v(122.35, -21.38) * mm, "end": v(122.35, -19.66) * mm});
            skLineSegment(sketch, "E1318", {"start": v(122.35, -19.66) * mm, "end": v(124.23, -19.66) * mm});
            skLineSegment(sketch, "E1319", {"start": v(124.23, -19.66) * mm, "end": v(124.23, -21.38) * mm});
            skLineSegment(sketch, "E1320", {"start": v(134.43, -27.93) * mm, "end": v(134.43, -27.51) * mm});
            skLineSegment(sketch, "E1321", {"start": v(134.43, -27.51) * mm, "end": v(134.26, -26.27) * mm});
            skLineSegment(sketch, "E1322", {"start": v(134.26, -26.27) * mm, "end": v(133.85, -25.25) * mm});
            skLineSegment(sketch, "E1323", {"start": v(133.85, -25.25) * mm, "end": v(133.74, -25.1) * mm});
            skLineSegment(sketch, "E1324", {"start": v(133.74, -25.1) * mm, "end": v(133.62, -24.94) * mm});
            skLineSegment(sketch, "E1325", {"start": v(133.62, -24.94) * mm, "end": v(132.9, -24.4) * mm});
            skLineSegment(sketch, "E1326", {"start": v(132.9, -24.4) * mm, "end": v(132.04, -24.17) * mm});
            skLineSegment(sketch, "E1327", {"start": v(132.04, -24.17) * mm, "end": v(131.76, -24.17) * mm});
            skLineSegment(sketch, "E1328", {"start": v(131.76, -24.17) * mm, "end": v(131.48, -24.17) * mm});
            skLineSegment(sketch, "E1329", {"start": v(131.48, -24.17) * mm, "end": v(130.62, -24.4) * mm});
            skLineSegment(sketch, "E1330", {"start": v(130.62, -24.4) * mm, "end": v(129.89, -24.94) * mm});
            skLineSegment(sketch, "E1331", {"start": v(129.89, -24.94) * mm, "end": v(129.77, -25.1) * mm});
            skLineSegment(sketch, "E1332", {"start": v(129.77, -25.1) * mm, "end": v(129.65, -25.25) * mm});
            skLineSegment(sketch, "E1333", {"start": v(129.65, -25.25) * mm, "end": v(129.25, -26.27) * mm});
            skLineSegment(sketch, "E1334", {"start": v(129.25, -26.27) * mm, "end": v(129.07, -27.51) * mm});
            skLineSegment(sketch, "E1335", {"start": v(129.07, -27.51) * mm, "end": v(129.07, -27.93) * mm});
            skLineSegment(sketch, "E1336", {"start": v(129.07, -27.93) * mm, "end": v(129.07, -28.33) * mm});
            skLineSegment(sketch, "E1337", {"start": v(129.07, -28.33) * mm, "end": v(129.25, -29.55) * mm});
            skLineSegment(sketch, "E1338", {"start": v(129.25, -29.55) * mm, "end": v(129.65, -30.57) * mm});
            skLineSegment(sketch, "E1339", {"start": v(129.65, -30.57) * mm, "end": v(129.77, -30.72) * mm});
            skLineSegment(sketch, "E1340", {"start": v(129.77, -30.72) * mm, "end": v(129.89, -30.88) * mm});
            skLineSegment(sketch, "E1341", {"start": v(129.89, -30.88) * mm, "end": v(130.62, -31.44) * mm});
            skLineSegment(sketch, "E1342", {"start": v(130.62, -31.44) * mm, "end": v(131.48, -31.68) * mm});
            skLineSegment(sketch, "E1343", {"start": v(131.48, -31.68) * mm, "end": v(131.76, -31.68) * mm});
            skLineSegment(sketch, "E1344", {"start": v(131.76, -31.68) * mm, "end": v(132.04, -31.68) * mm});
            skLineSegment(sketch, "E1345", {"start": v(132.04, -31.68) * mm, "end": v(132.89, -31.44) * mm});
            skLineSegment(sketch, "E1346", {"start": v(132.89, -31.44) * mm, "end": v(133.61, -30.9) * mm});
            skLineSegment(sketch, "E1347", {"start": v(133.61, -30.9) * mm, "end": v(133.73, -30.74) * mm});
            skLineSegment(sketch, "E1348", {"start": v(133.73, -30.74) * mm, "end": v(133.85, -30.59) * mm});
            skLineSegment(sketch, "E1349", {"start": v(133.85, -30.59) * mm, "end": v(134.25, -29.57) * mm});
            skLineSegment(sketch, "E1350", {"start": v(134.25, -29.57) * mm, "end": v(134.43, -28.34) * mm});
            skLineSegment(sketch, "E1351", {"start": v(134.43, -28.34) * mm, "end": v(134.43, -27.93) * mm});
            skLineSegment(sketch, "E1352", {"start": v(136.13, -27.93) * mm, "end": v(136.13, -28.48) * mm});
            skLineSegment(sketch, "E1353", {"start": v(136.13, -28.48) * mm, "end": v(135.83, -30.12) * mm});
            skLineSegment(sketch, "E1354", {"start": v(135.83, -30.12) * mm, "end": v(135.14, -31.53) * mm});
            skLineSegment(sketch, "E1355", {"start": v(135.14, -31.53) * mm, "end": v(134.94, -31.75) * mm});
            skLineSegment(sketch, "E1356", {"start": v(134.94, -31.75) * mm, "end": v(134.74, -31.98) * mm});
            skLineSegment(sketch, "E1357", {"start": v(134.74, -31.98) * mm, "end": v(133.55, -32.76) * mm});
            skLineSegment(sketch, "E1358", {"start": v(133.55, -32.76) * mm, "end": v(132.2, -33.1) * mm});
            skLineSegment(sketch, "E1359", {"start": v(132.2, -33.1) * mm, "end": v(131.76, -33.1) * mm});
            skLineSegment(sketch, "E1360", {"start": v(131.76, -33.1) * mm, "end": v(131.3, -33.1) * mm});
            skLineSegment(sketch, "E1361", {"start": v(131.3, -33.1) * mm, "end": v(129.93, -32.75) * mm});
            skLineSegment(sketch, "E1362", {"start": v(129.93, -32.75) * mm, "end": v(128.74, -31.94) * mm});
            skLineSegment(sketch, "E1363", {"start": v(128.74, -31.94) * mm, "end": v(128.54, -31.7) * mm});
            skLineSegment(sketch, "E1364", {"start": v(128.54, -31.7) * mm, "end": v(128.35, -31.48) * mm});
            skLineSegment(sketch, "E1365", {"start": v(128.35, -31.48) * mm, "end": v(127.66, -30.07) * mm});
            skLineSegment(sketch, "E1366", {"start": v(127.66, -30.07) * mm, "end": v(127.37, -28.46) * mm});
            skLineSegment(sketch, "E1367", {"start": v(127.37, -28.46) * mm, "end": v(127.37, -27.93) * mm});
            skLineSegment(sketch, "E1368", {"start": v(127.37, -27.93) * mm, "end": v(127.37, -27.38) * mm});
            skLineSegment(sketch, "E1369", {"start": v(127.37, -27.38) * mm, "end": v(127.67, -25.74) * mm});
            skLineSegment(sketch, "E1370", {"start": v(127.67, -25.74) * mm, "end": v(128.38, -24.33) * mm});
            skLineSegment(sketch, "E1371", {"start": v(128.38, -24.33) * mm, "end": v(128.58, -24.1) * mm});
            skLineSegment(sketch, "E1372", {"start": v(128.58, -24.1) * mm, "end": v(128.78, -23.88) * mm});
            skLineSegment(sketch, "E1373", {"start": v(128.78, -23.88) * mm, "end": v(129.98, -23.09) * mm});
            skLineSegment(sketch, "E1374", {"start": v(129.98, -23.09) * mm, "end": v(131.32, -22.75) * mm});
            skLineSegment(sketch, "E1375", {"start": v(131.32, -22.75) * mm, "end": v(131.76, -22.75) * mm});
            skLineSegment(sketch, "E1376", {"start": v(131.76, -22.75) * mm, "end": v(132.2, -22.75) * mm});
            skLineSegment(sketch, "E1377", {"start": v(132.2, -22.75) * mm, "end": v(133.55, -23.09) * mm});
            skLineSegment(sketch, "E1378", {"start": v(133.55, -23.09) * mm, "end": v(134.74, -23.88) * mm});
            skLineSegment(sketch, "E1379", {"start": v(134.74, -23.88) * mm, "end": v(134.94, -24.1) * mm});
            skLineSegment(sketch, "E1380", {"start": v(134.94, -24.1) * mm, "end": v(135.14, -24.33) * mm});
            skLineSegment(sketch, "E1381", {"start": v(135.14, -24.33) * mm, "end": v(135.83, -25.74) * mm});
            skLineSegment(sketch, "E1382", {"start": v(135.83, -25.74) * mm, "end": v(136.13, -27.38) * mm});
            skLineSegment(sketch, "E1383", {"start": v(136.13, -27.38) * mm, "end": v(136.13, -27.93) * mm});
            skLineSegment(sketch, "E1384", {"start": v(147.07, -32.83) * mm, "end": v(145.42, -32.83) * mm});
            skLineSegment(sketch, "E1385", {"start": v(145.42, -32.83) * mm, "end": v(145.42, -27.24) * mm});
            skLineSegment(sketch, "E1386", {"start": v(145.42, -27.24) * mm, "end": v(145.42, -26.93) * mm});
            skLineSegment(sketch, "E1387", {"start": v(145.42, -26.93) * mm, "end": v(145.36, -26.08) * mm});
            skLineSegment(sketch, "E1388", {"start": v(145.36, -26.08) * mm, "end": v(145.35, -25.98) * mm});
            skLineSegment(sketch, "E1389", {"start": v(145.35, -25.98) * mm, "end": v(145.34, -25.89) * mm});
            skLineSegment(sketch, "E1390", {"start": v(145.34, -25.89) * mm, "end": v(145.13, -25.1) * mm});
            skLineSegment(sketch, "E1391", {"start": v(145.13, -25.1) * mm, "end": v(145.1, -25.05) * mm});
            skLineSegment(sketch, "E1392", {"start": v(145.1, -25.05) * mm, "end": v(145.07, -24.99) * mm});
            skLineSegment(sketch, "E1393", {"start": v(145.07, -24.99) * mm, "end": v(144.6, -24.53) * mm});
            skLineSegment(sketch, "E1394", {"start": v(144.6, -24.53) * mm, "end": v(144.54, -24.5) * mm});
            skLineSegment(sketch, "E1395", {"start": v(144.54, -24.5) * mm, "end": v(144.48, -24.47) * mm});
            skLineSegment(sketch, "E1396", {"start": v(144.48, -24.47) * mm, "end": v(143.78, -24.32) * mm});
            skLineSegment(sketch, "E1397", {"start": v(143.78, -24.32) * mm, "end": v(143.56, -24.32) * mm});
            skLineSegment(sketch, "E1398", {"start": v(143.56, -24.32) * mm, "end": v(143.24, -24.32) * mm});
            skLineSegment(sketch, "E1399", {"start": v(143.24, -24.32) * mm, "end": v(142.4, -24.6) * mm});
            skLineSegment(sketch, "E1400", {"start": v(142.4, -24.6) * mm, "end": v(142.29, -24.65) * mm});
            skLineSegment(sketch, "E1401", {"start": v(142.29, -24.65) * mm, "end": v(142.18, -24.7) * mm});
            skLineSegment(sketch, "E1402", {"start": v(142.18, -24.7) * mm, "end": v(141.11, -25.42) * mm});
            skLineSegment(sketch, "E1403", {"start": v(141.11, -25.42) * mm, "end": v(141, -25.5) * mm});
            skLineSegment(sketch, "E1404", {"start": v(141, -25.5) * mm, "end": v(141, -32.83) * mm});
            skLineSegment(sketch, "E1405", {"start": v(141, -32.83) * mm, "end": v(139.36, -32.83) * mm});
            skLineSegment(sketch, "E1406", {"start": v(139.36, -32.83) * mm, "end": v(139.36, -23.02) * mm});
            skLineSegment(sketch, "E1407", {"start": v(139.36, -23.02) * mm, "end": v(141, -23.02) * mm});
            skLineSegment(sketch, "E1408", {"start": v(141, -23.02) * mm, "end": v(141, -24.1) * mm});
            skLineSegment(sketch, "E1409", {"start": v(141, -24.1) * mm, "end": v(141.13, -24) * mm});
            skLineSegment(sketch, "E1410", {"start": v(141.13, -24) * mm, "end": v(142.35, -23.16) * mm});
            skLineSegment(sketch, "E1411", {"start": v(142.35, -23.16) * mm, "end": v(142.47, -23.1) * mm});
            skLineSegment(sketch, "E1412", {"start": v(142.47, -23.1) * mm, "end": v(142.58, -23.04) * mm});
            skLineSegment(sketch, "E1413", {"start": v(142.58, -23.04) * mm, "end": v(143.63, -22.75) * mm});
            skLineSegment(sketch, "E1414", {"start": v(143.63, -22.75) * mm, "end": v(143.98, -22.75) * mm});
            skLineSegment(sketch, "E1415", {"start": v(143.98, -22.75) * mm, "end": v(144.3, -22.75) * mm});
            skLineSegment(sketch, "E1416", {"start": v(144.3, -22.75) * mm, "end": v(145.27, -22.99) * mm});
            skLineSegment(sketch, "E1417", {"start": v(145.27, -22.99) * mm, "end": v(146.12, -23.54) * mm});
            skLineSegment(sketch, "E1418", {"start": v(146.12, -23.54) * mm, "end": v(146.25, -23.7) * mm});
            skLineSegment(sketch, "E1419", {"start": v(146.25, -23.7) * mm, "end": v(146.39, -23.86) * mm});
            skLineSegment(sketch, "E1420", {"start": v(146.39, -23.86) * mm, "end": v(146.86, -24.87) * mm});
            skLineSegment(sketch, "E1421", {"start": v(146.86, -24.87) * mm, "end": v(147.07, -26.06) * mm});
            skLineSegment(sketch, "E1422", {"start": v(147.07, -26.06) * mm, "end": v(147.07, -26.46) * mm});
            skLineSegment(sketch, "E1423", {"start": v(147.07, -26.46) * mm, "end": v(147.07, -32.83) * mm});
            skLineSegment(sketch, "E1424", {"start": v(-73.55, -33.07) * mm, "end": v(-74.01, -33.07) * mm});
            skLineSegment(sketch, "E1425", {"start": v(-74.01, -33.07) * mm, "end": v(-75.25, -32.85) * mm});
            skLineSegment(sketch, "E1426", {"start": v(-75.25, -32.85) * mm, "end": v(-75.4, -32.8) * mm});
            skLineSegment(sketch, "E1427", {"start": v(-75.4, -32.8) * mm, "end": v(-75.53, -32.76) * mm});
            skLineSegment(sketch, "E1428", {"start": v(-75.53, -32.76) * mm, "end": v(-76.72, -32.3) * mm});
            skLineSegment(sketch, "E1429", {"start": v(-76.72, -32.3) * mm, "end": v(-76.8, -32.24) * mm});
            skLineSegment(sketch, "E1430", {"start": v(-76.8, -32.24) * mm, "end": v(-76.8, -30.39) * mm});
            skLineSegment(sketch, "E1431", {"start": v(-76.8, -30.39) * mm, "end": v(-76.72, -30.39) * mm});
            skLineSegment(sketch, "E1432", {"start": v(-76.72, -30.39) * mm, "end": v(-76.69, -30.41) * mm});
            skLineSegment(sketch, "E1433", {"start": v(-76.69, -30.41) * mm, "end": v(-76.27, -30.72) * mm});
            skLineSegment(sketch, "E1434", {"start": v(-76.27, -30.72) * mm, "end": v(-76.22, -30.76) * mm});
            skLineSegment(sketch, "E1435", {"start": v(-76.22, -30.76) * mm, "end": v(-76.18, -30.79) * mm});
            skLineSegment(sketch, "E1436", {"start": v(-76.18, -30.79) * mm, "end": v(-75.55, -31.14) * mm});
            skLineSegment(sketch, "E1437", {"start": v(-75.55, -31.14) * mm, "end": v(-75.47, -31.18) * mm});
            skLineSegment(sketch, "E1438", {"start": v(-75.47, -31.18) * mm, "end": v(-75.4, -31.2) * mm});
            skLineSegment(sketch, "E1439", {"start": v(-75.4, -31.2) * mm, "end": v(-74.62, -31.5) * mm});
            skLineSegment(sketch, "E1440", {"start": v(-74.62, -31.5) * mm, "end": v(-74.54, -31.52) * mm});
            skLineSegment(sketch, "E1441", {"start": v(-74.54, -31.52) * mm, "end": v(-74.45, -31.54) * mm});
            skLineSegment(sketch, "E1442", {"start": v(-74.45, -31.54) * mm, "end": v(-73.73, -31.67) * mm});
            skLineSegment(sketch, "E1443", {"start": v(-73.73, -31.67) * mm, "end": v(-73.5, -31.67) * mm});
            skLineSegment(sketch, "E1444", {"start": v(-73.5, -31.67) * mm, "end": v(-73.28, -31.67) * mm});
            skLineSegment(sketch, "E1445", {"start": v(-73.28, -31.67) * mm, "end": v(-72.72, -31.6) * mm});
            skLineSegment(sketch, "E1446", {"start": v(-72.72, -31.6) * mm, "end": v(-72.65, -31.58) * mm});
            skLineSegment(sketch, "E1447", {"start": v(-72.65, -31.58) * mm, "end": v(-72.57, -31.56) * mm});
            skLineSegment(sketch, "E1448", {"start": v(-72.57, -31.56) * mm, "end": v(-72.02, -31.37) * mm});
            skLineSegment(sketch, "E1449", {"start": v(-72.02, -31.37) * mm, "end": v(-71.98, -31.34) * mm});
            skLineSegment(sketch, "E1450", {"start": v(-71.98, -31.34) * mm, "end": v(-71.93, -31.31) * mm});
            skLineSegment(sketch, "E1451", {"start": v(-71.93, -31.31) * mm, "end": v(-71.56, -30.95) * mm});
            skLineSegment(sketch, "E1452", {"start": v(-71.56, -30.95) * mm, "end": v(-71.54, -30.91) * mm});
            skLineSegment(sketch, "E1453", {"start": v(-71.54, -30.91) * mm, "end": v(-71.51, -30.87) * mm});
            skLineSegment(sketch, "E1454", {"start": v(-71.51, -30.87) * mm, "end": v(-71.4, -30.39) * mm});
            skLineSegment(sketch, "E1455", {"start": v(-71.4, -30.39) * mm, "end": v(-71.4, -30.23) * mm});
            skLineSegment(sketch, "E1456", {"start": v(-71.4, -30.23) * mm, "end": v(-71.4, -30) * mm});
            skLineSegment(sketch, "E1457", {"start": v(-71.4, -30) * mm, "end": v(-71.67, -29.4) * mm});
            skLineSegment(sketch, "E1458", {"start": v(-71.67, -29.4) * mm, "end": v(-71.72, -29.34) * mm});
            skLineSegment(sketch, "E1459", {"start": v(-71.72, -29.34) * mm, "end": v(-71.78, -29.3) * mm});
            skLineSegment(sketch, "E1460", {"start": v(-71.78, -29.3) * mm, "end": v(-72.72, -28.88) * mm});
            skLineSegment(sketch, "E1461", {"start": v(-72.72, -28.88) * mm, "end": v(-72.86, -28.84) * mm});
            skLineSegment(sketch, "E1462", {"start": v(-72.86, -28.84) * mm, "end": v(-72.91, -28.83) * mm});
            skLineSegment(sketch, "E1463", {"start": v(-72.91, -28.83) * mm, "end": v(-73.6, -28.67) * mm});
            skLineSegment(sketch, "E1464", {"start": v(-73.6, -28.67) * mm, "end": v(-73.68, -28.66) * mm});
            skLineSegment(sketch, "E1465", {"start": v(-73.68, -28.66) * mm, "end": v(-73.77, -28.64) * mm});
            skLineSegment(sketch, "E1466", {"start": v(-73.77, -28.64) * mm, "end": v(-74.55, -28.45) * mm});
            skLineSegment(sketch, "E1467", {"start": v(-74.55, -28.45) * mm, "end": v(-74.62, -28.43) * mm});
            skLineSegment(sketch, "E1468", {"start": v(-74.62, -28.43) * mm, "end": v(-74.81, -28.37) * mm});
            skLineSegment(sketch, "E1469", {"start": v(-74.81, -28.37) * mm, "end": v(-75.6, -28.02) * mm});
            skLineSegment(sketch, "E1470", {"start": v(-75.6, -28.02) * mm, "end": v(-76.17, -27.54) * mm});
            skLineSegment(sketch, "E1471", {"start": v(-76.17, -27.54) * mm, "end": v(-76.26, -27.42) * mm});
            skLineSegment(sketch, "E1472", {"start": v(-76.26, -27.42) * mm, "end": v(-76.34, -27.3) * mm});
            skLineSegment(sketch, "E1473", {"start": v(-76.34, -27.3) * mm, "end": v(-76.64, -26.67) * mm});
            skLineSegment(sketch, "E1474", {"start": v(-76.64, -26.67) * mm, "end": v(-76.77, -26) * mm});
            skLineSegment(sketch, "E1475", {"start": v(-76.77, -26) * mm, "end": v(-76.77, -25.78) * mm});
            skLineSegment(sketch, "E1476", {"start": v(-76.77, -25.78) * mm, "end": v(-76.77, -25.47) * mm});
            skLineSegment(sketch, "E1477", {"start": v(-76.77, -25.47) * mm, "end": v(-76.52, -24.57) * mm});
            skLineSegment(sketch, "E1478", {"start": v(-76.52, -24.57) * mm, "end": v(-75.93, -23.76) * mm});
            skLineSegment(sketch, "E1479", {"start": v(-75.93, -23.76) * mm, "end": v(-75.76, -23.62) * mm});
            skLineSegment(sketch, "E1480", {"start": v(-75.76, -23.62) * mm, "end": v(-75.6, -23.48) * mm});
            skLineSegment(sketch, "E1481", {"start": v(-75.6, -23.48) * mm, "end": v(-74.6, -23) * mm});
            skLineSegment(sketch, "E1482", {"start": v(-74.6, -23) * mm, "end": v(-73.48, -22.78) * mm});
            skLineSegment(sketch, "E1483", {"start": v(-73.48, -22.78) * mm, "end": v(-73.1, -22.78) * mm});
            skLineSegment(sketch, "E1484", {"start": v(-73.1, -22.78) * mm, "end": v(-72.7, -22.78) * mm});
            skLineSegment(sketch, "E1485", {"start": v(-72.7, -22.78) * mm, "end": v(-71.6, -22.95) * mm});
            skLineSegment(sketch, "E1486", {"start": v(-71.6, -22.95) * mm, "end": v(-71.46, -22.98) * mm});
            skLineSegment(sketch, "E1487", {"start": v(-71.46, -22.98) * mm, "end": v(-71.32, -23.02) * mm});
            skLineSegment(sketch, "E1488", {"start": v(-71.32, -23.02) * mm, "end": v(-70.17, -23.44) * mm});
            skLineSegment(sketch, "E1489", {"start": v(-70.17, -23.44) * mm, "end": v(-70.07, -23.5) * mm});
            skLineSegment(sketch, "E1490", {"start": v(-70.07, -23.5) * mm, "end": v(-70.07, -25.26) * mm});
            skLineSegment(sketch, "E1491", {"start": v(-70.07, -25.26) * mm, "end": v(-70.16, -25.26) * mm});
            skLineSegment(sketch, "E1492", {"start": v(-70.16, -25.26) * mm, "end": v(-70.27, -25.17) * mm});
            skLineSegment(sketch, "E1493", {"start": v(-70.27, -25.17) * mm, "end": v(-71.44, -24.52) * mm});
            skLineSegment(sketch, "E1494", {"start": v(-71.44, -24.52) * mm, "end": v(-71.57, -24.47) * mm});
            skLineSegment(sketch, "E1495", {"start": v(-71.57, -24.47) * mm, "end": v(-71.7, -24.42) * mm});
            skLineSegment(sketch, "E1496", {"start": v(-71.7, -24.42) * mm, "end": v(-72.78, -24.18) * mm});
            skLineSegment(sketch, "E1497", {"start": v(-72.78, -24.18) * mm, "end": v(-73.14, -24.18) * mm});
            skLineSegment(sketch, "E1498", {"start": v(-73.14, -24.18) * mm, "end": v(-73.48, -24.18) * mm});
            skLineSegment(sketch, "E1499", {"start": v(-73.48, -24.18) * mm, "end": v(-74.42, -24.46) * mm});
            skLineSegment(sketch, "E1500", {"start": v(-74.42, -24.46) * mm, "end": v(-74.52, -24.52) * mm});
            skLineSegment(sketch, "E1501", {"start": v(-74.52, -24.52) * mm, "end": v(-74.61, -24.58) * mm});
            skLineSegment(sketch, "E1502", {"start": v(-74.61, -24.58) * mm, "end": v(-74.94, -24.95) * mm});
            skLineSegment(sketch, "E1503", {"start": v(-74.94, -24.95) * mm, "end": v(-75.08, -25.4) * mm});
            skLineSegment(sketch, "E1504", {"start": v(-75.08, -25.4) * mm, "end": v(-75.08, -25.56) * mm});
            skLineSegment(sketch, "E1505", {"start": v(-75.08, -25.56) * mm, "end": v(-75.08, -25.79) * mm});
            skLineSegment(sketch, "E1506", {"start": v(-75.08, -25.79) * mm, "end": v(-74.8, -26.42) * mm});
            skLineSegment(sketch, "E1507", {"start": v(-74.8, -26.42) * mm, "end": v(-74.75, -26.47) * mm});
            skLineSegment(sketch, "E1508", {"start": v(-74.75, -26.47) * mm, "end": v(-74.7, -26.52) * mm});
            skLineSegment(sketch, "E1509", {"start": v(-74.7, -26.52) * mm, "end": v(-73.8, -26.94) * mm});
            skLineSegment(sketch, "E1510", {"start": v(-73.8, -26.94) * mm, "end": v(-73.67, -26.97) * mm});
            skLineSegment(sketch, "E1511", {"start": v(-73.67, -26.97) * mm, "end": v(-73.61, -26.99) * mm});
            skLineSegment(sketch, "E1512", {"start": v(-73.61, -26.99) * mm, "end": v(-72.93, -27.14) * mm});
            skLineSegment(sketch, "E1513", {"start": v(-72.93, -27.14) * mm, "end": v(-72.85, -27.16) * mm});
            skLineSegment(sketch, "E1514", {"start": v(-72.85, -27.16) * mm, "end": v(-72.78, -27.17) * mm});
            skLineSegment(sketch, "E1515", {"start": v(-72.78, -27.17) * mm, "end": v(-71.98, -27.35) * mm});
            skLineSegment(sketch, "E1516", {"start": v(-71.98, -27.35) * mm, "end": v(-71.9, -27.38) * mm});
            skLineSegment(sketch, "E1517", {"start": v(-71.9, -27.38) * mm, "end": v(-71.72, -27.42) * mm});
            skLineSegment(sketch, "E1518", {"start": v(-71.72, -27.42) * mm, "end": v(-70.95, -27.74) * mm});
            skLineSegment(sketch, "E1519", {"start": v(-70.95, -27.74) * mm, "end": v(-70.36, -28.17) * mm});
            skLineSegment(sketch, "E1520", {"start": v(-70.36, -28.17) * mm, "end": v(-70.26, -28.28) * mm});
            skLineSegment(sketch, "E1521", {"start": v(-70.26, -28.28) * mm, "end": v(-70.17, -28.38) * mm});
            skLineSegment(sketch, "E1522", {"start": v(-70.17, -28.38) * mm, "end": v(-69.85, -29.03) * mm});
            skLineSegment(sketch, "E1523", {"start": v(-69.85, -29.03) * mm, "end": v(-69.71, -29.76) * mm});
            skLineSegment(sketch, "E1524", {"start": v(-69.71, -29.76) * mm, "end": v(-69.71, -30) * mm});
            skLineSegment(sketch, "E1525", {"start": v(-69.71, -30) * mm, "end": v(-69.71, -30.3) * mm});
            skLineSegment(sketch, "E1526", {"start": v(-69.71, -30.3) * mm, "end": v(-69.92, -31.1) * mm});
            skLineSegment(sketch, "E1527", {"start": v(-69.92, -31.1) * mm, "end": v(-69.96, -31.2) * mm});
            skLineSegment(sketch, "E1528", {"start": v(-69.96, -31.2) * mm, "end": v(-70, -31.3) * mm});
            skLineSegment(sketch, "E1529", {"start": v(-70, -31.3) * mm, "end": v(-70.62, -32.1) * mm});
            skLineSegment(sketch, "E1530", {"start": v(-70.62, -32.1) * mm, "end": v(-70.7, -32.17) * mm});
            skLineSegment(sketch, "E1531", {"start": v(-70.7, -32.17) * mm, "end": v(-70.79, -32.24) * mm});
            skLineSegment(sketch, "E1532", {"start": v(-70.79, -32.24) * mm, "end": v(-71.78, -32.8) * mm});
            skLineSegment(sketch, "E1533", {"start": v(-71.78, -32.8) * mm, "end": v(-71.89, -32.84) * mm});
            skLineSegment(sketch, "E1534", {"start": v(-71.89, -32.84) * mm, "end": v(-72, -32.88) * mm});
            skLineSegment(sketch, "E1535", {"start": v(-72, -32.88) * mm, "end": v(-73.16, -33.07) * mm});
            skLineSegment(sketch, "E1536", {"start": v(-73.16, -33.07) * mm, "end": v(-73.55, -33.07) * mm});
            skLineSegment(sketch, "E1537", {"start": v(-60.28, -27.93) * mm, "end": v(-60.28, -27.51) * mm});
            skLineSegment(sketch, "E1538", {"start": v(-60.28, -27.51) * mm, "end": v(-60.46, -26.27) * mm});
            skLineSegment(sketch, "E1539", {"start": v(-60.46, -26.27) * mm, "end": v(-60.86, -25.25) * mm});
            skLineSegment(sketch, "E1540", {"start": v(-60.86, -25.25) * mm, "end": v(-60.98, -25.1) * mm});
            skLineSegment(sketch, "E1541", {"start": v(-60.98, -25.1) * mm, "end": v(-61.1, -24.94) * mm});
            skLineSegment(sketch, "E1542", {"start": v(-61.1, -24.94) * mm, "end": v(-61.82, -24.4) * mm});
            skLineSegment(sketch, "E1543", {"start": v(-61.82, -24.4) * mm, "end": v(-62.67, -24.17) * mm});
            skLineSegment(sketch, "E1544", {"start": v(-62.67, -24.17) * mm, "end": v(-62.95, -24.17) * mm});
            skLineSegment(sketch, "E1545", {"start": v(-62.95, -24.17) * mm, "end": v(-63.24, -24.17) * mm});
            skLineSegment(sketch, "E1546", {"start": v(-63.24, -24.17) * mm, "end": v(-64.1, -24.4) * mm});
            skLineSegment(sketch, "E1547", {"start": v(-64.1, -24.4) * mm, "end": v(-64.83, -24.94) * mm});
            skLineSegment(sketch, "E1548", {"start": v(-64.83, -24.94) * mm, "end": v(-64.94, -25.1) * mm});
            skLineSegment(sketch, "E1549", {"start": v(-64.94, -25.1) * mm, "end": v(-65.06, -25.25) * mm});
            skLineSegment(sketch, "E1550", {"start": v(-65.06, -25.25) * mm, "end": v(-65.46, -26.27) * mm});
            skLineSegment(sketch, "E1551", {"start": v(-65.46, -26.27) * mm, "end": v(-65.64, -27.51) * mm});
            skLineSegment(sketch, "E1552", {"start": v(-65.64, -27.51) * mm, "end": v(-65.64, -27.93) * mm});
            skLineSegment(sketch, "E1553", {"start": v(-65.64, -27.93) * mm, "end": v(-65.64, -28.33) * mm});
            skLineSegment(sketch, "E1554", {"start": v(-65.64, -28.33) * mm, "end": v(-65.46, -29.55) * mm});
            skLineSegment(sketch, "E1555", {"start": v(-65.46, -29.55) * mm, "end": v(-65.06, -30.57) * mm});
            skLineSegment(sketch, "E1556", {"start": v(-65.06, -30.57) * mm, "end": v(-64.94, -30.72) * mm});
            skLineSegment(sketch, "E1557", {"start": v(-64.94, -30.72) * mm, "end": v(-64.83, -30.88) * mm});
            skLineSegment(sketch, "E1558", {"start": v(-64.83, -30.88) * mm, "end": v(-64.1, -31.44) * mm});
            skLineSegment(sketch, "E1559", {"start": v(-64.1, -31.44) * mm, "end": v(-63.24, -31.68) * mm});
            skLineSegment(sketch, "E1560", {"start": v(-63.24, -31.68) * mm, "end": v(-62.95, -31.68) * mm});
            skLineSegment(sketch, "E1561", {"start": v(-62.95, -31.68) * mm, "end": v(-62.67, -31.68) * mm});
            skLineSegment(sketch, "E1562", {"start": v(-62.67, -31.68) * mm, "end": v(-61.82, -31.44) * mm});
            skLineSegment(sketch, "E1563", {"start": v(-61.82, -31.44) * mm, "end": v(-61.1, -30.9) * mm});
            skLineSegment(sketch, "E1564", {"start": v(-61.1, -30.9) * mm, "end": v(-60.98, -30.74) * mm});
            skLineSegment(sketch, "E1565", {"start": v(-60.98, -30.74) * mm, "end": v(-60.86, -30.59) * mm});
            skLineSegment(sketch, "E1566", {"start": v(-60.86, -30.59) * mm, "end": v(-60.46, -29.57) * mm});
            skLineSegment(sketch, "E1567", {"start": v(-60.46, -29.57) * mm, "end": v(-60.28, -28.34) * mm});
            skLineSegment(sketch, "E1568", {"start": v(-60.28, -28.34) * mm, "end": v(-60.28, -27.93) * mm});
            skLineSegment(sketch, "E1569", {"start": v(-58.58, -27.93) * mm, "end": v(-58.58, -28.48) * mm});
            skLineSegment(sketch, "E1570", {"start": v(-58.58, -28.48) * mm, "end": v(-58.88, -30.12) * mm});
            skLineSegment(sketch, "E1571", {"start": v(-58.88, -30.12) * mm, "end": v(-59.58, -31.53) * mm});
            skLineSegment(sketch, "E1572", {"start": v(-59.58, -31.53) * mm, "end": v(-59.77, -31.75) * mm});
            skLineSegment(sketch, "E1573", {"start": v(-59.77, -31.75) * mm, "end": v(-59.97, -31.98) * mm});
            skLineSegment(sketch, "E1574", {"start": v(-59.97, -31.98) * mm, "end": v(-61.17, -32.76) * mm});
            skLineSegment(sketch, "E1575", {"start": v(-61.17, -32.76) * mm, "end": v(-62.5, -33.1) * mm});
            skLineSegment(sketch, "E1576", {"start": v(-62.5, -33.1) * mm, "end": v(-62.95, -33.1) * mm});
            skLineSegment(sketch, "E1577", {"start": v(-62.95, -33.1) * mm, "end": v(-63.4, -33.1) * mm});
            skLineSegment(sketch, "E1578", {"start": v(-63.4, -33.1) * mm, "end": v(-64.78, -32.75) * mm});
            skLineSegment(sketch, "E1579", {"start": v(-64.78, -32.75) * mm, "end": v(-65.98, -31.94) * mm});
            skLineSegment(sketch, "E1580", {"start": v(-65.98, -31.94) * mm, "end": v(-66.17, -31.7) * mm});
            skLineSegment(sketch, "E1581", {"start": v(-66.17, -31.7) * mm, "end": v(-66.37, -31.48) * mm});
            skLineSegment(sketch, "E1582", {"start": v(-66.37, -31.48) * mm, "end": v(-67.05, -30.07) * mm});
            skLineSegment(sketch, "E1583", {"start": v(-67.05, -30.07) * mm, "end": v(-67.34, -28.46) * mm});
            skLineSegment(sketch, "E1584", {"start": v(-67.34, -28.46) * mm, "end": v(-67.34, -27.93) * mm});
            skLineSegment(sketch, "E1585", {"start": v(-67.34, -27.93) * mm, "end": v(-67.34, -27.38) * mm});
            skLineSegment(sketch, "E1586", {"start": v(-67.34, -27.38) * mm, "end": v(-67.04, -25.74) * mm});
            skLineSegment(sketch, "E1587", {"start": v(-67.04, -25.74) * mm, "end": v(-66.34, -24.33) * mm});
            skLineSegment(sketch, "E1588", {"start": v(-66.34, -24.33) * mm, "end": v(-66.13, -24.1) * mm});
            skLineSegment(sketch, "E1589", {"start": v(-66.13, -24.1) * mm, "end": v(-65.93, -23.88) * mm});
            skLineSegment(sketch, "E1590", {"start": v(-65.93, -23.88) * mm, "end": v(-64.74, -23.09) * mm});
            skLineSegment(sketch, "E1591", {"start": v(-64.74, -23.09) * mm, "end": v(-63.4, -22.75) * mm});
            skLineSegment(sketch, "E1592", {"start": v(-63.4, -22.75) * mm, "end": v(-62.95, -22.75) * mm});
            skLineSegment(sketch, "E1593", {"start": v(-62.95, -22.75) * mm, "end": v(-62.5, -22.75) * mm});
            skLineSegment(sketch, "E1594", {"start": v(-62.5, -22.75) * mm, "end": v(-61.17, -23.09) * mm});
            skLineSegment(sketch, "E1595", {"start": v(-61.17, -23.09) * mm, "end": v(-59.97, -23.88) * mm});
            skLineSegment(sketch, "E1596", {"start": v(-59.97, -23.88) * mm, "end": v(-59.77, -24.1) * mm});
            skLineSegment(sketch, "E1597", {"start": v(-59.77, -24.1) * mm, "end": v(-59.58, -24.33) * mm});
            skLineSegment(sketch, "E1598", {"start": v(-59.58, -24.33) * mm, "end": v(-58.88, -25.74) * mm});
            skLineSegment(sketch, "E1599", {"start": v(-58.88, -25.74) * mm, "end": v(-58.58, -27.38) * mm});
            skLineSegment(sketch, "E1600", {"start": v(-58.58, -27.38) * mm, "end": v(-58.58, -27.93) * mm});
            skLineSegment(sketch, "E1601", {"start": v(-50.2, -20.74) * mm, "end": v(-50.28, -20.74) * mm});
            skLineSegment(sketch, "E1602", {"start": v(-50.28, -20.74) * mm, "end": v(-50.32, -20.73) * mm});
            skLineSegment(sketch, "E1603", {"start": v(-50.32, -20.73) * mm, "end": v(-50.84, -20.6) * mm});
            skLineSegment(sketch, "E1604", {"start": v(-50.84, -20.6) * mm, "end": v(-50.91, -20.6) * mm});
            skLineSegment(sketch, "E1605", {"start": v(-50.91, -20.6) * mm, "end": v(-50.98, -20.58) * mm});
            skLineSegment(sketch, "E1606", {"start": v(-50.98, -20.58) * mm, "end": v(-51.48, -20.52) * mm});
            skLineSegment(sketch, "E1607", {"start": v(-51.48, -20.52) * mm, "end": v(-51.65, -20.52) * mm});
            skLineSegment(sketch, "E1608", {"start": v(-51.65, -20.52) * mm, "end": v(-51.87, -20.52) * mm});
            skLineSegment(sketch, "E1609", {"start": v(-51.87, -20.52) * mm, "end": v(-52.54, -20.63) * mm});
            skLineSegment(sketch, "E1610", {"start": v(-52.54, -20.63) * mm, "end": v(-53.07, -20.9) * mm});
            skLineSegment(sketch, "E1611", {"start": v(-53.07, -20.9) * mm, "end": v(-53.14, -20.99) * mm});
            skLineSegment(sketch, "E1612", {"start": v(-53.14, -20.99) * mm, "end": v(-53.21, -21.06) * mm});
            skLineSegment(sketch, "E1613", {"start": v(-53.21, -21.06) * mm, "end": v(-53.47, -21.64) * mm});
            skLineSegment(sketch, "E1614", {"start": v(-53.47, -21.64) * mm, "end": v(-53.58, -22.42) * mm});
            skLineSegment(sketch, "E1615", {"start": v(-53.58, -22.42) * mm, "end": v(-53.58, -22.69) * mm});
            skLineSegment(sketch, "E1616", {"start": v(-53.58, -22.69) * mm, "end": v(-53.58, -23.02) * mm});
            skLineSegment(sketch, "E1617", {"start": v(-53.58, -23.02) * mm, "end": v(-50.85, -23.02) * mm});
            skLineSegment(sketch, "E1618", {"start": v(-50.85, -23.02) * mm, "end": v(-50.85, -24.39) * mm});
            skLineSegment(sketch, "E1619", {"start": v(-50.85, -24.39) * mm, "end": v(-53.53, -24.39) * mm});
            skLineSegment(sketch, "E1620", {"start": v(-53.53, -24.39) * mm, "end": v(-53.53, -32.83) * mm});
            skLineSegment(sketch, "E1621", {"start": v(-53.53, -32.83) * mm, "end": v(-55.18, -32.83) * mm});
            skLineSegment(sketch, "E1622", {"start": v(-55.18, -32.83) * mm, "end": v(-55.18, -24.39) * mm});
            skLineSegment(sketch, "E1623", {"start": v(-55.18, -24.39) * mm, "end": v(-56.3, -24.39) * mm});
            skLineSegment(sketch, "E1624", {"start": v(-56.3, -24.39) * mm, "end": v(-56.3, -23.02) * mm});
            skLineSegment(sketch, "E1625", {"start": v(-56.3, -23.02) * mm, "end": v(-55.18, -23.02) * mm});
            skLineSegment(sketch, "E1626", {"start": v(-55.18, -23.02) * mm, "end": v(-55.18, -22.7) * mm});
            skLineSegment(sketch, "E1627", {"start": v(-55.18, -22.7) * mm, "end": v(-55.18, -22.3) * mm});
            skLineSegment(sketch, "E1628", {"start": v(-55.18, -22.3) * mm, "end": v(-54.97, -21.13) * mm});
            skLineSegment(sketch, "E1629", {"start": v(-54.97, -21.13) * mm, "end": v(-54.47, -20.15) * mm});
            skLineSegment(sketch, "E1630", {"start": v(-54.47, -20.15) * mm, "end": v(-54.33, -20) * mm});
            skLineSegment(sketch, "E1631", {"start": v(-54.33, -20) * mm, "end": v(-54.19, -19.85) * mm});
            skLineSegment(sketch, "E1632", {"start": v(-54.19, -19.85) * mm, "end": v(-53.3, -19.3) * mm});
            skLineSegment(sketch, "E1633", {"start": v(-53.3, -19.3) * mm, "end": v(-52.24, -19.08) * mm});
            skLineSegment(sketch, "E1634", {"start": v(-52.24, -19.08) * mm, "end": v(-51.89, -19.08) * mm});
            skLineSegment(sketch, "E1635", {"start": v(-51.89, -19.08) * mm, "end": v(-51.66, -19.08) * mm});
            skLineSegment(sketch, "E1636", {"start": v(-51.66, -19.08) * mm, "end": v(-51.06, -19.12) * mm});
            skLineSegment(sketch, "E1637", {"start": v(-51.06, -19.12) * mm, "end": v(-51, -19.12) * mm});
            skLineSegment(sketch, "E1638", {"start": v(-51, -19.12) * mm, "end": v(-50.92, -19.13) * mm});
            skLineSegment(sketch, "E1639", {"start": v(-50.92, -19.13) * mm, "end": v(-50.25, -19.22) * mm});
            skLineSegment(sketch, "E1640", {"start": v(-50.25, -19.22) * mm, "end": v(-50.2, -19.23) * mm});
            skLineSegment(sketch, "E1641", {"start": v(-50.2, -19.23) * mm, "end": v(-50.2, -20.74) * mm});
            skLineSegment(sketch, "E1642", {"start": v(-45.13, -33.02) * mm, "end": v(-45.44, -33.02) * mm});
            skLineSegment(sketch, "E1643", {"start": v(-45.44, -33.02) * mm, "end": v(-46.34, -32.83) * mm});
            skLineSegment(sketch, "E1644", {"start": v(-46.34, -32.83) * mm, "end": v(-47.11, -32.38) * mm});
            skLineSegment(sketch, "E1645", {"start": v(-47.11, -32.38) * mm, "end": v(-47.24, -32.25) * mm});
            skLineSegment(sketch, "E1646", {"start": v(-47.24, -32.25) * mm, "end": v(-47.37, -32.12) * mm});
            skLineSegment(sketch, "E1647", {"start": v(-47.37, -32.12) * mm, "end": v(-47.8, -31.26) * mm});
            skLineSegment(sketch, "E1648", {"start": v(-47.8, -31.26) * mm, "end": v(-48, -30.18) * mm});
            skLineSegment(sketch, "E1649", {"start": v(-48, -30.18) * mm, "end": v(-48, -29.82) * mm});
            skLineSegment(sketch, "E1650", {"start": v(-48, -29.82) * mm, "end": v(-48, -24.39) * mm});
            skLineSegment(sketch, "E1651", {"start": v(-48, -24.39) * mm, "end": v(-49.11, -24.39) * mm});
            skLineSegment(sketch, "E1652", {"start": v(-49.11, -24.39) * mm, "end": v(-49.11, -23.02) * mm});
            skLineSegment(sketch, "E1653", {"start": v(-49.11, -23.02) * mm, "end": v(-48, -23.02) * mm});
            skLineSegment(sketch, "E1654", {"start": v(-48, -23.02) * mm, "end": v(-48, -20.2) * mm});
            skLineSegment(sketch, "E1655", {"start": v(-48, -20.2) * mm, "end": v(-46.34, -20.2) * mm});
            skLineSegment(sketch, "E1656", {"start": v(-46.34, -20.2) * mm, "end": v(-46.34, -23.02) * mm});
            skLineSegment(sketch, "E1657", {"start": v(-46.34, -23.02) * mm, "end": v(-43.3, -23.02) * mm});
            skLineSegment(sketch, "E1658", {"start": v(-43.3, -23.02) * mm, "end": v(-43.3, -24.39) * mm});
            skLineSegment(sketch, "E1659", {"start": v(-43.3, -24.39) * mm, "end": v(-46.34, -24.39) * mm});
            skLineSegment(sketch, "E1660", {"start": v(-46.34, -24.39) * mm, "end": v(-46.34, -29.05) * mm});
            skLineSegment(sketch, "E1661", {"start": v(-46.34, -29.05) * mm, "end": v(-46.34, -29.34) * mm});
            skLineSegment(sketch, "E1662", {"start": v(-46.34, -29.34) * mm, "end": v(-46.32, -30.13) * mm});
            skLineSegment(sketch, "E1663", {"start": v(-46.32, -30.13) * mm, "end": v(-46.32, -30.2) * mm});
            skLineSegment(sketch, "E1664", {"start": v(-46.32, -30.2) * mm, "end": v(-46.31, -30.27) * mm});
            skLineSegment(sketch, "E1665", {"start": v(-46.31, -30.27) * mm, "end": v(-46.15, -30.9) * mm});
            skLineSegment(sketch, "E1666", {"start": v(-46.15, -30.9) * mm, "end": v(-46.12, -30.96) * mm});
            skLineSegment(sketch, "E1667", {"start": v(-46.12, -30.96) * mm, "end": v(-46.1, -31) * mm});
            skLineSegment(sketch, "E1668", {"start": v(-46.1, -31) * mm, "end": v(-45.69, -31.4) * mm});
            skLineSegment(sketch, "E1669", {"start": v(-45.69, -31.4) * mm, "end": v(-45.63, -31.42) * mm});
            skLineSegment(sketch, "E1670", {"start": v(-45.63, -31.42) * mm, "end": v(-45.58, -31.44) * mm});
            skLineSegment(sketch, "E1671", {"start": v(-45.58, -31.44) * mm, "end": v(-44.94, -31.57) * mm});
            skLineSegment(sketch, "E1672", {"start": v(-44.94, -31.57) * mm, "end": v(-44.73, -31.57) * mm});
            skLineSegment(sketch, "E1673", {"start": v(-44.73, -31.57) * mm, "end": v(-44.53, -31.57) * mm});
            skLineSegment(sketch, "E1674", {"start": v(-44.53, -31.57) * mm, "end": v(-44.01, -31.47) * mm});
            skLineSegment(sketch, "E1675", {"start": v(-44.01, -31.47) * mm, "end": v(-43.95, -31.45) * mm});
            skLineSegment(sketch, "E1676", {"start": v(-43.95, -31.45) * mm, "end": v(-43.88, -31.43) * mm});
            skLineSegment(sketch, "E1677", {"start": v(-43.88, -31.43) * mm, "end": v(-43.43, -31.27) * mm});
            skLineSegment(sketch, "E1678", {"start": v(-43.43, -31.27) * mm, "end": v(-43.4, -31.26) * mm});
            skLineSegment(sketch, "E1679", {"start": v(-43.4, -31.26) * mm, "end": v(-43.3, -31.26) * mm});
            skLineSegment(sketch, "E1680", {"start": v(-43.3, -31.26) * mm, "end": v(-43.3, -32.74) * mm});
            skLineSegment(sketch, "E1681", {"start": v(-43.3, -32.74) * mm, "end": v(-43.38, -32.76) * mm});
            skLineSegment(sketch, "E1682", {"start": v(-43.38, -32.76) * mm, "end": v(-44.17, -32.93) * mm});
            skLineSegment(sketch, "E1683", {"start": v(-44.17, -32.93) * mm, "end": v(-44.25, -32.95) * mm});
            skLineSegment(sketch, "E1684", {"start": v(-44.25, -32.95) * mm, "end": v(-44.33, -32.96) * mm});
            skLineSegment(sketch, "E1685", {"start": v(-44.33, -32.96) * mm, "end": v(-44.93, -33.02) * mm});
            skLineSegment(sketch, "E1686", {"start": v(-44.93, -33.02) * mm, "end": v(-45.13, -33.02) * mm});
            skLineSegment(sketch, "E1687", {"start": v(-28.67, -23.02) * mm, "end": v(-31.15, -32.83) * mm});
            skLineSegment(sketch, "E1688", {"start": v(-31.15, -32.83) * mm, "end": v(-32.68, -32.83) * mm});
            skLineSegment(sketch, "E1689", {"start": v(-32.68, -32.83) * mm, "end": v(-35.08, -25.27) * mm});
            skLineSegment(sketch, "E1690", {"start": v(-35.08, -25.27) * mm, "end": v(-37.46, -32.83) * mm});
            skLineSegment(sketch, "E1691", {"start": v(-37.46, -32.83) * mm, "end": v(-38.98, -32.83) * mm});
            skLineSegment(sketch, "E1692", {"start": v(-38.98, -32.83) * mm, "end": v(-41.49, -23.02) * mm});
            skLineSegment(sketch, "E1693", {"start": v(-41.49, -23.02) * mm, "end": v(-39.77, -23.02) * mm});
            skLineSegment(sketch, "E1694", {"start": v(-39.77, -23.02) * mm, "end": v(-38.04, -30.62) * mm});
            skLineSegment(sketch, "E1695", {"start": v(-38.04, -30.62) * mm, "end": v(-35.71, -23.02) * mm});
            skLineSegment(sketch, "E1696", {"start": v(-35.71, -23.02) * mm, "end": v(-34.35, -23.02) * mm});
            skLineSegment(sketch, "E1697", {"start": v(-34.35, -23.02) * mm, "end": v(-31.96, -30.62) * mm});
            skLineSegment(sketch, "E1698", {"start": v(-31.96, -30.62) * mm, "end": v(-30.33, -23.02) * mm});
            skLineSegment(sketch, "E1699", {"start": v(-30.33, -23.02) * mm, "end": v(-28.67, -23.02) * mm});
            skLineSegment(sketch, "E1700", {"start": v(-20.36, -30.41) * mm, "end": v(-20.36, -27.7) * mm});
            skLineSegment(sketch, "E1701", {"start": v(-20.36, -27.7) * mm, "end": v(-20.46, -27.7) * mm});
            skLineSegment(sketch, "E1702", {"start": v(-20.46, -27.7) * mm, "end": v(-21.7, -27.82) * mm});
            skLineSegment(sketch, "E1703", {"start": v(-21.7, -27.82) * mm, "end": v(-21.85, -27.84) * mm});
            skLineSegment(sketch, "E1704", {"start": v(-21.85, -27.84) * mm, "end": v(-22, -27.85) * mm});
            skLineSegment(sketch, "E1705", {"start": v(-22, -27.85) * mm, "end": v(-23.2, -28.07) * mm});
            skLineSegment(sketch, "E1706", {"start": v(-23.2, -28.07) * mm, "end": v(-23.3, -28.1) * mm});
            skLineSegment(sketch, "E1707", {"start": v(-23.3, -28.1) * mm, "end": v(-23.41, -28.13) * mm});
            skLineSegment(sketch, "E1708", {"start": v(-23.41, -28.13) * mm, "end": v(-24.32, -28.64) * mm});
            skLineSegment(sketch, "E1709", {"start": v(-24.32, -28.64) * mm, "end": v(-24.39, -28.71) * mm});
            skLineSegment(sketch, "E1710", {"start": v(-24.39, -28.71) * mm, "end": v(-24.46, -28.78) * mm});
            skLineSegment(sketch, "E1711", {"start": v(-24.46, -28.78) * mm, "end": v(-24.71, -29.21) * mm});
            skLineSegment(sketch, "E1712", {"start": v(-24.71, -29.21) * mm, "end": v(-24.82, -29.71) * mm});
            skLineSegment(sketch, "E1713", {"start": v(-24.82, -29.71) * mm, "end": v(-24.82, -29.88) * mm});
            skLineSegment(sketch, "E1714", {"start": v(-24.82, -29.88) * mm, "end": v(-24.82, -30.06) * mm});
            skLineSegment(sketch, "E1715", {"start": v(-24.82, -30.06) * mm, "end": v(-24.7, -30.62) * mm});
            skLineSegment(sketch, "E1716", {"start": v(-24.7, -30.62) * mm, "end": v(-24.43, -31.08) * mm});
            skLineSegment(sketch, "E1717", {"start": v(-24.43, -31.08) * mm, "end": v(-24.35, -31.15) * mm});
            skLineSegment(sketch, "E1718", {"start": v(-24.35, -31.15) * mm, "end": v(-24.27, -31.22) * mm});
            skLineSegment(sketch, "E1719", {"start": v(-24.27, -31.22) * mm, "end": v(-23.76, -31.47) * mm});
            skLineSegment(sketch, "E1720", {"start": v(-23.76, -31.47) * mm, "end": v(-23.16, -31.58) * mm});
            skLineSegment(sketch, "E1721", {"start": v(-23.16, -31.58) * mm, "end": v(-22.96, -31.58) * mm});
            skLineSegment(sketch, "E1722", {"start": v(-22.96, -31.58) * mm, "end": v(-22.6, -31.58) * mm});
            skLineSegment(sketch, "E1723", {"start": v(-22.6, -31.58) * mm, "end": v(-21.65, -31.3) * mm});
            skLineSegment(sketch, "E1724", {"start": v(-21.65, -31.3) * mm, "end": v(-21.54, -31.24) * mm});
            skLineSegment(sketch, "E1725", {"start": v(-21.54, -31.24) * mm, "end": v(-21.44, -31.19) * mm});
            skLineSegment(sketch, "E1726", {"start": v(-21.44, -31.19) * mm, "end": v(-20.45, -30.5) * mm});
            skLineSegment(sketch, "E1727", {"start": v(-20.45, -30.5) * mm, "end": v(-20.36, -30.41) * mm});
            skLineSegment(sketch, "E1728", {"start": v(-20.36, -31.78) * mm, "end": v(-20.4, -31.8) * mm});
            skLineSegment(sketch, "E1729", {"start": v(-20.4, -31.8) * mm, "end": v(-20.84, -32.16) * mm});
            skLineSegment(sketch, "E1730", {"start": v(-20.84, -32.16) * mm, "end": v(-20.9, -32.2) * mm});
            skLineSegment(sketch, "E1731", {"start": v(-20.9, -32.2) * mm, "end": v(-20.96, -32.24) * mm});
            skLineSegment(sketch, "E1732", {"start": v(-20.96, -32.24) * mm, "end": v(-21.5, -32.6) * mm});
            skLineSegment(sketch, "E1733", {"start": v(-21.5, -32.6) * mm, "end": v(-21.55, -32.63) * mm});
            skLineSegment(sketch, "E1734", {"start": v(-21.55, -32.63) * mm, "end": v(-21.63, -32.66) * mm});
            skLineSegment(sketch, "E1735", {"start": v(-21.63, -32.66) * mm, "end": v(-22.33, -32.96) * mm});
            skLineSegment(sketch, "E1736", {"start": v(-22.33, -32.96) * mm, "end": v(-22.4, -32.98) * mm});
            skLineSegment(sketch, "E1737", {"start": v(-22.4, -32.98) * mm, "end": v(-22.47, -33) * mm});
            skLineSegment(sketch, "E1738", {"start": v(-22.47, -33) * mm, "end": v(-23.28, -33.1) * mm});
            skLineSegment(sketch, "E1739", {"start": v(-23.28, -33.1) * mm, "end": v(-23.55, -33.1) * mm});
            skLineSegment(sketch, "E1740", {"start": v(-23.55, -33.1) * mm, "end": v(-23.83, -33.1) * mm});
            skLineSegment(sketch, "E1741", {"start": v(-23.83, -33.1) * mm, "end": v(-24.6, -32.9) * mm});
            skLineSegment(sketch, "E1742", {"start": v(-24.6, -32.9) * mm, "end": v(-24.7, -32.87) * mm});
            skLineSegment(sketch, "E1743", {"start": v(-24.7, -32.87) * mm, "end": v(-24.79, -32.83) * mm});
            skLineSegment(sketch, "E1744", {"start": v(-24.79, -32.83) * mm, "end": v(-25.59, -32.3) * mm});
            skLineSegment(sketch, "E1745", {"start": v(-25.59, -32.3) * mm, "end": v(-25.65, -32.23) * mm});
            skLineSegment(sketch, "E1746", {"start": v(-25.65, -32.23) * mm, "end": v(-25.72, -32.16) * mm});
            skLineSegment(sketch, "E1747", {"start": v(-25.72, -32.16) * mm, "end": v(-26.25, -31.33) * mm});
            skLineSegment(sketch, "E1748", {"start": v(-26.25, -31.33) * mm, "end": v(-26.29, -31.23) * mm});
            skLineSegment(sketch, "E1749", {"start": v(-26.29, -31.23) * mm, "end": v(-26.33, -31.14) * mm});
            skLineSegment(sketch, "E1750", {"start": v(-26.33, -31.14) * mm, "end": v(-26.52, -30.27) * mm});
            skLineSegment(sketch, "E1751", {"start": v(-26.52, -30.27) * mm, "end": v(-26.52, -29.98) * mm});
            skLineSegment(sketch, "E1752", {"start": v(-26.52, -29.98) * mm, "end": v(-26.52, -29.75) * mm});
            skLineSegment(sketch, "E1753", {"start": v(-26.52, -29.75) * mm, "end": v(-26.42, -29.04) * mm});
            skLineSegment(sketch, "E1754", {"start": v(-26.42, -29.04) * mm, "end": v(-26.16, -28.37) * mm});
            skLineSegment(sketch, "E1755", {"start": v(-26.16, -28.37) * mm, "end": v(-26.1, -28.25) * mm});
            skLineSegment(sketch, "E1756", {"start": v(-26.1, -28.25) * mm, "end": v(-26.02, -28.13) * mm});
            skLineSegment(sketch, "E1757", {"start": v(-26.02, -28.13) * mm, "end": v(-25.54, -27.6) * mm});
            skLineSegment(sketch, "E1758", {"start": v(-25.54, -27.6) * mm, "end": v(-24.89, -27.18) * mm});
            skLineSegment(sketch, "E1759", {"start": v(-24.89, -27.18) * mm, "end": v(-24.73, -27.11) * mm});
            skLineSegment(sketch, "E1760", {"start": v(-24.73, -27.11) * mm, "end": v(-24.6, -27.05) * mm});
            skLineSegment(sketch, "E1761", {"start": v(-24.6, -27.05) * mm, "end": v(-22.97, -26.61) * mm});
            skLineSegment(sketch, "E1762", {"start": v(-22.97, -26.61) * mm, "end": v(-22.78, -26.59) * mm});
            skLineSegment(sketch, "E1763", {"start": v(-22.78, -26.59) * mm, "end": v(-22.6, -26.56) * mm});
            skLineSegment(sketch, "E1764", {"start": v(-22.6, -26.56) * mm, "end": v(-20.58, -26.39) * mm});
            skLineSegment(sketch, "E1765", {"start": v(-20.58, -26.39) * mm, "end": v(-20.36, -26.37) * mm});
            skLineSegment(sketch, "E1766", {"start": v(-20.36, -26.37) * mm, "end": v(-20.36, -26.06) * mm});
            skLineSegment(sketch, "E1767", {"start": v(-20.36, -26.06) * mm, "end": v(-20.36, -25.82) * mm});
            skLineSegment(sketch, "E1768", {"start": v(-20.36, -25.82) * mm, "end": v(-20.5, -25.18) * mm});
            skLineSegment(sketch, "E1769", {"start": v(-20.5, -25.18) * mm, "end": v(-20.53, -25.12) * mm});
            skLineSegment(sketch, "E1770", {"start": v(-20.53, -25.12) * mm, "end": v(-20.56, -25.06) * mm});
            skLineSegment(sketch, "E1771", {"start": v(-20.56, -25.06) * mm, "end": v(-20.97, -24.6) * mm});
            skLineSegment(sketch, "E1772", {"start": v(-20.97, -24.6) * mm, "end": v(-21.03, -24.57) * mm});
            skLineSegment(sketch, "E1773", {"start": v(-21.03, -24.57) * mm, "end": v(-21.08, -24.54) * mm});
            skLineSegment(sketch, "E1774", {"start": v(-21.08, -24.54) * mm, "end": v(-21.72, -24.32) * mm});
            skLineSegment(sketch, "E1775", {"start": v(-21.72, -24.32) * mm, "end": v(-21.8, -24.3) * mm});
            skLineSegment(sketch, "E1776", {"start": v(-21.8, -24.3) * mm, "end": v(-21.88, -24.3) * mm});
            skLineSegment(sketch, "E1777", {"start": v(-21.88, -24.3) * mm, "end": v(-22.52, -24.24) * mm});
            skLineSegment(sketch, "E1778", {"start": v(-22.52, -24.24) * mm, "end": v(-22.74, -24.24) * mm});
            skLineSegment(sketch, "E1779", {"start": v(-22.74, -24.24) * mm, "end": v(-23.08, -24.24) * mm});
            skLineSegment(sketch, "E1780", {"start": v(-23.08, -24.24) * mm, "end": v(-23.95, -24.38) * mm});
            skLineSegment(sketch, "E1781", {"start": v(-23.95, -24.38) * mm, "end": v(-24.08, -24.41) * mm});
            skLineSegment(sketch, "E1782", {"start": v(-24.08, -24.41) * mm, "end": v(-24.21, -24.44) * mm});
            skLineSegment(sketch, "E1783", {"start": v(-24.21, -24.44) * mm, "end": v(-25.5, -24.85) * mm});
            skLineSegment(sketch, "E1784", {"start": v(-25.5, -24.85) * mm, "end": v(-25.63, -24.9) * mm});
            skLineSegment(sketch, "E1785", {"start": v(-25.63, -24.9) * mm, "end": v(-25.73, -24.9) * mm});
            skLineSegment(sketch, "E1786", {"start": v(-25.73, -24.9) * mm, "end": v(-25.73, -23.23) * mm});
            skLineSegment(sketch, "E1787", {"start": v(-25.73, -23.23) * mm, "end": v(-25.65, -23.2) * mm});
            skLineSegment(sketch, "E1788", {"start": v(-25.65, -23.2) * mm, "end": v(-24.56, -22.97) * mm});
            skLineSegment(sketch, "E1789", {"start": v(-24.56, -22.97) * mm, "end": v(-24.42, -22.94) * mm});
            skLineSegment(sketch, "E1790", {"start": v(-24.42, -22.94) * mm, "end": v(-24.27, -22.91) * mm});
            skLineSegment(sketch, "E1791", {"start": v(-24.27, -22.91) * mm, "end": v(-23.12, -22.78) * mm});
            skLineSegment(sketch, "E1792", {"start": v(-23.12, -22.78) * mm, "end": v(-22.73, -22.78) * mm});
            skLineSegment(sketch, "E1793", {"start": v(-22.73, -22.78) * mm, "end": v(-22.3, -22.78) * mm});
            skLineSegment(sketch, "E1794", {"start": v(-22.3, -22.78) * mm, "end": v(-21.14, -22.91) * mm});
            skLineSegment(sketch, "E1795", {"start": v(-21.14, -22.91) * mm, "end": v(-21.03, -22.94) * mm});
            skLineSegment(sketch, "E1796", {"start": v(-21.03, -22.94) * mm, "end": v(-20.91, -22.97) * mm});
            skLineSegment(sketch, "E1797", {"start": v(-20.91, -22.97) * mm, "end": v(-19.87, -23.44) * mm});
            skLineSegment(sketch, "E1798", {"start": v(-19.87, -23.44) * mm, "end": v(-19.78, -23.51) * mm});
            skLineSegment(sketch, "E1799", {"start": v(-19.78, -23.51) * mm, "end": v(-19.7, -23.58) * mm});
            skLineSegment(sketch, "E1800", {"start": v(-19.7, -23.58) * mm, "end": v(-19.02, -24.45) * mm});
            skLineSegment(sketch, "E1801", {"start": v(-19.02, -24.45) * mm, "end": v(-18.98, -24.56) * mm});
            skLineSegment(sketch, "E1802", {"start": v(-18.98, -24.56) * mm, "end": v(-18.94, -24.66) * mm});
            skLineSegment(sketch, "E1803", {"start": v(-18.94, -24.66) * mm, "end": v(-18.72, -25.75) * mm});
            skLineSegment(sketch, "E1804", {"start": v(-18.72, -25.75) * mm, "end": v(-18.72, -26.12) * mm});
            skLineSegment(sketch, "E1805", {"start": v(-18.72, -26.12) * mm, "end": v(-18.72, -32.83) * mm});
            skLineSegment(sketch, "E1806", {"start": v(-18.72, -32.83) * mm, "end": v(-20.36, -32.83) * mm});
            skLineSegment(sketch, "E1807", {"start": v(-20.36, -32.83) * mm, "end": v(-20.36, -31.78) * mm});
            skLineSegment(sketch, "E1808", {"start": v(-9.67, -24.8) * mm, "end": v(-9.76, -24.8) * mm});
            skLineSegment(sketch, "E1809", {"start": v(-9.76, -24.8) * mm, "end": v(-9.8, -24.78) * mm});
            skLineSegment(sketch, "E1810", {"start": v(-9.8, -24.78) * mm, "end": v(-10.12, -24.73) * mm});
            skLineSegment(sketch, "E1811", {"start": v(-10.12, -24.73) * mm, "end": v(-10.15, -24.73) * mm});
            skLineSegment(sketch, "E1812", {"start": v(-10.15, -24.73) * mm, "end": v(-10.18, -24.72) * mm});
            skLineSegment(sketch, "E1813", {"start": v(-10.18, -24.72) * mm, "end": v(-10.53, -24.72) * mm});
            skLineSegment(sketch, "E1814", {"start": v(-10.53, -24.72) * mm, "end": v(-10.65, -24.72) * mm});
            skLineSegment(sketch, "E1815", {"start": v(-10.65, -24.72) * mm, "end": v(-10.98, -24.72) * mm});
            skLineSegment(sketch, "E1816", {"start": v(-10.98, -24.72) * mm, "end": v(-11.86, -24.95) * mm});
            skLineSegment(sketch, "E1817", {"start": v(-11.86, -24.95) * mm, "end": v(-11.97, -25) * mm});
            skLineSegment(sketch, "E1818", {"start": v(-11.97, -25) * mm, "end": v(-12.08, -25.05) * mm});
            skLineSegment(sketch, "E1819", {"start": v(-12.08, -25.05) * mm, "end": v(-13.12, -25.77) * mm});
            skLineSegment(sketch, "E1820", {"start": v(-13.12, -25.77) * mm, "end": v(-13.22, -25.86) * mm});
            skLineSegment(sketch, "E1821", {"start": v(-13.22, -25.86) * mm, "end": v(-13.22, -32.83) * mm});
            skLineSegment(sketch, "E1822", {"start": v(-13.22, -32.83) * mm, "end": v(-14.87, -32.83) * mm});
            skLineSegment(sketch, "E1823", {"start": v(-14.87, -32.83) * mm, "end": v(-14.87, -23.02) * mm});
            skLineSegment(sketch, "E1824", {"start": v(-14.87, -23.02) * mm, "end": v(-13.22, -23.02) * mm});
            skLineSegment(sketch, "E1825", {"start": v(-13.22, -23.02) * mm, "end": v(-13.22, -24.48) * mm});
            skLineSegment(sketch, "E1826", {"start": v(-13.22, -24.48) * mm, "end": v(-13.07, -24.34) * mm});
            skLineSegment(sketch, "E1827", {"start": v(-13.07, -24.34) * mm, "end": v(-12.37, -23.8) * mm});
            skLineSegment(sketch, "E1828", {"start": v(-12.37, -23.8) * mm, "end": v(-11.76, -23.4) * mm});
            skLineSegment(sketch, "E1829", {"start": v(-11.76, -23.4) * mm, "end": v(-11.64, -23.35) * mm});
            skLineSegment(sketch, "E1830", {"start": v(-11.64, -23.35) * mm, "end": v(-11.53, -23.3) * mm});
            skLineSegment(sketch, "E1831", {"start": v(-11.53, -23.3) * mm, "end": v(-10.64, -23.02) * mm});
            skLineSegment(sketch, "E1832", {"start": v(-10.64, -23.02) * mm, "end": v(-10.34, -23.02) * mm});
            skLineSegment(sketch, "E1833", {"start": v(-10.34, -23.02) * mm, "end": v(-10.24, -23.02) * mm});
            skLineSegment(sketch, "E1834", {"start": v(-10.24, -23.02) * mm, "end": v(-9.98, -23.03) * mm});
            skLineSegment(sketch, "E1835", {"start": v(-9.98, -23.03) * mm, "end": v(-9.96, -23.03) * mm});
            skLineSegment(sketch, "E1836", {"start": v(-9.96, -23.03) * mm, "end": v(-9.94, -23.03) * mm});
            skLineSegment(sketch, "E1837", {"start": v(-9.94, -23.03) * mm, "end": v(-9.7, -23.07) * mm});
            skLineSegment(sketch, "E1838", {"start": v(-9.7, -23.07) * mm, "end": v(-9.67, -23.07) * mm});
            skLineSegment(sketch, "E1839", {"start": v(-9.67, -23.07) * mm, "end": v(-9.67, -24.8) * mm});
            skLineSegment(sketch, "E1840", {"start": v(-0.76, -26.83) * mm, "end": v(-0.76, -26.72) * mm});
            skLineSegment(sketch, "E1841", {"start": v(-0.76, -26.72) * mm, "end": v(-0.9, -25.76) * mm});
            skLineSegment(sketch, "E1842", {"start": v(-0.9, -25.76) * mm, "end": v(-0.92, -25.68) * mm});
            skLineSegment(sketch, "E1843", {"start": v(-0.92, -25.68) * mm, "end": v(-0.94, -25.6) * mm});
            skLineSegment(sketch, "E1844", {"start": v(-0.94, -25.6) * mm, "end": v(-1.28, -24.92) * mm});
            skLineSegment(sketch, "E1845", {"start": v(-1.28, -24.92) * mm, "end": v(-1.32, -24.86) * mm});
            skLineSegment(sketch, "E1846", {"start": v(-1.32, -24.86) * mm, "end": v(-1.37, -24.8) * mm});
            skLineSegment(sketch, "E1847", {"start": v(-1.37, -24.8) * mm, "end": v(-1.99, -24.33) * mm});
            skLineSegment(sketch, "E1848", {"start": v(-1.99, -24.33) * mm, "end": v(-2.06, -24.3) * mm});
            skLineSegment(sketch, "E1849", {"start": v(-2.06, -24.3) * mm, "end": v(-2.14, -24.27) * mm});
            skLineSegment(sketch, "E1850", {"start": v(-2.14, -24.27) * mm, "end": v(-2.92, -24.1) * mm});
            skLineSegment(sketch, "E1851", {"start": v(-2.92, -24.1) * mm, "end": v(-3.18, -24.1) * mm});
            skLineSegment(sketch, "E1852", {"start": v(-3.18, -24.1) * mm, "end": v(-3.46, -24.1) * mm});
            skLineSegment(sketch, "E1853", {"start": v(-3.46, -24.1) * mm, "end": v(-4.22, -24.27) * mm});
            skLineSegment(sketch, "E1854", {"start": v(-4.22, -24.27) * mm, "end": v(-4.3, -24.3) * mm});
            skLineSegment(sketch, "E1855", {"start": v(-4.3, -24.3) * mm, "end": v(-4.38, -24.34) * mm});
            skLineSegment(sketch, "E1856", {"start": v(-4.38, -24.34) * mm, "end": v(-5.08, -24.82) * mm});
            skLineSegment(sketch, "E1857", {"start": v(-5.08, -24.82) * mm, "end": v(-5.14, -24.88) * mm});
            skLineSegment(sketch, "E1858", {"start": v(-5.14, -24.88) * mm, "end": v(-5.2, -24.95) * mm});
            skLineSegment(sketch, "E1859", {"start": v(-5.2, -24.95) * mm, "end": v(-5.67, -25.66) * mm});
            skLineSegment(sketch, "E1860", {"start": v(-5.67, -25.66) * mm, "end": v(-5.7, -25.74) * mm});
            skLineSegment(sketch, "E1861", {"start": v(-5.7, -25.74) * mm, "end": v(-5.74, -25.81) * mm});
            skLineSegment(sketch, "E1862", {"start": v(-5.74, -25.81) * mm, "end": v(-5.94, -26.73) * mm});
            skLineSegment(sketch, "E1863", {"start": v(-5.94, -26.73) * mm, "end": v(-5.95, -26.83) * mm});
            skLineSegment(sketch, "E1864", {"start": v(-5.95, -26.83) * mm, "end": v(-0.76, -26.83) * mm});
            skLineSegment(sketch, "E1865", {"start": v(-2.69, -33.06) * mm, "end": v(-3.21, -33.06) * mm});
            skLineSegment(sketch, "E1866", {"start": v(-3.21, -33.06) * mm, "end": v(-4.77, -32.73) * mm});
            skLineSegment(sketch, "E1867", {"start": v(-4.77, -32.73) * mm, "end": v(-6.11, -31.96) * mm});
            skLineSegment(sketch, "E1868", {"start": v(-6.11, -31.96) * mm, "end": v(-6.33, -31.73) * mm});
            skLineSegment(sketch, "E1869", {"start": v(-6.33, -31.73) * mm, "end": v(-6.55, -31.51) * mm});
            skLineSegment(sketch, "E1870", {"start": v(-6.55, -31.51) * mm, "end": v(-7.3, -30.13) * mm});
            skLineSegment(sketch, "E1871", {"start": v(-7.3, -30.13) * mm, "end": v(-7.62, -28.52) * mm});
            skLineSegment(sketch, "E1872", {"start": v(-7.62, -28.52) * mm, "end": v(-7.62, -27.98) * mm});
            skLineSegment(sketch, "E1873", {"start": v(-7.62, -27.98) * mm, "end": v(-7.62, -27.44) * mm});
            skLineSegment(sketch, "E1874", {"start": v(-7.62, -27.44) * mm, "end": v(-7.31, -25.83) * mm});
            skLineSegment(sketch, "E1875", {"start": v(-7.31, -25.83) * mm, "end": v(-6.58, -24.4) * mm});
            skLineSegment(sketch, "E1876", {"start": v(-6.58, -24.4) * mm, "end": v(-6.37, -24.17) * mm});
            skLineSegment(sketch, "E1877", {"start": v(-6.37, -24.17) * mm, "end": v(-6.16, -23.93) * mm});
            skLineSegment(sketch, "E1878", {"start": v(-6.16, -23.93) * mm, "end": v(-4.92, -23.1) * mm});
            skLineSegment(sketch, "E1879", {"start": v(-4.92, -23.1) * mm, "end": v(-3.54, -22.75) * mm});
            skLineSegment(sketch, "E1880", {"start": v(-3.54, -22.75) * mm, "end": v(-3.08, -22.75) * mm});
            skLineSegment(sketch, "E1881", {"start": v(-3.08, -22.75) * mm, "end": v(-2.68, -22.75) * mm});
            skLineSegment(sketch, "E1882", {"start": v(-2.68, -22.75) * mm, "end": v(-1.59, -22.97) * mm});
            skLineSegment(sketch, "E1883", {"start": v(-1.59, -22.97) * mm, "end": v(-1.47, -23.01) * mm});
            skLineSegment(sketch, "E1884", {"start": v(-1.47, -23.01) * mm, "end": v(-1.35, -23.05) * mm});
            skLineSegment(sketch, "E1885", {"start": v(-1.35, -23.05) * mm, "end": v(-0.33, -23.74) * mm});
            skLineSegment(sketch, "E1886", {"start": v(-0.33, -23.74) * mm, "end": v(-0.24, -23.84) * mm});
            skLineSegment(sketch, "E1887", {"start": v(-0.24, -23.84) * mm, "end": v(-0.15, -23.93) * mm});
            skLineSegment(sketch, "E1888", {"start": v(-0.15, -23.93) * mm, "end": v(0.52, -25.07) * mm});
            skLineSegment(sketch, "E1889", {"start": v(0.52, -25.07) * mm, "end": v(0.57, -25.21) * mm});
            skLineSegment(sketch, "E1890", {"start": v(0.57, -25.21) * mm, "end": v(0.61, -25.35) * mm});
            skLineSegment(sketch, "E1891", {"start": v(0.61, -25.35) * mm, "end": v(0.85, -26.74) * mm});
            skLineSegment(sketch, "E1892", {"start": v(0.85, -26.74) * mm, "end": v(0.85, -27.2) * mm});
            skLineSegment(sketch, "E1893", {"start": v(0.85, -27.2) * mm, "end": v(0.85, -28.1) * mm});
            skLineSegment(sketch, "E1894", {"start": v(0.85, -28.1) * mm, "end": v(-5.95, -28.1) * mm});
            skLineSegment(sketch, "E1895", {"start": v(-5.95, -28.1) * mm, "end": v(-5.95, -28.47) * mm});
            skLineSegment(sketch, "E1896", {"start": v(-5.95, -28.47) * mm, "end": v(-5.73, -29.6) * mm});
            skLineSegment(sketch, "E1897", {"start": v(-5.73, -29.6) * mm, "end": v(-5.23, -30.56) * mm});
            skLineSegment(sketch, "E1898", {"start": v(-5.23, -30.56) * mm, "end": v(-5.09, -30.71) * mm});
            skLineSegment(sketch, "E1899", {"start": v(-5.09, -30.71) * mm, "end": v(-4.94, -30.86) * mm});
            skLineSegment(sketch, "E1900", {"start": v(-4.94, -30.86) * mm, "end": v(-4.06, -31.39) * mm});
            skLineSegment(sketch, "E1901", {"start": v(-4.06, -31.39) * mm, "end": v(-3.05, -31.62) * mm});
            skLineSegment(sketch, "E1902", {"start": v(-3.05, -31.62) * mm, "end": v(-2.7, -31.62) * mm});
            skLineSegment(sketch, "E1903", {"start": v(-2.7, -31.62) * mm, "end": v(-2.44, -31.62) * mm});
            skLineSegment(sketch, "E1904", {"start": v(-2.44, -31.62) * mm, "end": v(-1.73, -31.51) * mm});
            skLineSegment(sketch, "E1905", {"start": v(-1.73, -31.51) * mm, "end": v(-1.64, -31.5) * mm});
            skLineSegment(sketch, "E1906", {"start": v(-1.64, -31.5) * mm, "end": v(-1.55, -31.47) * mm});
            skLineSegment(sketch, "E1907", {"start": v(-1.55, -31.47) * mm, "end": v(-0.77, -31.2) * mm});
            skLineSegment(sketch, "E1908", {"start": v(-0.77, -31.2) * mm, "end": v(-0.7, -31.18) * mm});
            skLineSegment(sketch, "E1909", {"start": v(-0.7, -31.18) * mm, "end": v(-0.62, -31.14) * mm});
            skLineSegment(sketch, "E1910", {"start": v(-0.62, -31.14) * mm, "end": v(0, -30.82) * mm});
            skLineSegment(sketch, "E1911", {"start": v(0, -30.82) * mm, "end": v(0.06, -30.79) * mm});
            skLineSegment(sketch, "E1912", {"start": v(0.06, -30.79) * mm, "end": v(0.11, -30.75) * mm});
            skLineSegment(sketch, "E1913", {"start": v(0.11, -30.75) * mm, "end": v(0.53, -30.46) * mm});
            skLineSegment(sketch, "E1914", {"start": v(0.53, -30.46) * mm, "end": v(0.57, -30.43) * mm});
            skLineSegment(sketch, "E1915", {"start": v(0.57, -30.43) * mm, "end": v(0.67, -30.43) * mm});
            skLineSegment(sketch, "E1916", {"start": v(0.67, -30.43) * mm, "end": v(0.67, -32.23) * mm});
            skLineSegment(sketch, "E1917", {"start": v(0.67, -32.23) * mm, "end": v(0.62, -32.25) * mm});
            skLineSegment(sketch, "E1918", {"start": v(0.62, -32.25) * mm, "end": v(0.02, -32.49) * mm});
            skLineSegment(sketch, "E1919", {"start": v(0.02, -32.49) * mm, "end": v(-0.05, -32.52) * mm});
            skLineSegment(sketch, "E1920", {"start": v(-0.05, -32.52) * mm, "end": v(-0.13, -32.54) * mm});
            skLineSegment(sketch, "E1921", {"start": v(-0.13, -32.54) * mm, "end": v(-0.77, -32.77) * mm});
            skLineSegment(sketch, "E1922", {"start": v(-0.77, -32.77) * mm, "end": v(-0.83, -32.78) * mm});
            skLineSegment(sketch, "E1923", {"start": v(-0.83, -32.78) * mm, "end": v(-0.9, -32.8) * mm});
            skLineSegment(sketch, "E1924", {"start": v(-0.9, -32.8) * mm, "end": v(-1.64, -32.97) * mm});
            skLineSegment(sketch, "E1925", {"start": v(-1.64, -32.97) * mm, "end": v(-1.7, -32.99) * mm});
            skLineSegment(sketch, "E1926", {"start": v(-1.7, -32.99) * mm, "end": v(-1.77, -33) * mm});
            skLineSegment(sketch, "E1927", {"start": v(-1.77, -33) * mm, "end": v(-2.46, -33.06) * mm});
            skLineSegment(sketch, "E1928", {"start": v(-2.46, -33.06) * mm, "end": v(-2.69, -33.06) * mm});
            skLineSegment(sketch, "E1929", {"start": v(12.88, -32.83) * mm, "end": v(11.23, -32.83) * mm});
            skLineSegment(sketch, "E1930", {"start": v(11.23, -32.83) * mm, "end": v(11.23, -23.02) * mm});
            skLineSegment(sketch, "E1931", {"start": v(11.23, -23.02) * mm, "end": v(12.88, -23.02) * mm});
            skLineSegment(sketch, "E1932", {"start": v(12.88, -23.02) * mm, "end": v(12.88, -32.83) * mm});
            skLineSegment(sketch, "E1933", {"start": v(13, -21.38) * mm, "end": v(11.12, -21.38) * mm});
            skLineSegment(sketch, "E1934", {"start": v(11.12, -21.38) * mm, "end": v(11.12, -19.66) * mm});
            skLineSegment(sketch, "E1935", {"start": v(11.12, -19.66) * mm, "end": v(13, -19.66) * mm});
            skLineSegment(sketch, "E1936", {"start": v(13, -19.66) * mm, "end": v(13, -21.38) * mm});
            skLineSegment(sketch, "E1937", {"start": v(19.49, -33.07) * mm, "end": v(19.03, -33.07) * mm});
            skLineSegment(sketch, "E1938", {"start": v(19.03, -33.07) * mm, "end": v(17.79, -32.85) * mm});
            skLineSegment(sketch, "E1939", {"start": v(17.79, -32.85) * mm, "end": v(17.65, -32.8) * mm});
            skLineSegment(sketch, "E1940", {"start": v(17.65, -32.8) * mm, "end": v(17.5, -32.76) * mm});
            skLineSegment(sketch, "E1941", {"start": v(17.5, -32.76) * mm, "end": v(16.32, -32.3) * mm});
            skLineSegment(sketch, "E1942", {"start": v(16.32, -32.3) * mm, "end": v(16.23, -32.24) * mm});
            skLineSegment(sketch, "E1943", {"start": v(16.23, -32.24) * mm, "end": v(16.23, -30.39) * mm});
            skLineSegment(sketch, "E1944", {"start": v(16.23, -30.39) * mm, "end": v(16.32, -30.39) * mm});
            skLineSegment(sketch, "E1945", {"start": v(16.32, -30.39) * mm, "end": v(16.35, -30.41) * mm});
            skLineSegment(sketch, "E1946", {"start": v(16.35, -30.41) * mm, "end": v(16.76, -30.72) * mm});
            skLineSegment(sketch, "E1947", {"start": v(16.76, -30.72) * mm, "end": v(16.81, -30.76) * mm});
            skLineSegment(sketch, "E1948", {"start": v(16.81, -30.76) * mm, "end": v(16.86, -30.79) * mm});
            skLineSegment(sketch, "E1949", {"start": v(16.86, -30.79) * mm, "end": v(17.5, -31.14) * mm});
            skLineSegment(sketch, "E1950", {"start": v(17.5, -31.14) * mm, "end": v(17.57, -31.18) * mm});
            skLineSegment(sketch, "E1951", {"start": v(17.57, -31.18) * mm, "end": v(17.64, -31.2) * mm});
            skLineSegment(sketch, "E1952", {"start": v(17.64, -31.2) * mm, "end": v(18.41, -31.5) * mm});
            skLineSegment(sketch, "E1953", {"start": v(18.41, -31.5) * mm, "end": v(18.5, -31.52) * mm});
            skLineSegment(sketch, "E1954", {"start": v(18.5, -31.52) * mm, "end": v(18.58, -31.54) * mm});
            skLineSegment(sketch, "E1955", {"start": v(18.58, -31.54) * mm, "end": v(19.3, -31.67) * mm});
            skLineSegment(sketch, "E1956", {"start": v(19.3, -31.67) * mm, "end": v(19.55, -31.67) * mm});
            skLineSegment(sketch, "E1957", {"start": v(19.55, -31.67) * mm, "end": v(19.76, -31.67) * mm});
            skLineSegment(sketch, "E1958", {"start": v(19.76, -31.67) * mm, "end": v(20.32, -31.6) * mm});
            skLineSegment(sketch, "E1959", {"start": v(20.32, -31.6) * mm, "end": v(20.39, -31.58) * mm});
            skLineSegment(sketch, "E1960", {"start": v(20.39, -31.58) * mm, "end": v(20.46, -31.56) * mm});
            skLineSegment(sketch, "E1961", {"start": v(20.46, -31.56) * mm, "end": v(21.02, -31.37) * mm});
            skLineSegment(sketch, "E1962", {"start": v(21.02, -31.37) * mm, "end": v(21.06, -31.34) * mm});
            skLineSegment(sketch, "E1963", {"start": v(21.06, -31.34) * mm, "end": v(21.1, -31.31) * mm});
            skLineSegment(sketch, "E1964", {"start": v(21.1, -31.31) * mm, "end": v(21.48, -30.95) * mm});
            skLineSegment(sketch, "E1965", {"start": v(21.48, -30.95) * mm, "end": v(21.5, -30.91) * mm});
            skLineSegment(sketch, "E1966", {"start": v(21.5, -30.91) * mm, "end": v(21.52, -30.87) * mm});
            skLineSegment(sketch, "E1967", {"start": v(21.52, -30.87) * mm, "end": v(21.64, -30.39) * mm});
            skLineSegment(sketch, "E1968", {"start": v(21.64, -30.39) * mm, "end": v(21.64, -30.23) * mm});
            skLineSegment(sketch, "E1969", {"start": v(21.64, -30.23) * mm, "end": v(21.64, -30) * mm});
            skLineSegment(sketch, "E1970", {"start": v(21.64, -30) * mm, "end": v(21.37, -29.4) * mm});
            skLineSegment(sketch, "E1971", {"start": v(21.37, -29.4) * mm, "end": v(21.32, -29.34) * mm});
            skLineSegment(sketch, "E1972", {"start": v(21.32, -29.34) * mm, "end": v(21.26, -29.3) * mm});
            skLineSegment(sketch, "E1973", {"start": v(21.26, -29.3) * mm, "end": v(20.32, -28.88) * mm});
            skLineSegment(sketch, "E1974", {"start": v(20.32, -28.88) * mm, "end": v(20.18, -28.84) * mm});
            skLineSegment(sketch, "E1975", {"start": v(20.18, -28.84) * mm, "end": v(20.13, -28.83) * mm});
            skLineSegment(sketch, "E1976", {"start": v(20.13, -28.83) * mm, "end": v(19.44, -28.67) * mm});
            skLineSegment(sketch, "E1977", {"start": v(19.44, -28.67) * mm, "end": v(19.35, -28.66) * mm});
            skLineSegment(sketch, "E1978", {"start": v(19.35, -28.66) * mm, "end": v(19.27, -28.64) * mm});
            skLineSegment(sketch, "E1979", {"start": v(19.27, -28.64) * mm, "end": v(18.49, -28.45) * mm});
            skLineSegment(sketch, "E1980", {"start": v(18.49, -28.45) * mm, "end": v(18.42, -28.43) * mm});
            skLineSegment(sketch, "E1981", {"start": v(18.42, -28.43) * mm, "end": v(18.23, -28.37) * mm});
            skLineSegment(sketch, "E1982", {"start": v(18.23, -28.37) * mm, "end": v(17.44, -28.02) * mm});
            skLineSegment(sketch, "E1983", {"start": v(17.44, -28.02) * mm, "end": v(16.86, -27.54) * mm});
            skLineSegment(sketch, "E1984", {"start": v(16.86, -27.54) * mm, "end": v(16.78, -27.42) * mm});
            skLineSegment(sketch, "E1985", {"start": v(16.78, -27.42) * mm, "end": v(16.7, -27.3) * mm});
            skLineSegment(sketch, "E1986", {"start": v(16.7, -27.3) * mm, "end": v(16.4, -26.67) * mm});
            skLineSegment(sketch, "E1987", {"start": v(16.4, -26.67) * mm, "end": v(16.27, -26) * mm});
            skLineSegment(sketch, "E1988", {"start": v(16.27, -26) * mm, "end": v(16.27, -25.78) * mm});
            skLineSegment(sketch, "E1989", {"start": v(16.27, -25.78) * mm, "end": v(16.27, -25.47) * mm});
            skLineSegment(sketch, "E1990", {"start": v(16.27, -25.47) * mm, "end": v(16.52, -24.57) * mm});
            skLineSegment(sketch, "E1991", {"start": v(16.52, -24.57) * mm, "end": v(17.1, -23.76) * mm});
            skLineSegment(sketch, "E1992", {"start": v(17.1, -23.76) * mm, "end": v(17.27, -23.62) * mm});
            skLineSegment(sketch, "E1993", {"start": v(17.27, -23.62) * mm, "end": v(17.44, -23.48) * mm});
            skLineSegment(sketch, "E1994", {"start": v(17.44, -23.48) * mm, "end": v(18.44, -23) * mm});
            skLineSegment(sketch, "E1995", {"start": v(18.44, -23) * mm, "end": v(19.56, -22.78) * mm});
            skLineSegment(sketch, "E1996", {"start": v(19.56, -22.78) * mm, "end": v(19.93, -22.78) * mm});
            skLineSegment(sketch, "E1997", {"start": v(19.93, -22.78) * mm, "end": v(20.34, -22.78) * mm});
            skLineSegment(sketch, "E1998", {"start": v(20.34, -22.78) * mm, "end": v(21.44, -22.95) * mm});
            skLineSegment(sketch, "E1999", {"start": v(21.44, -22.95) * mm, "end": v(21.58, -22.98) * mm});
            skLineSegment(sketch, "E2000", {"start": v(21.58, -22.98) * mm, "end": v(21.71, -23.02) * mm});
            skLineSegment(sketch, "E2001", {"start": v(21.71, -23.02) * mm, "end": v(22.87, -23.44) * mm});
            skLineSegment(sketch, "E2002", {"start": v(22.87, -23.44) * mm, "end": v(22.96, -23.5) * mm});
            skLineSegment(sketch, "E2003", {"start": v(22.96, -23.5) * mm, "end": v(22.96, -25.26) * mm});
            skLineSegment(sketch, "E2004", {"start": v(22.96, -25.26) * mm, "end": v(22.88, -25.26) * mm});
            skLineSegment(sketch, "E2005", {"start": v(22.88, -25.26) * mm, "end": v(22.77, -25.17) * mm});
            skLineSegment(sketch, "E2006", {"start": v(22.77, -25.17) * mm, "end": v(21.6, -24.52) * mm});
            skLineSegment(sketch, "E2007", {"start": v(21.6, -24.52) * mm, "end": v(21.47, -24.47) * mm});
            skLineSegment(sketch, "E2008", {"start": v(21.47, -24.47) * mm, "end": v(21.34, -24.42) * mm});
            skLineSegment(sketch, "E2009", {"start": v(21.34, -24.42) * mm, "end": v(20.26, -24.18) * mm});
            skLineSegment(sketch, "E2010", {"start": v(20.26, -24.18) * mm, "end": v(19.9, -24.18) * mm});
            skLineSegment(sketch, "E2011", {"start": v(19.9, -24.18) * mm, "end": v(19.55, -24.18) * mm});
            skLineSegment(sketch, "E2012", {"start": v(19.55, -24.18) * mm, "end": v(18.61, -24.46) * mm});
            skLineSegment(sketch, "E2013", {"start": v(18.61, -24.46) * mm, "end": v(18.52, -24.52) * mm});
            skLineSegment(sketch, "E2014", {"start": v(18.52, -24.52) * mm, "end": v(18.43, -24.58) * mm});
            skLineSegment(sketch, "E2015", {"start": v(18.43, -24.58) * mm, "end": v(18.1, -24.95) * mm});
            skLineSegment(sketch, "E2016", {"start": v(18.1, -24.95) * mm, "end": v(17.96, -25.4) * mm});
            skLineSegment(sketch, "E2017", {"start": v(17.96, -25.4) * mm, "end": v(17.96, -25.56) * mm});
            skLineSegment(sketch, "E2018", {"start": v(17.96, -25.56) * mm, "end": v(17.96, -25.79) * mm});
            skLineSegment(sketch, "E2019", {"start": v(17.96, -25.79) * mm, "end": v(18.24, -26.42) * mm});
            skLineSegment(sketch, "E2020", {"start": v(18.24, -26.42) * mm, "end": v(18.3, -26.47) * mm});
            skLineSegment(sketch, "E2021", {"start": v(18.3, -26.47) * mm, "end": v(18.35, -26.52) * mm});
            skLineSegment(sketch, "E2022", {"start": v(18.35, -26.52) * mm, "end": v(19.24, -26.94) * mm});
            skLineSegment(sketch, "E2023", {"start": v(19.24, -26.94) * mm, "end": v(19.36, -26.97) * mm});
            skLineSegment(sketch, "E2024", {"start": v(19.36, -26.97) * mm, "end": v(19.42, -26.99) * mm});
            skLineSegment(sketch, "E2025", {"start": v(19.42, -26.99) * mm, "end": v(20.1, -27.14) * mm});
            skLineSegment(sketch, "E2026", {"start": v(20.1, -27.14) * mm, "end": v(20.18, -27.16) * mm});
            skLineSegment(sketch, "E2027", {"start": v(20.18, -27.16) * mm, "end": v(20.26, -27.17) * mm});
            skLineSegment(sketch, "E2028", {"start": v(20.26, -27.17) * mm, "end": v(21.05, -27.35) * mm});
            skLineSegment(sketch, "E2029", {"start": v(21.05, -27.35) * mm, "end": v(21.14, -27.38) * mm});
            skLineSegment(sketch, "E2030", {"start": v(21.14, -27.38) * mm, "end": v(21.32, -27.42) * mm});
            skLineSegment(sketch, "E2031", {"start": v(21.32, -27.42) * mm, "end": v(22.1, -27.74) * mm});
            skLineSegment(sketch, "E2032", {"start": v(22.1, -27.74) * mm, "end": v(22.68, -28.17) * mm});
            skLineSegment(sketch, "E2033", {"start": v(22.68, -28.17) * mm, "end": v(22.78, -28.28) * mm});
            skLineSegment(sketch, "E2034", {"start": v(22.78, -28.28) * mm, "end": v(22.87, -28.38) * mm});
            skLineSegment(sketch, "E2035", {"start": v(22.87, -28.38) * mm, "end": v(23.19, -29.03) * mm});
            skLineSegment(sketch, "E2036", {"start": v(23.19, -29.03) * mm, "end": v(23.32, -29.76) * mm});
            skLineSegment(sketch, "E2037", {"start": v(23.32, -29.76) * mm, "end": v(23.32, -30) * mm});
            skLineSegment(sketch, "E2038", {"start": v(23.32, -30) * mm, "end": v(23.32, -30.3) * mm});
            skLineSegment(sketch, "E2039", {"start": v(23.32, -30.3) * mm, "end": v(23.11, -31.1) * mm});
            skLineSegment(sketch, "E2040", {"start": v(23.11, -31.1) * mm, "end": v(23.07, -31.2) * mm});
            skLineSegment(sketch, "E2041", {"start": v(23.07, -31.2) * mm, "end": v(23.03, -31.3) * mm});
            skLineSegment(sketch, "E2042", {"start": v(23.03, -31.3) * mm, "end": v(22.42, -32.1) * mm});
            skLineSegment(sketch, "E2043", {"start": v(22.42, -32.1) * mm, "end": v(22.34, -32.17) * mm});
            skLineSegment(sketch, "E2044", {"start": v(22.34, -32.17) * mm, "end": v(22.25, -32.24) * mm});
            skLineSegment(sketch, "E2045", {"start": v(22.25, -32.24) * mm, "end": v(21.26, -32.8) * mm});
            skLineSegment(sketch, "E2046", {"start": v(21.26, -32.8) * mm, "end": v(21.15, -32.84) * mm});
            skLineSegment(sketch, "E2047", {"start": v(21.15, -32.84) * mm, "end": v(21.04, -32.88) * mm});
            skLineSegment(sketch, "E2048", {"start": v(21.04, -32.88) * mm, "end": v(19.87, -33.07) * mm});
            skLineSegment(sketch, "E2049", {"start": v(19.87, -33.07) * mm, "end": v(19.49, -33.07) * mm});
            skSolve(sketch);
        }
        {
            var Q0;
            Q0=makeQuery(id+"F0.imprint","IMPRINT",FACE,{"disambiguationData":[TD([[makeQuery(id+"F0.imprint","IMPRINT",EDGE,{"derivedFrom":sQuery(id+"F0.wireOp",EDGE,"E306")}),-1.0]])]});
            var Q1;
            Q1=makeQuery(id+"F0.imprint","IMPRINT",FACE,{"disambiguationData":[TD([[makeQuery(id+"F0.imprint","IMPRINT",EDGE,{"derivedFrom":sQuery(id+"F0.wireOp",EDGE,"E117")}),-1.0]])]});
            var Q2;
            Q2=makeQuery(id+"F0.imprint","IMPRINT",FACE,{"disambiguationData":[TD([[makeQuery(id+"F0.imprint","IMPRINT",EDGE,{"derivedFrom":sQuery(id+"F0.wireOp",EDGE,"E591")}),-1.0]])]});
            var Q3;
            Q3=makeQuery(id+"F0.imprint","IMPRINT",FACE,{"disambiguationData":[TD([[makeQuery(id+"F0.imprint","IMPRINT",EDGE,{"derivedFrom":sQuery(id+"F0.wireOp",EDGE,"E254")}),-1.0]])]});
            var Q4;
            Q4=makeQuery(id+"F0.imprint","IMPRINT",FACE,{"disambiguationData":[TD([[makeQuery(id+"F0.imprint","IMPRINT",EDGE,{"derivedFrom":sQuery(id+"F0.wireOp",EDGE,"E0")}),-1.0]])]});
            var Q5;
            Q5=makeQuery(id+"F0.imprint","IMPRINT",FACE,{"disambiguationData":[TD([[makeQuery(id+"F0.imprint","IMPRINT",EDGE,{"derivedFrom":sQuery(id+"F0.wireOp",EDGE,"E1929")}),-1.0]])]});
            var Q6;
            Q6=makeQuery(id+"F0.imprint","IMPRINT",FACE,{"disambiguationData":[TD([[makeQuery(id+"F0.imprint","IMPRINT",EDGE,{"derivedFrom":sQuery(id+"F0.wireOp",EDGE,"E447")}),-1.0]])]});
            var Q7;
            Q7=makeQuery(id+"F0.imprint","IMPRINT",FACE,{"disambiguationData":[TD([[makeQuery(id+"F0.imprint","IMPRINT",EDGE,{"derivedFrom":sQuery(id+"F0.wireOp",EDGE,"E443")}),-1.0]])]});
            var Q8;
            Q8=makeQuery(id+"F0.imprint","IMPRINT",FACE,{"disambiguationData":[TD([[makeQuery(id+"F0.imprint","IMPRINT",EDGE,{"derivedFrom":sQuery(id+"F0.wireOp",EDGE,"E1687")}),-1.0]])]});
            var Q9;
            Q9=makeQuery(id+"F0.imprint","IMPRINT",FACE,{"disambiguationData":[TD([[makeQuery(id+"F0.imprint","IMPRINT",EDGE,{"derivedFrom":sQuery(id+"F0.wireOp",EDGE,"E884")}),-1.0]])]});
            var Q10;
            Q10=makeQuery(id+"F0.imprint","IMPRINT",FACE,{"disambiguationData":[TD([[makeQuery(id+"F0.imprint","IMPRINT",EDGE,{"derivedFrom":sQuery(id+"F0.wireOp",EDGE,"E1384")}),-1.0]])]});
            var Q11;
            Q11=makeQuery(id+"F0.imprint","IMPRINT",FACE,{"disambiguationData":[TD([[makeQuery(id+"F0.imprint","IMPRINT",EDGE,{"derivedFrom":sQuery(id+"F0.wireOp",EDGE,"E1808")}),-1.0]])]});
            var Q12;
            Q12=makeQuery(id+"F0.imprint","IMPRINT",FACE,{"disambiguationData":[TD([[makeQuery(id+"F0.imprint","IMPRINT",EDGE,{"derivedFrom":sQuery(id+"F0.wireOp",EDGE,"E1933")}),-1.0]])]});
            var Q13;
            Q13=makeQuery(id+"F0.imprint","IMPRINT",FACE,{"disambiguationData":[TD([[makeQuery(id+"F0.imprint","IMPRINT",EDGE,{"derivedFrom":sQuery(id+"F0.wireOp",EDGE,"E840")}),-1.0]])]});
            var Q14;
            Q14=makeQuery(id+"F0.imprint","IMPRINT",FACE,{"disambiguationData":[TD([[makeQuery(id+"F0.imprint","IMPRINT",EDGE,{"derivedFrom":sQuery(id+"F0.wireOp",EDGE,"E643")}),-1.0]])]});
            var Q15;
            Q15=makeQuery(id+"F0.imprint","IMPRINT",FACE,{"disambiguationData":[TD([[makeQuery(id+"F0.imprint","IMPRINT",EDGE,{"derivedFrom":sQuery(id+"F0.wireOp",EDGE,"E1312")}),-1.0]])]});
            var Q16;
            Q16=makeQuery(id+"F0.imprint","IMPRINT",FACE,{"disambiguationData":[TD([[makeQuery(id+"F0.imprint","IMPRINT",EDGE,{"derivedFrom":sQuery(id+"F0.wireOp",EDGE,"E1601")}),-1.0]])]});
            var Q17;
            Q17=makeQuery(id+"F0.imprint","IMPRINT",FACE,{"disambiguationData":[TD([[makeQuery(id+"F0.imprint","IMPRINT",EDGE,{"derivedFrom":sQuery(id+"F0.wireOp",EDGE,"E455")}),-1.0]])]});
            var Q18;
            Q18=makeQuery(id+"F0.imprint","IMPRINT",FACE,{"disambiguationData":[TD([[makeQuery(id+"F0.imprint","IMPRINT",EDGE,{"derivedFrom":sQuery(id+"F0.wireOp",EDGE,"E1642")}),-1.0]])]});
            var Q19;
            Q19=makeQuery(id+"F0.imprint","IMPRINT",FACE,{"disambiguationData":[TD([[makeQuery(id+"F0.imprint","IMPRINT",EDGE,{"derivedFrom":sQuery(id+"F0.wireOp",EDGE,"E916")}),-1.0]])]});
            var Q20;
            Q20=makeQuery(id+"F0.imprint","IMPRINT",FACE,{"disambiguationData":[TD([[makeQuery(id+"F0.imprint","IMPRINT",EDGE,{"derivedFrom":sQuery(id+"F0.wireOp",EDGE,"E1316")}),-1.0]])]});
            var Q21;
            Q21=makeQuery(id+"F0.imprint","IMPRINT",FACE,{"disambiguationData":[TD([[makeQuery(id+"F0.imprint","IMPRINT",EDGE,{"derivedFrom":sQuery(id+"F0.wireOp",EDGE,"E776")}),-1.0]])]});
            var Q22;
            Q22=makeQuery(id+"F0.imprint","IMPRINT",FACE,{"disambiguationData":[TD([[makeQuery(id+"F0.imprint","IMPRINT",EDGE,{"derivedFrom":sQuery(id+"F0.wireOp",EDGE,"E1320")}),-1.0]])]});
            var Q23;
            Q23=makeQuery(id+"F0.imprint","IMPRINT",FACE,{"disambiguationData":[TD([[makeQuery(id+"F0.imprint","IMPRINT",EDGE,{"derivedFrom":sQuery(id+"F0.wireOp",EDGE,"E1537")}),-1.0]])]});
            var Q24;
            Q24=makeQuery(id+"F0.imprint","IMPRINT",FACE,{"disambiguationData":[TD([[makeQuery(id+"F0.imprint","IMPRINT",EDGE,{"derivedFrom":sQuery(id+"F0.wireOp",EDGE,"E1840")}),-1.0]])]});
            var Q25;
            Q25=makeQuery(id+"F0.imprint","IMPRINT",FACE,{"disambiguationData":[TD([[makeQuery(id+"F0.imprint","IMPRINT",EDGE,{"derivedFrom":sQuery(id+"F0.wireOp",EDGE,"E1424")}),-1.0]])]});
            var Q26;
            Q26=makeQuery(id+"F0.imprint","IMPRINT",FACE,{"disambiguationData":[TD([[makeQuery(id+"F0.imprint","IMPRINT",EDGE,{"derivedFrom":sQuery(id+"F0.wireOp",EDGE,"E1700")}),-1.0]])]});
            var Q27;
            Q27=makeQuery(id+"F0.imprint","IMPRINT",FACE,{"disambiguationData":[TD([[makeQuery(id+"F0.imprint","IMPRINT",EDGE,{"derivedFrom":sQuery(id+"F0.wireOp",EDGE,"E1937")}),-1.0]])]});
            var Q28;
            Q28=makeQuery(id+"F0.imprint","IMPRINT",FACE,{"disambiguationData":[TD([[makeQuery(id+"F0.imprint","IMPRINT",EDGE,{"derivedFrom":sQuery(id+"F0.wireOp",EDGE,"E1199")}),-1.0]])]});
            var Q29;
            Q29=makeQuery(id+"F0.imprint","IMPRINT",FACE,{"disambiguationData":[TD([[makeQuery(id+"F0.imprint","IMPRINT",EDGE,{"derivedFrom":sQuery(id+"F0.wireOp",EDGE,"E1086")}),-1.0]])]});
            var Q30;
            Q30=makeQuery(id+"F0.imprint","IMPRINT",FACE,{"disambiguationData":[TD([[makeQuery(id+"F0.imprint","IMPRINT",EDGE,{"derivedFrom":sQuery(id+"F0.wireOp",EDGE,"E978")}),-1.0]])]});
            extrude(context, id + "F1", {"entities" : qUnion([Q0, Q1, Q2, Q3, Q4, Q5, Q6, Q7, Q8, Q9, Q10, Q11, Q12, Q13, Q14, Q15, Q16, Q17, Q18, Q19, Q20, Q21, Q22, Q23, Q24, Q25, Q26, Q27, Q28, Q29, Q30]), "depth" : 25.4 * mm, "offsetDistance" : 25.4 * mm});
        }
    });
